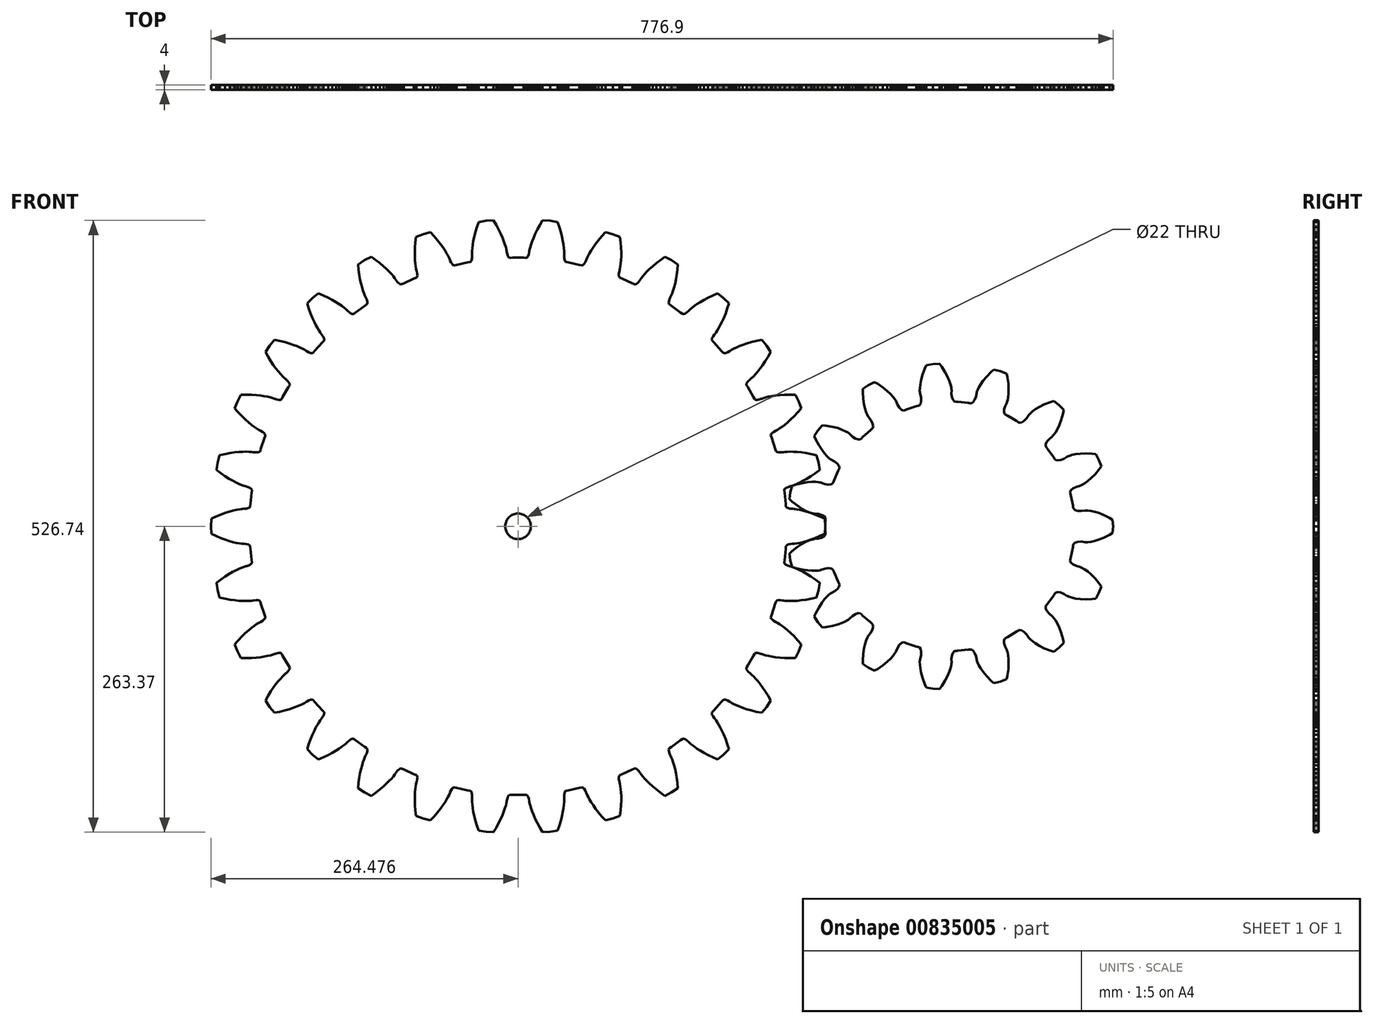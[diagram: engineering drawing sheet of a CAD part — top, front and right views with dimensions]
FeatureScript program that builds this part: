
annotation { "Feature Type Name" : "Feature", "Feature Type Description" : "" }
export const myFeature = defineFeature(function(context is Context, id is Id, definition is map)
    precondition{}
    {
        {
            var Q0;
            Q0=qCreatedBy(makeId("Front.planeOp"),FACE);
            var sketch = newSketch(context, id + "F0", { "sketchPlane" : qUnion([Q0])});
            skLineSegment(sketch, "E0", {"start": v(133.04, -61.26) * mm, "end": v(134.72, -54.99) * mm});
            skLineSegment(sketch, "E1", {"start": v(134.72, -54.99) * mm, "end": v(135.74, -48.57) * mm});
            skLineSegment(sketch, "E2", {"start": v(135.74, -48.57) * mm, "end": v(132, -45.77) * mm});
            skLineSegment(sketch, "E3", {"start": v(132, -45.77) * mm, "end": v(128.3, -43.23) * mm});
            skLineSegment(sketch, "E4", {"start": v(128.3, -43.23) * mm, "end": v(124.85, -41.06) * mm});
            skLineSegment(sketch, "E5", {"start": v(124.85, -41.06) * mm, "end": v(121.66, -39.25) * mm});
            skLineSegment(sketch, "E6", {"start": v(121.66, -39.25) * mm, "end": v(118.77, -37.75) * mm});
            skLineSegment(sketch, "E7", {"start": v(118.77, -37.75) * mm, "end": v(116.19, -36.56) * mm});
            skLineSegment(sketch, "E8", {"start": v(116.19, -36.56) * mm, "end": v(113.94, -35.63) * mm});
            skLineSegment(sketch, "E9", {"start": v(113.94, -35.63) * mm, "end": v(112.04, -34.93) * mm});
            skLineSegment(sketch, "E10", {"start": v(112.04, -34.93) * mm, "end": v(110.51, -34.45) * mm});
            skLineSegment(sketch, "E11", {"start": v(110.51, -34.45) * mm, "end": v(109.91, -34.28) * mm});
            skLineSegment(sketch, "E12", {"start": v(109.91, -34.28) * mm, "end": v(108.06, -33.66) * mm});
            skLineSegment(sketch, "E13", {"start": v(108.06, -33.66) * mm, "end": v(106.66, -32.97) * mm});
            skLineSegment(sketch, "E14", {"start": v(106.66, -32.97) * mm, "end": v(105.73, -32.23) * mm});
            skLineSegment(sketch, "E15", {"start": v(105.73, -32.23) * mm, "end": v(105.26, -31.5) * mm});
            skLineSegment(sketch, "E16", {"start": v(105.26, -31.5) * mm, "end": v(105.26, -30.79) * mm});
            skLineSegment(sketch, "E17", {"start": v(105.26, -30.79) * mm, "end": v(105.53, -29) * mm});
            skLineSegment(sketch, "E18", {"start": v(105.53, -29) * mm, "end": v(106.54, -19.36) * mm});
            skLineSegment(sketch, "E19", {"start": v(106.54, -19.36) * mm, "end": v(106.65, -17.55) * mm});
            skLineSegment(sketch, "E20", {"start": v(106.65, -17.55) * mm, "end": v(106.8, -16.86) * mm});
            skLineSegment(sketch, "E21", {"start": v(106.8, -16.86) * mm, "end": v(107.41, -16.23) * mm});
            skLineSegment(sketch, "E22", {"start": v(107.41, -16.23) * mm, "end": v(108.47, -15.7) * mm});
            skLineSegment(sketch, "E23", {"start": v(108.47, -15.7) * mm, "end": v(109.98, -15.31) * mm});
            skLineSegment(sketch, "E24", {"start": v(109.98, -15.31) * mm, "end": v(111.93, -15.1) * mm});
            skLineSegment(sketch, "E25", {"start": v(111.93, -15.1) * mm, "end": v(112.55, -15.06) * mm});
            skLineSegment(sketch, "E26", {"start": v(112.55, -15.06) * mm, "end": v(114.15, -14.9) * mm});
            skLineSegment(sketch, "E27", {"start": v(114.15, -14.9) * mm, "end": v(116.15, -14.62) * mm});
            skLineSegment(sketch, "E28", {"start": v(116.15, -14.62) * mm, "end": v(118.54, -14.17) * mm});
            skLineSegment(sketch, "E29", {"start": v(118.54, -14.17) * mm, "end": v(121.31, -13.54) * mm});
            skLineSegment(sketch, "E30", {"start": v(121.31, -13.54) * mm, "end": v(124.45, -12.68) * mm});
            skLineSegment(sketch, "E31", {"start": v(124.45, -12.68) * mm, "end": v(127.95, -11.57) * mm});
            skLineSegment(sketch, "E32", {"start": v(127.95, -11.57) * mm, "end": v(131.78, -10.17) * mm});
            skLineSegment(sketch, "E33", {"start": v(131.78, -10.17) * mm, "end": v(135.93, -8.45) * mm});
            skLineSegment(sketch, "E34", {"start": v(135.93, -8.45) * mm, "end": v(140.16, -6.49) * mm});
            skLineSegment(sketch, "E35", {"start": v(140.16, -6.49) * mm, "end": v(140.5, 0) * mm});
            skLineSegment(sketch, "E36", {"start": v(140.5, 0) * mm, "end": v(140.16, 6.49) * mm});
            skLineSegment(sketch, "E37", {"start": v(140.16, 6.49) * mm, "end": v(135.93, 8.45) * mm});
            skLineSegment(sketch, "E38", {"start": v(135.93, 8.45) * mm, "end": v(131.78, 10.17) * mm});
            skLineSegment(sketch, "E39", {"start": v(131.78, 10.17) * mm, "end": v(127.95, 11.57) * mm});
            skLineSegment(sketch, "E40", {"start": v(127.95, 11.57) * mm, "end": v(124.45, 12.68) * mm});
            skLineSegment(sketch, "E41", {"start": v(124.45, 12.68) * mm, "end": v(121.31, 13.54) * mm});
            skLineSegment(sketch, "E42", {"start": v(121.31, 13.54) * mm, "end": v(118.54, 14.17) * mm});
            skLineSegment(sketch, "E43", {"start": v(118.54, 14.17) * mm, "end": v(116.15, 14.62) * mm});
            skLineSegment(sketch, "E44", {"start": v(116.15, 14.62) * mm, "end": v(114.15, 14.9) * mm});
            skLineSegment(sketch, "E45", {"start": v(114.15, 14.9) * mm, "end": v(112.55, 15.06) * mm});
            skLineSegment(sketch, "E46", {"start": v(112.55, 15.06) * mm, "end": v(111.93, 15.1) * mm});
            skLineSegment(sketch, "E47", {"start": v(111.93, 15.1) * mm, "end": v(109.98, 15.31) * mm});
            skLineSegment(sketch, "E48", {"start": v(109.98, 15.31) * mm, "end": v(108.47, 15.7) * mm});
            skLineSegment(sketch, "E49", {"start": v(108.47, 15.7) * mm, "end": v(107.41, 16.23) * mm});
            skLineSegment(sketch, "E50", {"start": v(107.41, 16.23) * mm, "end": v(106.8, 16.86) * mm});
            skLineSegment(sketch, "E51", {"start": v(106.8, 16.86) * mm, "end": v(106.65, 17.55) * mm});
            skLineSegment(sketch, "E52", {"start": v(106.65, 17.55) * mm, "end": v(106.54, 19.36) * mm});
            skLineSegment(sketch, "E53", {"start": v(106.54, 19.36) * mm, "end": v(105.53, 29) * mm});
            skLineSegment(sketch, "E54", {"start": v(105.53, 29) * mm, "end": v(105.26, 30.79) * mm});
            skLineSegment(sketch, "E55", {"start": v(105.26, 30.79) * mm, "end": v(105.26, 31.5) * mm});
            skLineSegment(sketch, "E56", {"start": v(105.26, 31.5) * mm, "end": v(105.73, 32.23) * mm});
            skLineSegment(sketch, "E57", {"start": v(105.73, 32.23) * mm, "end": v(106.66, 32.97) * mm});
            skLineSegment(sketch, "E58", {"start": v(106.66, 32.97) * mm, "end": v(108.06, 33.66) * mm});
            skLineSegment(sketch, "E59", {"start": v(108.06, 33.66) * mm, "end": v(109.91, 34.28) * mm});
            skLineSegment(sketch, "E60", {"start": v(109.91, 34.28) * mm, "end": v(110.51, 34.45) * mm});
            skLineSegment(sketch, "E61", {"start": v(110.51, 34.45) * mm, "end": v(112.04, 34.93) * mm});
            skLineSegment(sketch, "E62", {"start": v(112.04, 34.93) * mm, "end": v(113.94, 35.63) * mm});
            skLineSegment(sketch, "E63", {"start": v(113.94, 35.63) * mm, "end": v(116.19, 36.56) * mm});
            skLineSegment(sketch, "E64", {"start": v(116.19, 36.56) * mm, "end": v(118.77, 37.75) * mm});
            skLineSegment(sketch, "E65", {"start": v(118.77, 37.75) * mm, "end": v(121.66, 39.25) * mm});
            skLineSegment(sketch, "E66", {"start": v(121.66, 39.25) * mm, "end": v(124.85, 41.06) * mm});
            skLineSegment(sketch, "E67", {"start": v(124.85, 41.06) * mm, "end": v(128.3, 43.23) * mm});
            skLineSegment(sketch, "E68", {"start": v(128.3, 43.23) * mm, "end": v(132, 45.77) * mm});
            skLineSegment(sketch, "E69", {"start": v(132, 45.77) * mm, "end": v(135.74, 48.57) * mm});
            skLineSegment(sketch, "E70", {"start": v(135.74, 48.57) * mm, "end": v(134.72, 54.99) * mm});
            skLineSegment(sketch, "E71", {"start": v(134.72, 54.99) * mm, "end": v(133.04, 61.26) * mm});
            skLineSegment(sketch, "E72", {"start": v(133.04, 61.26) * mm, "end": v(128.5, 62.3) * mm});
            skLineSegment(sketch, "E73", {"start": v(128.5, 62.3) * mm, "end": v(124.08, 63.12) * mm});
            skLineSegment(sketch, "E74", {"start": v(124.08, 63.12) * mm, "end": v(120.04, 63.7) * mm});
            skLineSegment(sketch, "E75", {"start": v(120.04, 63.7) * mm, "end": v(116.39, 64.06) * mm});
            skLineSegment(sketch, "E76", {"start": v(116.39, 64.06) * mm, "end": v(113.14, 64.24) * mm});
            skLineSegment(sketch, "E77", {"start": v(113.14, 64.24) * mm, "end": v(110.3, 64.29) * mm});
            skLineSegment(sketch, "E78", {"start": v(110.3, 64.29) * mm, "end": v(107.86, 64.22) * mm});
            skLineSegment(sketch, "E79", {"start": v(107.86, 64.22) * mm, "end": v(105.85, 64.08) * mm});
            skLineSegment(sketch, "E80", {"start": v(105.85, 64.08) * mm, "end": v(104.25, 63.9) * mm});
            skLineSegment(sketch, "E81", {"start": v(104.25, 63.9) * mm, "end": v(103.64, 63.81) * mm});
            skLineSegment(sketch, "E82", {"start": v(103.64, 63.81) * mm, "end": v(101.69, 63.62) * mm});
            skLineSegment(sketch, "E83", {"start": v(101.69, 63.62) * mm, "end": v(100.13, 63.7) * mm});
            skLineSegment(sketch, "E84", {"start": v(100.13, 63.7) * mm, "end": v(98.98, 63.99) * mm});
            skLineSegment(sketch, "E85", {"start": v(98.98, 63.99) * mm, "end": v(98.25, 64.47) * mm});
            skLineSegment(sketch, "E86", {"start": v(98.25, 64.47) * mm, "end": v(97.97, 65.11) * mm});
            skLineSegment(sketch, "E87", {"start": v(97.97, 65.11) * mm, "end": v(97.48, 66.86) * mm});
            skLineSegment(sketch, "E88", {"start": v(97.48, 66.86) * mm, "end": v(94.48, 76.07) * mm});
            skLineSegment(sketch, "E89", {"start": v(94.48, 76.07) * mm, "end": v(93.85, 77.78) * mm});
            skLineSegment(sketch, "E90", {"start": v(93.85, 77.78) * mm, "end": v(93.7, 78.46) * mm});
            skLineSegment(sketch, "E91", {"start": v(93.7, 78.46) * mm, "end": v(94, 79.28) * mm});
            skLineSegment(sketch, "E92", {"start": v(94, 79.28) * mm, "end": v(94.77, 80.2) * mm});
            skLineSegment(sketch, "E93", {"start": v(94.77, 80.2) * mm, "end": v(95.99, 81.17) * mm});
            skLineSegment(sketch, "E94", {"start": v(95.99, 81.17) * mm, "end": v(97.68, 82.16) * mm});
            skLineSegment(sketch, "E95", {"start": v(97.68, 82.16) * mm, "end": v(98.23, 82.44) * mm});
            skLineSegment(sketch, "E96", {"start": v(98.23, 82.44) * mm, "end": v(99.62, 83.24) * mm});
            skLineSegment(sketch, "E97", {"start": v(99.62, 83.24) * mm, "end": v(101.34, 84.31) * mm});
            skLineSegment(sketch, "E98", {"start": v(101.34, 84.31) * mm, "end": v(103.34, 85.7) * mm});
            skLineSegment(sketch, "E99", {"start": v(103.34, 85.7) * mm, "end": v(105.61, 87.4) * mm});
            skLineSegment(sketch, "E100", {"start": v(105.61, 87.4) * mm, "end": v(108.13, 89.46) * mm});
            skLineSegment(sketch, "E101", {"start": v(108.13, 89.46) * mm, "end": v(110.87, 91.9) * mm});
            skLineSegment(sketch, "E102", {"start": v(110.87, 91.9) * mm, "end": v(113.8, 94.74) * mm});
            skLineSegment(sketch, "E103", {"start": v(113.8, 94.74) * mm, "end": v(116.9, 98) * mm});
            skLineSegment(sketch, "E104", {"start": v(116.9, 98) * mm, "end": v(119.97, 101.5) * mm});
            skLineSegment(sketch, "E105", {"start": v(119.97, 101.5) * mm, "end": v(117.64, 107.57) * mm});
            skLineSegment(sketch, "E106", {"start": v(117.64, 107.57) * mm, "end": v(114.69, 113.36) * mm});
            skLineSegment(sketch, "E107", {"start": v(114.69, 113.36) * mm, "end": v(110.02, 113.43) * mm});
            skLineSegment(sketch, "E108", {"start": v(110.02, 113.43) * mm, "end": v(105.53, 113.31) * mm});
            skLineSegment(sketch, "E109", {"start": v(105.53, 113.31) * mm, "end": v(101.46, 113.03) * mm});
            skLineSegment(sketch, "E110", {"start": v(101.46, 113.03) * mm, "end": v(97.82, 112.63) * mm});
            skLineSegment(sketch, "E111", {"start": v(97.82, 112.63) * mm, "end": v(94.6, 112.14) * mm});
            skLineSegment(sketch, "E112", {"start": v(94.6, 112.14) * mm, "end": v(91.81, 111.59) * mm});
            skLineSegment(sketch, "E113", {"start": v(91.81, 111.59) * mm, "end": v(89.45, 111.02) * mm});
            skLineSegment(sketch, "E114", {"start": v(89.45, 111.02) * mm, "end": v(87.5, 110.47) * mm});
            skLineSegment(sketch, "E115", {"start": v(87.5, 110.47) * mm, "end": v(85.97, 109.96) * mm});
            skLineSegment(sketch, "E116", {"start": v(85.97, 109.96) * mm, "end": v(85.4, 109.74) * mm});
            skLineSegment(sketch, "E117", {"start": v(85.4, 109.74) * mm, "end": v(83.53, 109.15) * mm});
            skLineSegment(sketch, "E118", {"start": v(83.53, 109.15) * mm, "end": v(81.99, 108.9) * mm});
            skLineSegment(sketch, "E119", {"start": v(81.99, 108.9) * mm, "end": v(80.8, 108.94) * mm});
            skLineSegment(sketch, "E120", {"start": v(80.8, 108.94) * mm, "end": v(80, 109.27) * mm});
            skLineSegment(sketch, "E121", {"start": v(80, 109.27) * mm, "end": v(79.58, 109.83) * mm});
            skLineSegment(sketch, "E122", {"start": v(79.58, 109.83) * mm, "end": v(78.74, 111.44) * mm});
            skLineSegment(sketch, "E123", {"start": v(78.74, 111.44) * mm, "end": v(73.9, 119.83) * mm});
            skLineSegment(sketch, "E124", {"start": v(73.9, 119.83) * mm, "end": v(72.92, 121.36) * mm});
            skLineSegment(sketch, "E125", {"start": v(72.92, 121.36) * mm, "end": v(72.64, 122) * mm});
            skLineSegment(sketch, "E126", {"start": v(72.64, 122) * mm, "end": v(72.76, 122.87) * mm});
            skLineSegment(sketch, "E127", {"start": v(72.76, 122.87) * mm, "end": v(73.31, 123.92) * mm});
            skLineSegment(sketch, "E128", {"start": v(73.31, 123.92) * mm, "end": v(74.3, 125.13) * mm});
            skLineSegment(sketch, "E129", {"start": v(74.3, 125.13) * mm, "end": v(75.75, 126.45) * mm});
            skLineSegment(sketch, "E130", {"start": v(75.75, 126.45) * mm, "end": v(76.23, 126.84) * mm});
            skLineSegment(sketch, "E131", {"start": v(76.23, 126.84) * mm, "end": v(77.43, 127.91) * mm});
            skLineSegment(sketch, "E132", {"start": v(77.43, 127.91) * mm, "end": v(78.88, 129.32) * mm});
            skLineSegment(sketch, "E133", {"start": v(78.88, 129.32) * mm, "end": v(80.56, 131.08) * mm});
            skLineSegment(sketch, "E134", {"start": v(80.56, 131.08) * mm, "end": v(82.43, 133.22) * mm});
            skLineSegment(sketch, "E135", {"start": v(82.43, 133.22) * mm, "end": v(84.46, 135.76) * mm});
            skLineSegment(sketch, "E136", {"start": v(84.46, 135.76) * mm, "end": v(86.64, 138.72) * mm});
            skLineSegment(sketch, "E137", {"start": v(86.64, 138.72) * mm, "end": v(88.91, 142.1) * mm});
            skLineSegment(sketch, "E138", {"start": v(88.91, 142.1) * mm, "end": v(91.26, 145.93) * mm});
            skLineSegment(sketch, "E139", {"start": v(91.26, 145.93) * mm, "end": v(93.53, 150) * mm});
            skLineSegment(sketch, "E140", {"start": v(93.53, 150) * mm, "end": v(90, 155.46) * mm});
            skLineSegment(sketch, "E141", {"start": v(90, 155.46) * mm, "end": v(85.9, 160.5) * mm});
            skLineSegment(sketch, "E142", {"start": v(85.9, 160.5) * mm, "end": v(81.33, 159.6) * mm});
            skLineSegment(sketch, "E143", {"start": v(81.33, 159.6) * mm, "end": v(76.96, 158.55) * mm});
            skLineSegment(sketch, "E144", {"start": v(76.96, 158.55) * mm, "end": v(73.04, 157.43) * mm});
            skLineSegment(sketch, "E145", {"start": v(73.04, 157.43) * mm, "end": v(69.55, 156.28) * mm});
            skLineSegment(sketch, "E146", {"start": v(69.55, 156.28) * mm, "end": v(66.5, 155.13) * mm});
            skLineSegment(sketch, "E147", {"start": v(66.5, 155.13) * mm, "end": v(63.9, 154.01) * mm});
            skLineSegment(sketch, "E148", {"start": v(63.9, 154.01) * mm, "end": v(61.7, 152.97) * mm});
            skLineSegment(sketch, "E149", {"start": v(61.7, 152.97) * mm, "end": v(59.91, 152.02) * mm});
            skLineSegment(sketch, "E150", {"start": v(59.91, 152.02) * mm, "end": v(58.53, 151.2) * mm});
            skLineSegment(sketch, "E151", {"start": v(58.53, 151.2) * mm, "end": v(58, 150.87) * mm});
            skLineSegment(sketch, "E152", {"start": v(58, 150.87) * mm, "end": v(56.3, 149.9) * mm});
            skLineSegment(sketch, "E153", {"start": v(56.3, 149.9) * mm, "end": v(54.85, 149.34) * mm});
            skLineSegment(sketch, "E154", {"start": v(54.85, 149.34) * mm, "end": v(53.68, 149.14) * mm});
            skLineSegment(sketch, "E155", {"start": v(53.68, 149.14) * mm, "end": v(52.82, 149.29) * mm});
            skLineSegment(sketch, "E156", {"start": v(52.82, 149.29) * mm, "end": v(52.3, 149.75) * mm});
            skLineSegment(sketch, "E157", {"start": v(52.3, 149.75) * mm, "end": v(51.14, 151.15) * mm});
            skLineSegment(sketch, "E158", {"start": v(51.14, 151.15) * mm, "end": v(44.65, 158.35) * mm});
            skLineSegment(sketch, "E159", {"start": v(44.65, 158.35) * mm, "end": v(43.38, 159.65) * mm});
            skLineSegment(sketch, "E160", {"start": v(43.38, 159.65) * mm, "end": v(42.97, 160.22) * mm});
            skLineSegment(sketch, "E161", {"start": v(42.97, 160.22) * mm, "end": v(42.92, 161.1) * mm});
            skLineSegment(sketch, "E162", {"start": v(42.92, 161.1) * mm, "end": v(43.24, 162.23) * mm});
            skLineSegment(sketch, "E163", {"start": v(43.24, 162.23) * mm, "end": v(43.96, 163.62) * mm});
            skLineSegment(sketch, "E164", {"start": v(43.96, 163.62) * mm, "end": v(45.1, 165.21) * mm});
            skLineSegment(sketch, "E165", {"start": v(45.1, 165.21) * mm, "end": v(45.48, 165.7) * mm});
            skLineSegment(sketch, "E166", {"start": v(45.48, 165.7) * mm, "end": v(46.43, 167) * mm});
            skLineSegment(sketch, "E167", {"start": v(46.43, 167) * mm, "end": v(47.56, 168.67) * mm});
            skLineSegment(sketch, "E168", {"start": v(47.56, 168.67) * mm, "end": v(48.83, 170.74) * mm});
            skLineSegment(sketch, "E169", {"start": v(48.83, 170.74) * mm, "end": v(50.22, 173.22) * mm});
            skLineSegment(sketch, "E170", {"start": v(50.22, 173.22) * mm, "end": v(51.68, 176.13) * mm});
            skLineSegment(sketch, "E171", {"start": v(51.68, 176.13) * mm, "end": v(53.2, 179.47) * mm});
            skLineSegment(sketch, "E172", {"start": v(53.2, 179.47) * mm, "end": v(54.71, 183.26) * mm});
            skLineSegment(sketch, "E173", {"start": v(54.71, 183.26) * mm, "end": v(56.21, 187.5) * mm});
            skLineSegment(sketch, "E174", {"start": v(56.21, 187.5) * mm, "end": v(57.59, 191.95) * mm});
            skLineSegment(sketch, "E175", {"start": v(57.59, 191.95) * mm, "end": v(53, 196.55) * mm});
            skLineSegment(sketch, "E176", {"start": v(53, 196.55) * mm, "end": v(47.95, 200.63) * mm});
            skLineSegment(sketch, "E177", {"start": v(47.95, 200.63) * mm, "end": v(43.66, 198.8) * mm});
            skLineSegment(sketch, "E178", {"start": v(43.66, 198.8) * mm, "end": v(39.6, 196.87) * mm});
            skLineSegment(sketch, "E179", {"start": v(39.6, 196.87) * mm, "end": v(36, 194.96) * mm});
            skLineSegment(sketch, "E180", {"start": v(36, 194.96) * mm, "end": v(32.83, 193.1) * mm});
            skLineSegment(sketch, "E181", {"start": v(32.83, 193.1) * mm, "end": v(30.1, 191.34) * mm});
            skLineSegment(sketch, "E182", {"start": v(30.1, 191.34) * mm, "end": v(27.77, 189.7) * mm});
            skLineSegment(sketch, "E183", {"start": v(27.77, 189.7) * mm, "end": v(25.84, 188.23) * mm});
            skLineSegment(sketch, "E184", {"start": v(25.84, 188.23) * mm, "end": v(24.29, 186.93) * mm});
            skLineSegment(sketch, "E185", {"start": v(24.29, 186.93) * mm, "end": v(23.1, 185.85) * mm});
            skLineSegment(sketch, "E186", {"start": v(23.1, 185.85) * mm, "end": v(22.66, 185.41) * mm});
            skLineSegment(sketch, "E187", {"start": v(22.66, 185.41) * mm, "end": v(21.2, 184.11) * mm});
            skLineSegment(sketch, "E188", {"start": v(21.2, 184.11) * mm, "end": v(19.9, 183.25) * mm});
            skLineSegment(sketch, "E189", {"start": v(19.9, 183.25) * mm, "end": v(18.79, 182.81) * mm});
            skLineSegment(sketch, "E190", {"start": v(18.79, 182.81) * mm, "end": v(17.92, 182.78) * mm});
            skLineSegment(sketch, "E191", {"start": v(17.92, 182.78) * mm, "end": v(17.3, 183.13) * mm});
            skLineSegment(sketch, "E192", {"start": v(17.3, 183.13) * mm, "end": v(15.88, 184.26) * mm});
            skLineSegment(sketch, "E193", {"start": v(15.88, 184.26) * mm, "end": v(8.05, 189.95) * mm});
            skLineSegment(sketch, "E194", {"start": v(8.05, 189.95) * mm, "end": v(6.53, 190.96) * mm});
            skLineSegment(sketch, "E195", {"start": v(6.53, 190.96) * mm, "end": v(6.01, 191.43) * mm});
            skLineSegment(sketch, "E196", {"start": v(6.01, 191.43) * mm, "end": v(5.78, 192.27) * mm});
            skLineSegment(sketch, "E197", {"start": v(5.78, 192.27) * mm, "end": v(5.85, 193.45) * mm});
            skLineSegment(sketch, "E198", {"start": v(5.85, 193.45) * mm, "end": v(6.27, 194.96) * mm});
            skLineSegment(sketch, "E199", {"start": v(6.27, 194.96) * mm, "end": v(7.05, 196.75) * mm});
            skLineSegment(sketch, "E200", {"start": v(7.05, 196.75) * mm, "end": v(7.33, 197.3) * mm});
            skLineSegment(sketch, "E201", {"start": v(7.33, 197.3) * mm, "end": v(8, 198.77) * mm});
            skLineSegment(sketch, "E202", {"start": v(8, 198.77) * mm, "end": v(8.75, 200.65) * mm});
            skLineSegment(sketch, "E203", {"start": v(8.75, 200.65) * mm, "end": v(9.56, 202.94) * mm});
            skLineSegment(sketch, "E204", {"start": v(9.56, 202.94) * mm, "end": v(10.4, 205.66) * mm});
            skLineSegment(sketch, "E205", {"start": v(10.4, 205.66) * mm, "end": v(11.22, 208.8) * mm});
            skLineSegment(sketch, "E206", {"start": v(11.22, 208.8) * mm, "end": v(12, 212.39) * mm});
            skLineSegment(sketch, "E207", {"start": v(12, 212.39) * mm, "end": v(12.7, 216.4) * mm});
            skLineSegment(sketch, "E208", {"start": v(12.7, 216.4) * mm, "end": v(13.3, 220.86) * mm});
            skLineSegment(sketch, "E209", {"start": v(13.3, 220.86) * mm, "end": v(13.71, 225.5) * mm});
            skLineSegment(sketch, "E210", {"start": v(13.71, 225.5) * mm, "end": v(8.26, 229.04) * mm});
            skLineSegment(sketch, "E211", {"start": v(8.26, 229.04) * mm, "end": v(2.48, 232) * mm});
            skLineSegment(sketch, "E212", {"start": v(2.48, 232) * mm, "end": v(-1.34, 229.3) * mm});
            skLineSegment(sketch, "E213", {"start": v(-1.34, 229.3) * mm, "end": v(-4.9, 226.57) * mm});
            skLineSegment(sketch, "E214", {"start": v(-4.9, 226.57) * mm, "end": v(-8.03, 223.96) * mm});
            skLineSegment(sketch, "E215", {"start": v(-8.03, 223.96) * mm, "end": v(-10.74, 221.49) * mm});
            skLineSegment(sketch, "E216", {"start": v(-10.74, 221.49) * mm, "end": v(-13.06, 219.2) * mm});
            skLineSegment(sketch, "E217", {"start": v(-13.06, 219.2) * mm, "end": v(-15, 217.11) * mm});
            skLineSegment(sketch, "E218", {"start": v(-15, 217.11) * mm, "end": v(-16.57, 215.26) * mm});
            skLineSegment(sketch, "E219", {"start": v(-16.57, 215.26) * mm, "end": v(-17.82, 213.67) * mm});
            skLineSegment(sketch, "E220", {"start": v(-17.82, 213.67) * mm, "end": v(-18.75, 212.36) * mm});
            skLineSegment(sketch, "E221", {"start": v(-18.75, 212.36) * mm, "end": v(-19.1, 211.85) * mm});
            skLineSegment(sketch, "E222", {"start": v(-19.1, 211.85) * mm, "end": v(-20.26, 210.27) * mm});
            skLineSegment(sketch, "E223", {"start": v(-20.26, 210.27) * mm, "end": v(-21.35, 209.16) * mm});
            skLineSegment(sketch, "E224", {"start": v(-21.35, 209.16) * mm, "end": v(-22.34, 208.5) * mm});
            skLineSegment(sketch, "E225", {"start": v(-22.34, 208.5) * mm, "end": v(-23.19, 208.29) * mm});
            skLineSegment(sketch, "E226", {"start": v(-23.19, 208.29) * mm, "end": v(-23.86, 208.5) * mm});
            skLineSegment(sketch, "E227", {"start": v(-23.86, 208.5) * mm, "end": v(-25.48, 209.3) * mm});
            skLineSegment(sketch, "E228", {"start": v(-25.48, 209.3) * mm, "end": v(-34.33, 213.25) * mm});
            skLineSegment(sketch, "E229", {"start": v(-34.33, 213.25) * mm, "end": v(-36.02, 213.92) * mm});
            skLineSegment(sketch, "E230", {"start": v(-36.02, 213.92) * mm, "end": v(-36.63, 214.27) * mm});
            skLineSegment(sketch, "E231", {"start": v(-36.63, 214.27) * mm, "end": v(-37.03, 215.04) * mm});
            skLineSegment(sketch, "E232", {"start": v(-37.03, 215.04) * mm, "end": v(-37.2, 216.22) * mm});
            skLineSegment(sketch, "E233", {"start": v(-37.2, 216.22) * mm, "end": v(-37.11, 217.77) * mm});
            skLineSegment(sketch, "E234", {"start": v(-37.11, 217.77) * mm, "end": v(-36.72, 219.7) * mm});
            skLineSegment(sketch, "E235", {"start": v(-36.72, 219.7) * mm, "end": v(-36.56, 220.3) * mm});
            skLineSegment(sketch, "E236", {"start": v(-36.56, 220.3) * mm, "end": v(-36.22, 221.86) * mm});
            skLineSegment(sketch, "E237", {"start": v(-36.22, 221.86) * mm, "end": v(-35.87, 223.85) * mm});
            skLineSegment(sketch, "E238", {"start": v(-35.87, 223.85) * mm, "end": v(-35.55, 226.27) * mm});
            skLineSegment(sketch, "E239", {"start": v(-35.55, 226.27) * mm, "end": v(-35.3, 229.1) * mm});
            skLineSegment(sketch, "E240", {"start": v(-35.3, 229.1) * mm, "end": v(-35.14, 232.35) * mm});
            skLineSegment(sketch, "E241", {"start": v(-35.14, 232.35) * mm, "end": v(-35.12, 236.02) * mm});
            skLineSegment(sketch, "E242", {"start": v(-35.12, 236.02) * mm, "end": v(-35.27, 240.1) * mm});
            skLineSegment(sketch, "E243", {"start": v(-35.27, 240.1) * mm, "end": v(-35.62, 244.57) * mm});
            skLineSegment(sketch, "E244", {"start": v(-35.62, 244.57) * mm, "end": v(-36.18, 249.2) * mm});
            skLineSegment(sketch, "E245", {"start": v(-36.18, 249.2) * mm, "end": v(-42.25, 251.53) * mm});
            skLineSegment(sketch, "E246", {"start": v(-42.25, 251.53) * mm, "end": v(-48.52, 253.21) * mm});
            skLineSegment(sketch, "E247", {"start": v(-48.52, 253.21) * mm, "end": v(-51.7, 249.8) * mm});
            skLineSegment(sketch, "E248", {"start": v(-51.7, 249.8) * mm, "end": v(-54.61, 246.38) * mm});
            skLineSegment(sketch, "E249", {"start": v(-54.61, 246.38) * mm, "end": v(-57.13, 243.17) * mm});
            skLineSegment(sketch, "E250", {"start": v(-57.13, 243.17) * mm, "end": v(-59.27, 240.19) * mm});
            skLineSegment(sketch, "E251", {"start": v(-59.27, 240.19) * mm, "end": v(-61.05, 237.47) * mm});
            skLineSegment(sketch, "E252", {"start": v(-61.05, 237.47) * mm, "end": v(-62.51, 235.03) * mm});
            skLineSegment(sketch, "E253", {"start": v(-62.51, 235.03) * mm, "end": v(-63.67, 232.89) * mm});
            skLineSegment(sketch, "E254", {"start": v(-63.67, 232.89) * mm, "end": v(-64.56, 231.07) * mm});
            skLineSegment(sketch, "E255", {"start": v(-64.56, 231.07) * mm, "end": v(-65.2, 229.6) * mm});
            skLineSegment(sketch, "E256", {"start": v(-65.2, 229.6) * mm, "end": v(-65.43, 229.02) * mm});
            skLineSegment(sketch, "E257", {"start": v(-65.43, 229.02) * mm, "end": v(-66.24, 227.24) * mm});
            skLineSegment(sketch, "E258", {"start": v(-66.24, 227.24) * mm, "end": v(-67.08, 225.92) * mm});
            skLineSegment(sketch, "E259", {"start": v(-67.08, 225.92) * mm, "end": v(-67.91, 225.08) * mm});
            skLineSegment(sketch, "E260", {"start": v(-67.91, 225.08) * mm, "end": v(-68.7, 224.7) * mm});
            skLineSegment(sketch, "E261", {"start": v(-68.7, 224.7) * mm, "end": v(-69.4, 224.76) * mm});
            skLineSegment(sketch, "E262", {"start": v(-69.4, 224.76) * mm, "end": v(-71.15, 225.21) * mm});
            skLineSegment(sketch, "E263", {"start": v(-71.15, 225.21) * mm, "end": v(-80.63, 227.23) * mm});
            skLineSegment(sketch, "E264", {"start": v(-80.63, 227.23) * mm, "end": v(-82.42, 227.53) * mm});
            skLineSegment(sketch, "E265", {"start": v(-82.42, 227.53) * mm, "end": v(-83.09, 227.75) * mm});
            skLineSegment(sketch, "E266", {"start": v(-83.09, 227.75) * mm, "end": v(-83.64, 228.42) * mm});
            skLineSegment(sketch, "E267", {"start": v(-83.64, 228.42) * mm, "end": v(-84.06, 229.53) * mm});
            skLineSegment(sketch, "E268", {"start": v(-84.06, 229.53) * mm, "end": v(-84.29, 231.08) * mm});
            skLineSegment(sketch, "E269", {"start": v(-84.29, 231.08) * mm, "end": v(-84.3, 233.03) * mm});
            skLineSegment(sketch, "E270", {"start": v(-84.3, 233.03) * mm, "end": v(-84.27, 233.65) * mm});
            skLineSegment(sketch, "E271", {"start": v(-84.27, 233.65) * mm, "end": v(-84.26, 235.26) * mm});
            skLineSegment(sketch, "E272", {"start": v(-84.26, 235.26) * mm, "end": v(-84.34, 237.28) * mm});
            skLineSegment(sketch, "E273", {"start": v(-84.34, 237.28) * mm, "end": v(-84.53, 239.7) * mm});
            skLineSegment(sketch, "E274", {"start": v(-84.53, 239.7) * mm, "end": v(-84.87, 242.53) * mm});
            skLineSegment(sketch, "E275", {"start": v(-84.87, 242.53) * mm, "end": v(-85.4, 245.74) * mm});
            skLineSegment(sketch, "E276", {"start": v(-85.4, 245.74) * mm, "end": v(-86.14, 249.33) * mm});
            skLineSegment(sketch, "E277", {"start": v(-86.14, 249.33) * mm, "end": v(-87.13, 253.29) * mm});
            skLineSegment(sketch, "E278", {"start": v(-87.13, 253.29) * mm, "end": v(-88.4, 257.6) * mm});
            skLineSegment(sketch, "E279", {"start": v(-88.4, 257.6) * mm, "end": v(-89.91, 262.01) * mm});
            skLineSegment(sketch, "E280", {"start": v(-89.91, 262.01) * mm, "end": v(-96.33, 263.03) * mm});
            skLineSegment(sketch, "E281", {"start": v(-96.33, 263.03) * mm, "end": v(-102.81, 263.37) * mm});
            skLineSegment(sketch, "E282", {"start": v(-102.81, 263.37) * mm, "end": v(-105.21, 259.36) * mm});
            skLineSegment(sketch, "E283", {"start": v(-105.21, 259.36) * mm, "end": v(-107.35, 255.42) * mm});
            skLineSegment(sketch, "E284", {"start": v(-107.35, 255.42) * mm, "end": v(-109.15, 251.75) * mm});
            skLineSegment(sketch, "E285", {"start": v(-109.15, 251.75) * mm, "end": v(-110.62, 248.4) * mm});
            skLineSegment(sketch, "E286", {"start": v(-110.62, 248.4) * mm, "end": v(-111.8, 245.36) * mm});
            skLineSegment(sketch, "E287", {"start": v(-111.8, 245.36) * mm, "end": v(-112.72, 242.67) * mm});
            skLineSegment(sketch, "E288", {"start": v(-112.72, 242.67) * mm, "end": v(-113.41, 240.34) * mm});
            skLineSegment(sketch, "E289", {"start": v(-113.41, 240.34) * mm, "end": v(-113.9, 238.38) * mm});
            skLineSegment(sketch, "E290", {"start": v(-113.9, 238.38) * mm, "end": v(-114.23, 236.8) * mm});
            skLineSegment(sketch, "E291", {"start": v(-114.23, 236.8) * mm, "end": v(-114.33, 236.2) * mm});
            skLineSegment(sketch, "E292", {"start": v(-114.33, 236.2) * mm, "end": v(-114.75, 234.28) * mm});
            skLineSegment(sketch, "E293", {"start": v(-114.75, 234.28) * mm, "end": v(-115.3, 232.82) * mm});
            skLineSegment(sketch, "E294", {"start": v(-115.3, 232.82) * mm, "end": v(-115.93, 231.81) * mm});
            skLineSegment(sketch, "E295", {"start": v(-115.93, 231.81) * mm, "end": v(-116.62, 231.27) * mm});
            skLineSegment(sketch, "E296", {"start": v(-116.62, 231.27) * mm, "end": v(-117.32, 231.2) * mm});
            skLineSegment(sketch, "E297", {"start": v(-117.32, 231.2) * mm, "end": v(-119.13, 231.27) * mm});
            skLineSegment(sketch, "E298", {"start": v(-119.13, 231.27) * mm, "end": v(-128.82, 231.27) * mm});
            skLineSegment(sketch, "E299", {"start": v(-128.82, 231.27) * mm, "end": v(-130.63, 231.2) * mm});
            skLineSegment(sketch, "E300", {"start": v(-130.63, 231.2) * mm, "end": v(-131.33, 231.27) * mm});
            skLineSegment(sketch, "E301", {"start": v(-131.33, 231.27) * mm, "end": v(-132.02, 231.81) * mm});
            skLineSegment(sketch, "E302", {"start": v(-132.02, 231.81) * mm, "end": v(-132.65, 232.82) * mm});
            skLineSegment(sketch, "E303", {"start": v(-132.65, 232.82) * mm, "end": v(-133.2, 234.28) * mm});
            skLineSegment(sketch, "E304", {"start": v(-133.2, 234.28) * mm, "end": v(-133.62, 236.2) * mm});
            skLineSegment(sketch, "E305", {"start": v(-133.62, 236.2) * mm, "end": v(-133.72, 236.8) * mm});
            skLineSegment(sketch, "E306", {"start": v(-133.72, 236.8) * mm, "end": v(-134.05, 238.38) * mm});
            skLineSegment(sketch, "E307", {"start": v(-134.05, 238.38) * mm, "end": v(-134.54, 240.34) * mm});
            skLineSegment(sketch, "E308", {"start": v(-134.54, 240.34) * mm, "end": v(-135.23, 242.67) * mm});
            skLineSegment(sketch, "E309", {"start": v(-135.23, 242.67) * mm, "end": v(-136.15, 245.36) * mm});
            skLineSegment(sketch, "E310", {"start": v(-136.15, 245.36) * mm, "end": v(-137.33, 248.4) * mm});
            skLineSegment(sketch, "E311", {"start": v(-137.33, 248.4) * mm, "end": v(-138.8, 251.75) * mm});
            skLineSegment(sketch, "E312", {"start": v(-138.8, 251.75) * mm, "end": v(-140.6, 255.42) * mm});
            skLineSegment(sketch, "E313", {"start": v(-140.6, 255.42) * mm, "end": v(-142.74, 259.36) * mm});
            skLineSegment(sketch, "E314", {"start": v(-142.74, 259.36) * mm, "end": v(-145.13, 263.37) * mm});
            skLineSegment(sketch, "E315", {"start": v(-145.13, 263.37) * mm, "end": v(-151.62, 263.03) * mm});
            skLineSegment(sketch, "E316", {"start": v(-151.62, 263.03) * mm, "end": v(-158.03, 262.01) * mm});
            skLineSegment(sketch, "E317", {"start": v(-158.03, 262.01) * mm, "end": v(-159.55, 257.6) * mm});
            skLineSegment(sketch, "E318", {"start": v(-159.55, 257.6) * mm, "end": v(-160.82, 253.29) * mm});
            skLineSegment(sketch, "E319", {"start": v(-160.82, 253.29) * mm, "end": v(-161.81, 249.33) * mm});
            skLineSegment(sketch, "E320", {"start": v(-161.81, 249.33) * mm, "end": v(-162.55, 245.74) * mm});
            skLineSegment(sketch, "E321", {"start": v(-162.55, 245.74) * mm, "end": v(-163.08, 242.53) * mm});
            skLineSegment(sketch, "E322", {"start": v(-163.08, 242.53) * mm, "end": v(-163.42, 239.7) * mm});
            skLineSegment(sketch, "E323", {"start": v(-163.42, 239.7) * mm, "end": v(-163.6, 237.28) * mm});
            skLineSegment(sketch, "E324", {"start": v(-163.6, 237.28) * mm, "end": v(-163.68, 235.26) * mm});
            skLineSegment(sketch, "E325", {"start": v(-163.68, 235.26) * mm, "end": v(-163.67, 233.65) * mm});
            skLineSegment(sketch, "E326", {"start": v(-163.67, 233.65) * mm, "end": v(-163.65, 233.03) * mm});
            skLineSegment(sketch, "E327", {"start": v(-163.65, 233.03) * mm, "end": v(-163.66, 231.08) * mm});
            skLineSegment(sketch, "E328", {"start": v(-163.66, 231.08) * mm, "end": v(-163.9, 229.53) * mm});
            skLineSegment(sketch, "E329", {"start": v(-163.9, 229.53) * mm, "end": v(-164.3, 228.42) * mm});
            skLineSegment(sketch, "E330", {"start": v(-164.3, 228.42) * mm, "end": v(-164.86, 227.75) * mm});
            skLineSegment(sketch, "E331", {"start": v(-164.86, 227.75) * mm, "end": v(-165.53, 227.53) * mm});
            skLineSegment(sketch, "E332", {"start": v(-165.53, 227.53) * mm, "end": v(-167.32, 227.23) * mm});
            skLineSegment(sketch, "E333", {"start": v(-167.32, 227.23) * mm, "end": v(-176.8, 225.21) * mm});
            skLineSegment(sketch, "E334", {"start": v(-176.8, 225.21) * mm, "end": v(-178.56, 224.76) * mm});
            skLineSegment(sketch, "E335", {"start": v(-178.56, 224.76) * mm, "end": v(-179.25, 224.7) * mm});
            skLineSegment(sketch, "E336", {"start": v(-179.25, 224.7) * mm, "end": v(-180.04, 225.08) * mm});
            skLineSegment(sketch, "E337", {"start": v(-180.04, 225.08) * mm, "end": v(-180.87, 225.92) * mm});
            skLineSegment(sketch, "E338", {"start": v(-180.87, 225.92) * mm, "end": v(-181.7, 227.24) * mm});
            skLineSegment(sketch, "E339", {"start": v(-181.7, 227.24) * mm, "end": v(-182.52, 229.02) * mm});
            skLineSegment(sketch, "E340", {"start": v(-182.52, 229.02) * mm, "end": v(-182.74, 229.6) * mm});
            skLineSegment(sketch, "E341", {"start": v(-182.74, 229.6) * mm, "end": v(-183.39, 231.07) * mm});
            skLineSegment(sketch, "E342", {"start": v(-183.39, 231.07) * mm, "end": v(-184.28, 232.89) * mm});
            skLineSegment(sketch, "E343", {"start": v(-184.28, 232.89) * mm, "end": v(-185.44, 235.03) * mm});
            skLineSegment(sketch, "E344", {"start": v(-185.44, 235.03) * mm, "end": v(-186.9, 237.47) * mm});
            skLineSegment(sketch, "E345", {"start": v(-186.9, 237.47) * mm, "end": v(-188.68, 240.19) * mm});
            skLineSegment(sketch, "E346", {"start": v(-188.68, 240.19) * mm, "end": v(-190.82, 243.17) * mm});
            skLineSegment(sketch, "E347", {"start": v(-190.82, 243.17) * mm, "end": v(-193.34, 246.38) * mm});
            skLineSegment(sketch, "E348", {"start": v(-193.34, 246.38) * mm, "end": v(-196.25, 249.8) * mm});
            skLineSegment(sketch, "E349", {"start": v(-196.25, 249.8) * mm, "end": v(-199.43, 253.21) * mm});
            skLineSegment(sketch, "E350", {"start": v(-199.43, 253.21) * mm, "end": v(-205.7, 251.53) * mm});
            skLineSegment(sketch, "E351", {"start": v(-205.7, 251.53) * mm, "end": v(-211.77, 249.2) * mm});
            skLineSegment(sketch, "E352", {"start": v(-211.77, 249.2) * mm, "end": v(-212.32, 244.57) * mm});
            skLineSegment(sketch, "E353", {"start": v(-212.32, 244.57) * mm, "end": v(-212.68, 240.1) * mm});
            skLineSegment(sketch, "E354", {"start": v(-212.68, 240.1) * mm, "end": v(-212.82, 236.02) * mm});
            skLineSegment(sketch, "E355", {"start": v(-212.82, 236.02) * mm, "end": v(-212.8, 232.35) * mm});
            skLineSegment(sketch, "E356", {"start": v(-212.8, 232.35) * mm, "end": v(-212.65, 229.1) * mm});
            skLineSegment(sketch, "E357", {"start": v(-212.65, 229.1) * mm, "end": v(-212.4, 226.27) * mm});
            skLineSegment(sketch, "E358", {"start": v(-212.4, 226.27) * mm, "end": v(-212.08, 223.85) * mm});
            skLineSegment(sketch, "E359", {"start": v(-212.08, 223.85) * mm, "end": v(-211.73, 221.86) * mm});
            skLineSegment(sketch, "E360", {"start": v(-211.73, 221.86) * mm, "end": v(-211.39, 220.3) * mm});
            skLineSegment(sketch, "E361", {"start": v(-211.39, 220.3) * mm, "end": v(-211.23, 219.7) * mm});
            skLineSegment(sketch, "E362", {"start": v(-211.23, 219.7) * mm, "end": v(-210.84, 217.77) * mm});
            skLineSegment(sketch, "E363", {"start": v(-210.84, 217.77) * mm, "end": v(-210.74, 216.22) * mm});
            skLineSegment(sketch, "E364", {"start": v(-210.74, 216.22) * mm, "end": v(-210.91, 215.04) * mm});
            skLineSegment(sketch, "E365", {"start": v(-210.91, 215.04) * mm, "end": v(-211.32, 214.27) * mm});
            skLineSegment(sketch, "E366", {"start": v(-211.32, 214.27) * mm, "end": v(-211.93, 213.92) * mm});
            skLineSegment(sketch, "E367", {"start": v(-211.93, 213.92) * mm, "end": v(-213.62, 213.25) * mm});
            skLineSegment(sketch, "E368", {"start": v(-213.62, 213.25) * mm, "end": v(-222.47, 209.3) * mm});
            skLineSegment(sketch, "E369", {"start": v(-222.47, 209.3) * mm, "end": v(-224.1, 208.5) * mm});
            skLineSegment(sketch, "E370", {"start": v(-224.1, 208.5) * mm, "end": v(-224.76, 208.29) * mm});
            skLineSegment(sketch, "E371", {"start": v(-224.76, 208.29) * mm, "end": v(-225.6, 208.5) * mm});
            skLineSegment(sketch, "E372", {"start": v(-225.6, 208.5) * mm, "end": v(-226.6, 209.16) * mm});
            skLineSegment(sketch, "E373", {"start": v(-226.6, 209.16) * mm, "end": v(-227.7, 210.27) * mm});
            skLineSegment(sketch, "E374", {"start": v(-227.7, 210.27) * mm, "end": v(-228.85, 211.85) * mm});
            skLineSegment(sketch, "E375", {"start": v(-228.85, 211.85) * mm, "end": v(-229.2, 212.36) * mm});
            skLineSegment(sketch, "E376", {"start": v(-229.2, 212.36) * mm, "end": v(-230.13, 213.67) * mm});
            skLineSegment(sketch, "E377", {"start": v(-230.13, 213.67) * mm, "end": v(-231.38, 215.26) * mm});
            skLineSegment(sketch, "E378", {"start": v(-231.38, 215.26) * mm, "end": v(-232.96, 217.11) * mm});
            skLineSegment(sketch, "E379", {"start": v(-232.96, 217.11) * mm, "end": v(-234.9, 219.2) * mm});
            skLineSegment(sketch, "E380", {"start": v(-234.9, 219.2) * mm, "end": v(-237.2, 221.49) * mm});
            skLineSegment(sketch, "E381", {"start": v(-237.2, 221.49) * mm, "end": v(-239.92, 223.96) * mm});
            skLineSegment(sketch, "E382", {"start": v(-239.92, 223.96) * mm, "end": v(-243.05, 226.57) * mm});
            skLineSegment(sketch, "E383", {"start": v(-243.05, 226.57) * mm, "end": v(-246.6, 229.3) * mm});
            skLineSegment(sketch, "E384", {"start": v(-246.6, 229.3) * mm, "end": v(-250.43, 232) * mm});
            skLineSegment(sketch, "E385", {"start": v(-250.43, 232) * mm, "end": v(-256.21, 229.04) * mm});
            skLineSegment(sketch, "E386", {"start": v(-256.21, 229.04) * mm, "end": v(-261.66, 225.5) * mm});
            skLineSegment(sketch, "E387", {"start": v(-261.66, 225.5) * mm, "end": v(-261.24, 220.86) * mm});
            skLineSegment(sketch, "E388", {"start": v(-261.24, 220.86) * mm, "end": v(-260.66, 216.4) * mm});
            skLineSegment(sketch, "E389", {"start": v(-260.66, 216.4) * mm, "end": v(-259.95, 212.39) * mm});
            skLineSegment(sketch, "E390", {"start": v(-259.95, 212.39) * mm, "end": v(-259.17, 208.8) * mm});
            skLineSegment(sketch, "E391", {"start": v(-259.17, 208.8) * mm, "end": v(-258.34, 205.66) * mm});
            skLineSegment(sketch, "E392", {"start": v(-258.34, 205.66) * mm, "end": v(-257.5, 202.94) * mm});
            skLineSegment(sketch, "E393", {"start": v(-257.5, 202.94) * mm, "end": v(-256.7, 200.65) * mm});
            skLineSegment(sketch, "E394", {"start": v(-256.7, 200.65) * mm, "end": v(-255.94, 198.77) * mm});
            skLineSegment(sketch, "E395", {"start": v(-255.94, 198.77) * mm, "end": v(-255.28, 197.3) * mm});
            skLineSegment(sketch, "E396", {"start": v(-255.28, 197.3) * mm, "end": v(-255, 196.75) * mm});
            skLineSegment(sketch, "E397", {"start": v(-255, 196.75) * mm, "end": v(-254.22, 194.96) * mm});
            skLineSegment(sketch, "E398", {"start": v(-254.22, 194.96) * mm, "end": v(-253.8, 193.45) * mm});
            skLineSegment(sketch, "E399", {"start": v(-253.8, 193.45) * mm, "end": v(-253.72, 192.27) * mm});
            skLineSegment(sketch, "E400", {"start": v(-253.72, 192.27) * mm, "end": v(-253.96, 191.43) * mm});
            skLineSegment(sketch, "E401", {"start": v(-253.96, 191.43) * mm, "end": v(-254.48, 190.96) * mm});
            skLineSegment(sketch, "E402", {"start": v(-254.48, 190.96) * mm, "end": v(-256, 189.95) * mm});
            skLineSegment(sketch, "E403", {"start": v(-256, 189.95) * mm, "end": v(-263.83, 184.26) * mm});
            skLineSegment(sketch, "E404", {"start": v(-263.83, 184.26) * mm, "end": v(-265.25, 183.13) * mm});
            skLineSegment(sketch, "E405", {"start": v(-265.25, 183.13) * mm, "end": v(-265.86, 182.78) * mm});
            skLineSegment(sketch, "E406", {"start": v(-265.86, 182.78) * mm, "end": v(-266.74, 182.81) * mm});
            skLineSegment(sketch, "E407", {"start": v(-266.74, 182.81) * mm, "end": v(-267.84, 183.25) * mm});
            skLineSegment(sketch, "E408", {"start": v(-267.84, 183.25) * mm, "end": v(-269.14, 184.11) * mm});
            skLineSegment(sketch, "E409", {"start": v(-269.14, 184.11) * mm, "end": v(-270.6, 185.41) * mm});
            skLineSegment(sketch, "E410", {"start": v(-270.6, 185.41) * mm, "end": v(-271.05, 185.85) * mm});
            skLineSegment(sketch, "E411", {"start": v(-271.05, 185.85) * mm, "end": v(-272.24, 186.93) * mm});
            skLineSegment(sketch, "E412", {"start": v(-272.24, 186.93) * mm, "end": v(-273.79, 188.23) * mm});
            skLineSegment(sketch, "E413", {"start": v(-273.79, 188.23) * mm, "end": v(-275.72, 189.7) * mm});
            skLineSegment(sketch, "E414", {"start": v(-275.72, 189.7) * mm, "end": v(-278.04, 191.34) * mm});
            skLineSegment(sketch, "E415", {"start": v(-278.04, 191.34) * mm, "end": v(-280.78, 193.1) * mm});
            skLineSegment(sketch, "E416", {"start": v(-280.78, 193.1) * mm, "end": v(-283.95, 194.96) * mm});
            skLineSegment(sketch, "E417", {"start": v(-283.95, 194.96) * mm, "end": v(-287.55, 196.87) * mm});
            skLineSegment(sketch, "E418", {"start": v(-287.55, 196.87) * mm, "end": v(-291.6, 198.8) * mm});
            skLineSegment(sketch, "E419", {"start": v(-291.6, 198.8) * mm, "end": v(-295.9, 200.63) * mm});
            skLineSegment(sketch, "E420", {"start": v(-295.9, 200.63) * mm, "end": v(-300.94, 196.55) * mm});
            skLineSegment(sketch, "E421", {"start": v(-300.94, 196.55) * mm, "end": v(-305.54, 191.95) * mm});
            skLineSegment(sketch, "E422", {"start": v(-305.54, 191.95) * mm, "end": v(-304.16, 187.5) * mm});
            skLineSegment(sketch, "E423", {"start": v(-304.16, 187.5) * mm, "end": v(-302.66, 183.26) * mm});
            skLineSegment(sketch, "E424", {"start": v(-302.66, 183.26) * mm, "end": v(-301.14, 179.47) * mm});
            skLineSegment(sketch, "E425", {"start": v(-301.14, 179.47) * mm, "end": v(-299.63, 176.13) * mm});
            skLineSegment(sketch, "E426", {"start": v(-299.63, 176.13) * mm, "end": v(-298.17, 173.22) * mm});
            skLineSegment(sketch, "E427", {"start": v(-298.17, 173.22) * mm, "end": v(-296.78, 170.74) * mm});
            skLineSegment(sketch, "E428", {"start": v(-296.78, 170.74) * mm, "end": v(-295.51, 168.67) * mm});
            skLineSegment(sketch, "E429", {"start": v(-295.51, 168.67) * mm, "end": v(-294.38, 167) * mm});
            skLineSegment(sketch, "E430", {"start": v(-294.38, 167) * mm, "end": v(-293.43, 165.7) * mm});
            skLineSegment(sketch, "E431", {"start": v(-293.43, 165.7) * mm, "end": v(-293.04, 165.21) * mm});
            skLineSegment(sketch, "E432", {"start": v(-293.04, 165.21) * mm, "end": v(-291.9, 163.62) * mm});
            skLineSegment(sketch, "E433", {"start": v(-291.9, 163.62) * mm, "end": v(-291.18, 162.23) * mm});
            skLineSegment(sketch, "E434", {"start": v(-291.18, 162.23) * mm, "end": v(-290.86, 161.1) * mm});
            skLineSegment(sketch, "E435", {"start": v(-290.86, 161.1) * mm, "end": v(-290.92, 160.22) * mm});
            skLineSegment(sketch, "E436", {"start": v(-290.92, 160.22) * mm, "end": v(-291.33, 159.65) * mm});
            skLineSegment(sketch, "E437", {"start": v(-291.33, 159.65) * mm, "end": v(-292.6, 158.35) * mm});
            skLineSegment(sketch, "E438", {"start": v(-292.6, 158.35) * mm, "end": v(-299.09, 151.15) * mm});
            skLineSegment(sketch, "E439", {"start": v(-299.09, 151.15) * mm, "end": v(-300.24, 149.75) * mm});
            skLineSegment(sketch, "E440", {"start": v(-300.24, 149.75) * mm, "end": v(-300.77, 149.29) * mm});
            skLineSegment(sketch, "E441", {"start": v(-300.77, 149.29) * mm, "end": v(-301.63, 149.14) * mm});
            skLineSegment(sketch, "E442", {"start": v(-301.63, 149.14) * mm, "end": v(-302.8, 149.34) * mm});
            skLineSegment(sketch, "E443", {"start": v(-302.8, 149.34) * mm, "end": v(-304.25, 149.9) * mm});
            skLineSegment(sketch, "E444", {"start": v(-304.25, 149.9) * mm, "end": v(-305.95, 150.87) * mm});
            skLineSegment(sketch, "E445", {"start": v(-305.95, 150.87) * mm, "end": v(-306.47, 151.2) * mm});
            skLineSegment(sketch, "E446", {"start": v(-306.47, 151.2) * mm, "end": v(-307.86, 152.02) * mm});
            skLineSegment(sketch, "E447", {"start": v(-307.86, 152.02) * mm, "end": v(-309.65, 152.97) * mm});
            skLineSegment(sketch, "E448", {"start": v(-309.65, 152.97) * mm, "end": v(-311.84, 154.01) * mm});
            skLineSegment(sketch, "E449", {"start": v(-311.84, 154.01) * mm, "end": v(-314.46, 155.13) * mm});
            skLineSegment(sketch, "E450", {"start": v(-314.46, 155.13) * mm, "end": v(-317.5, 156.28) * mm});
            skLineSegment(sketch, "E451", {"start": v(-317.5, 156.28) * mm, "end": v(-320.98, 157.43) * mm});
            skLineSegment(sketch, "E452", {"start": v(-320.98, 157.43) * mm, "end": v(-324.9, 158.55) * mm});
            skLineSegment(sketch, "E453", {"start": v(-324.9, 158.55) * mm, "end": v(-329.27, 159.6) * mm});
            skLineSegment(sketch, "E454", {"start": v(-329.27, 159.6) * mm, "end": v(-333.85, 160.5) * mm});
            skLineSegment(sketch, "E455", {"start": v(-333.85, 160.5) * mm, "end": v(-337.94, 155.46) * mm});
            skLineSegment(sketch, "E456", {"start": v(-337.94, 155.46) * mm, "end": v(-341.48, 150) * mm});
            skLineSegment(sketch, "E457", {"start": v(-341.48, 150) * mm, "end": v(-339.2, 145.93) * mm});
            skLineSegment(sketch, "E458", {"start": v(-339.2, 145.93) * mm, "end": v(-336.86, 142.1) * mm});
            skLineSegment(sketch, "E459", {"start": v(-336.86, 142.1) * mm, "end": v(-334.58, 138.72) * mm});
            skLineSegment(sketch, "E460", {"start": v(-334.58, 138.72) * mm, "end": v(-332.41, 135.76) * mm});
            skLineSegment(sketch, "E461", {"start": v(-332.41, 135.76) * mm, "end": v(-330.37, 133.22) * mm});
            skLineSegment(sketch, "E462", {"start": v(-330.37, 133.22) * mm, "end": v(-328.5, 131.08) * mm});
            skLineSegment(sketch, "E463", {"start": v(-328.5, 131.08) * mm, "end": v(-326.83, 129.32) * mm});
            skLineSegment(sketch, "E464", {"start": v(-326.83, 129.32) * mm, "end": v(-325.38, 127.91) * mm});
            skLineSegment(sketch, "E465", {"start": v(-325.38, 127.91) * mm, "end": v(-324.18, 126.84) * mm});
            skLineSegment(sketch, "E466", {"start": v(-324.18, 126.84) * mm, "end": v(-323.7, 126.45) * mm});
            skLineSegment(sketch, "E467", {"start": v(-323.7, 126.45) * mm, "end": v(-322.25, 125.13) * mm});
            skLineSegment(sketch, "E468", {"start": v(-322.25, 125.13) * mm, "end": v(-321.26, 123.92) * mm});
            skLineSegment(sketch, "E469", {"start": v(-321.26, 123.92) * mm, "end": v(-320.7, 122.87) * mm});
            skLineSegment(sketch, "E470", {"start": v(-320.7, 122.87) * mm, "end": v(-320.58, 122) * mm});
            skLineSegment(sketch, "E471", {"start": v(-320.58, 122) * mm, "end": v(-320.87, 121.36) * mm});
            skLineSegment(sketch, "E472", {"start": v(-320.87, 121.36) * mm, "end": v(-321.84, 119.83) * mm});
            skLineSegment(sketch, "E473", {"start": v(-321.84, 119.83) * mm, "end": v(-326.69, 111.44) * mm});
            skLineSegment(sketch, "E474", {"start": v(-326.69, 111.44) * mm, "end": v(-327.53, 109.83) * mm});
            skLineSegment(sketch, "E475", {"start": v(-327.53, 109.83) * mm, "end": v(-327.94, 109.27) * mm});
            skLineSegment(sketch, "E476", {"start": v(-327.94, 109.27) * mm, "end": v(-328.75, 108.94) * mm});
            skLineSegment(sketch, "E477", {"start": v(-328.75, 108.94) * mm, "end": v(-329.94, 108.9) * mm});
            skLineSegment(sketch, "E478", {"start": v(-329.94, 108.9) * mm, "end": v(-331.48, 109.15) * mm});
            skLineSegment(sketch, "E479", {"start": v(-331.48, 109.15) * mm, "end": v(-333.34, 109.74) * mm});
            skLineSegment(sketch, "E480", {"start": v(-333.34, 109.74) * mm, "end": v(-333.92, 109.96) * mm});
            skLineSegment(sketch, "E481", {"start": v(-333.92, 109.96) * mm, "end": v(-335.45, 110.47) * mm});
            skLineSegment(sketch, "E482", {"start": v(-335.45, 110.47) * mm, "end": v(-337.4, 111.02) * mm});
            skLineSegment(sketch, "E483", {"start": v(-337.4, 111.02) * mm, "end": v(-339.76, 111.59) * mm});
            skLineSegment(sketch, "E484", {"start": v(-339.76, 111.59) * mm, "end": v(-342.55, 112.14) * mm});
            skLineSegment(sketch, "E485", {"start": v(-342.55, 112.14) * mm, "end": v(-345.77, 112.63) * mm});
            skLineSegment(sketch, "E486", {"start": v(-345.77, 112.63) * mm, "end": v(-349.41, 113.03) * mm});
            skLineSegment(sketch, "E487", {"start": v(-349.41, 113.03) * mm, "end": v(-353.48, 113.31) * mm});
            skLineSegment(sketch, "E488", {"start": v(-353.48, 113.31) * mm, "end": v(-357.97, 113.43) * mm});
            skLineSegment(sketch, "E489", {"start": v(-357.97, 113.43) * mm, "end": v(-362.64, 113.36) * mm});
            skLineSegment(sketch, "E490", {"start": v(-362.64, 113.36) * mm, "end": v(-365.59, 107.57) * mm});
            skLineSegment(sketch, "E491", {"start": v(-365.59, 107.57) * mm, "end": v(-367.91, 101.5) * mm});
            skLineSegment(sketch, "E492", {"start": v(-367.91, 101.5) * mm, "end": v(-364.84, 98) * mm});
            skLineSegment(sketch, "E493", {"start": v(-364.84, 98) * mm, "end": v(-361.75, 94.74) * mm});
            skLineSegment(sketch, "E494", {"start": v(-361.75, 94.74) * mm, "end": v(-358.82, 91.9) * mm});
            skLineSegment(sketch, "E495", {"start": v(-358.82, 91.9) * mm, "end": v(-356.08, 89.46) * mm});
            skLineSegment(sketch, "E496", {"start": v(-356.08, 89.46) * mm, "end": v(-353.56, 87.4) * mm});
            skLineSegment(sketch, "E497", {"start": v(-353.56, 87.4) * mm, "end": v(-351.29, 85.7) * mm});
            skLineSegment(sketch, "E498", {"start": v(-351.29, 85.7) * mm, "end": v(-349.28, 84.31) * mm});
            skLineSegment(sketch, "E499", {"start": v(-349.28, 84.31) * mm, "end": v(-347.57, 83.24) * mm});
            skLineSegment(sketch, "E500", {"start": v(-347.57, 83.24) * mm, "end": v(-346.17, 82.44) * mm});
            skLineSegment(sketch, "E501", {"start": v(-346.17, 82.44) * mm, "end": v(-345.62, 82.16) * mm});
            skLineSegment(sketch, "E502", {"start": v(-345.62, 82.16) * mm, "end": v(-343.93, 81.17) * mm});
            skLineSegment(sketch, "E503", {"start": v(-343.93, 81.17) * mm, "end": v(-342.71, 80.2) * mm});
            skLineSegment(sketch, "E504", {"start": v(-342.71, 80.2) * mm, "end": v(-341.96, 79.28) * mm});
            skLineSegment(sketch, "E505", {"start": v(-341.96, 79.28) * mm, "end": v(-341.66, 78.46) * mm});
            skLineSegment(sketch, "E506", {"start": v(-341.66, 78.46) * mm, "end": v(-341.8, 77.78) * mm});
            skLineSegment(sketch, "E507", {"start": v(-341.8, 77.78) * mm, "end": v(-342.43, 76.07) * mm});
            skLineSegment(sketch, "E508", {"start": v(-342.43, 76.07) * mm, "end": v(-345.43, 66.86) * mm});
            skLineSegment(sketch, "E509", {"start": v(-345.43, 66.86) * mm, "end": v(-345.91, 65.11) * mm});
            skLineSegment(sketch, "E510", {"start": v(-345.91, 65.11) * mm, "end": v(-346.2, 64.47) * mm});
            skLineSegment(sketch, "E511", {"start": v(-346.2, 64.47) * mm, "end": v(-346.93, 63.99) * mm});
            skLineSegment(sketch, "E512", {"start": v(-346.93, 63.99) * mm, "end": v(-348.08, 63.7) * mm});
            skLineSegment(sketch, "E513", {"start": v(-348.08, 63.7) * mm, "end": v(-349.64, 63.62) * mm});
            skLineSegment(sketch, "E514", {"start": v(-349.64, 63.62) * mm, "end": v(-351.59, 63.81) * mm});
            skLineSegment(sketch, "E515", {"start": v(-351.59, 63.81) * mm, "end": v(-352.2, 63.9) * mm});
            skLineSegment(sketch, "E516", {"start": v(-352.2, 63.9) * mm, "end": v(-353.8, 64.08) * mm});
            skLineSegment(sketch, "E517", {"start": v(-353.8, 64.08) * mm, "end": v(-355.81, 64.22) * mm});
            skLineSegment(sketch, "E518", {"start": v(-355.81, 64.22) * mm, "end": v(-358.24, 64.29) * mm});
            skLineSegment(sketch, "E519", {"start": v(-358.24, 64.29) * mm, "end": v(-361.09, 64.24) * mm});
            skLineSegment(sketch, "E520", {"start": v(-361.09, 64.24) * mm, "end": v(-364.34, 64.06) * mm});
            skLineSegment(sketch, "E521", {"start": v(-364.34, 64.06) * mm, "end": v(-367.99, 63.7) * mm});
            skLineSegment(sketch, "E522", {"start": v(-367.99, 63.7) * mm, "end": v(-372.02, 63.12) * mm});
            skLineSegment(sketch, "E523", {"start": v(-372.02, 63.12) * mm, "end": v(-376.44, 62.3) * mm});
            skLineSegment(sketch, "E524", {"start": v(-376.44, 62.3) * mm, "end": v(-381, 61.26) * mm});
            skLineSegment(sketch, "E525", {"start": v(-381, 61.26) * mm, "end": v(-382.67, 54.99) * mm});
            skLineSegment(sketch, "E526", {"start": v(-382.67, 54.99) * mm, "end": v(-383.69, 48.57) * mm});
            skLineSegment(sketch, "E527", {"start": v(-383.69, 48.57) * mm, "end": v(-379.95, 45.77) * mm});
            skLineSegment(sketch, "E528", {"start": v(-379.95, 45.77) * mm, "end": v(-376.25, 43.23) * mm});
            skLineSegment(sketch, "E529", {"start": v(-376.25, 43.23) * mm, "end": v(-372.8, 41.06) * mm});
            skLineSegment(sketch, "E530", {"start": v(-372.8, 41.06) * mm, "end": v(-369.61, 39.25) * mm});
            skLineSegment(sketch, "E531", {"start": v(-369.61, 39.25) * mm, "end": v(-366.72, 37.75) * mm});
            skLineSegment(sketch, "E532", {"start": v(-366.72, 37.75) * mm, "end": v(-364.14, 36.56) * mm});
            skLineSegment(sketch, "E533", {"start": v(-364.14, 36.56) * mm, "end": v(-361.89, 35.63) * mm});
            skLineSegment(sketch, "E534", {"start": v(-361.89, 35.63) * mm, "end": v(-360, 34.93) * mm});
            skLineSegment(sketch, "E535", {"start": v(-360, 34.93) * mm, "end": v(-358.46, 34.45) * mm});
            skLineSegment(sketch, "E536", {"start": v(-358.46, 34.45) * mm, "end": v(-357.86, 34.28) * mm});
            skLineSegment(sketch, "E537", {"start": v(-357.86, 34.28) * mm, "end": v(-356, 33.66) * mm});
            skLineSegment(sketch, "E538", {"start": v(-356, 33.66) * mm, "end": v(-354.6, 32.97) * mm});
            skLineSegment(sketch, "E539", {"start": v(-354.6, 32.97) * mm, "end": v(-353.68, 32.23) * mm});
            skLineSegment(sketch, "E540", {"start": v(-353.68, 32.23) * mm, "end": v(-353.21, 31.5) * mm});
            skLineSegment(sketch, "E541", {"start": v(-353.21, 31.5) * mm, "end": v(-353.2, 30.79) * mm});
            skLineSegment(sketch, "E542", {"start": v(-353.2, 30.79) * mm, "end": v(-353.47, 29) * mm});
            skLineSegment(sketch, "E543", {"start": v(-353.47, 29) * mm, "end": v(-354.49, 19.36) * mm});
            skLineSegment(sketch, "E544", {"start": v(-354.49, 19.36) * mm, "end": v(-354.6, 17.55) * mm});
            skLineSegment(sketch, "E545", {"start": v(-354.6, 17.55) * mm, "end": v(-354.75, 16.86) * mm});
            skLineSegment(sketch, "E546", {"start": v(-354.75, 16.86) * mm, "end": v(-355.36, 16.23) * mm});
            skLineSegment(sketch, "E547", {"start": v(-355.36, 16.23) * mm, "end": v(-356.42, 15.7) * mm});
            skLineSegment(sketch, "E548", {"start": v(-356.42, 15.7) * mm, "end": v(-357.93, 15.31) * mm});
            skLineSegment(sketch, "E549", {"start": v(-357.93, 15.31) * mm, "end": v(-359.88, 15.1) * mm});
            skLineSegment(sketch, "E550", {"start": v(-359.88, 15.1) * mm, "end": v(-360.5, 15.06) * mm});
            skLineSegment(sketch, "E551", {"start": v(-360.5, 15.06) * mm, "end": v(-362.1, 14.9) * mm});
            skLineSegment(sketch, "E552", {"start": v(-362.1, 14.9) * mm, "end": v(-364.1, 14.62) * mm});
            skLineSegment(sketch, "E553", {"start": v(-364.1, 14.62) * mm, "end": v(-366.49, 14.17) * mm});
            skLineSegment(sketch, "E554", {"start": v(-366.49, 14.17) * mm, "end": v(-369.26, 13.54) * mm});
            skLineSegment(sketch, "E555", {"start": v(-369.26, 13.54) * mm, "end": v(-372.4, 12.68) * mm});
            skLineSegment(sketch, "E556", {"start": v(-372.4, 12.68) * mm, "end": v(-375.9, 11.57) * mm});
            skLineSegment(sketch, "E557", {"start": v(-375.9, 11.57) * mm, "end": v(-379.73, 10.17) * mm});
            skLineSegment(sketch, "E558", {"start": v(-379.73, 10.17) * mm, "end": v(-383.88, 8.45) * mm});
            skLineSegment(sketch, "E559", {"start": v(-383.88, 8.45) * mm, "end": v(-388.11, 6.49) * mm});
            skLineSegment(sketch, "E560", {"start": v(-388.11, 6.49) * mm, "end": v(-388.45, 0) * mm});
            skLineSegment(sketch, "E561", {"start": v(-388.45, 0) * mm, "end": v(-388.11, -6.49) * mm});
            skLineSegment(sketch, "E562", {"start": v(-388.11, -6.49) * mm, "end": v(-383.88, -8.45) * mm});
            skLineSegment(sketch, "E563", {"start": v(-383.88, -8.45) * mm, "end": v(-379.73, -10.17) * mm});
            skLineSegment(sketch, "E564", {"start": v(-379.73, -10.17) * mm, "end": v(-375.9, -11.57) * mm});
            skLineSegment(sketch, "E565", {"start": v(-375.9, -11.57) * mm, "end": v(-372.4, -12.68) * mm});
            skLineSegment(sketch, "E566", {"start": v(-372.4, -12.68) * mm, "end": v(-369.26, -13.54) * mm});
            skLineSegment(sketch, "E567", {"start": v(-369.26, -13.54) * mm, "end": v(-366.49, -14.17) * mm});
            skLineSegment(sketch, "E568", {"start": v(-366.49, -14.17) * mm, "end": v(-364.1, -14.62) * mm});
            skLineSegment(sketch, "E569", {"start": v(-364.1, -14.62) * mm, "end": v(-362.1, -14.9) * mm});
            skLineSegment(sketch, "E570", {"start": v(-362.1, -14.9) * mm, "end": v(-360.5, -15.06) * mm});
            skLineSegment(sketch, "E571", {"start": v(-360.5, -15.06) * mm, "end": v(-359.88, -15.1) * mm});
            skLineSegment(sketch, "E572", {"start": v(-359.88, -15.1) * mm, "end": v(-357.93, -15.31) * mm});
            skLineSegment(sketch, "E573", {"start": v(-357.93, -15.31) * mm, "end": v(-356.42, -15.7) * mm});
            skLineSegment(sketch, "E574", {"start": v(-356.42, -15.7) * mm, "end": v(-355.36, -16.23) * mm});
            skLineSegment(sketch, "E575", {"start": v(-355.36, -16.23) * mm, "end": v(-354.75, -16.86) * mm});
            skLineSegment(sketch, "E576", {"start": v(-354.75, -16.86) * mm, "end": v(-354.6, -17.55) * mm});
            skLineSegment(sketch, "E577", {"start": v(-354.6, -17.55) * mm, "end": v(-354.49, -19.36) * mm});
            skLineSegment(sketch, "E578", {"start": v(-354.49, -19.36) * mm, "end": v(-353.47, -29) * mm});
            skLineSegment(sketch, "E579", {"start": v(-353.47, -29) * mm, "end": v(-353.2, -30.79) * mm});
            skLineSegment(sketch, "E580", {"start": v(-353.2, -30.79) * mm, "end": v(-353.21, -31.5) * mm});
            skLineSegment(sketch, "E581", {"start": v(-353.21, -31.5) * mm, "end": v(-353.68, -32.23) * mm});
            skLineSegment(sketch, "E582", {"start": v(-353.68, -32.23) * mm, "end": v(-354.6, -32.97) * mm});
            skLineSegment(sketch, "E583", {"start": v(-354.6, -32.97) * mm, "end": v(-356, -33.66) * mm});
            skLineSegment(sketch, "E584", {"start": v(-356, -33.66) * mm, "end": v(-357.86, -34.28) * mm});
            skLineSegment(sketch, "E585", {"start": v(-357.86, -34.28) * mm, "end": v(-358.46, -34.45) * mm});
            skLineSegment(sketch, "E586", {"start": v(-358.46, -34.45) * mm, "end": v(-360, -34.93) * mm});
            skLineSegment(sketch, "E587", {"start": v(-360, -34.93) * mm, "end": v(-361.89, -35.63) * mm});
            skLineSegment(sketch, "E588", {"start": v(-361.89, -35.63) * mm, "end": v(-364.14, -36.56) * mm});
            skLineSegment(sketch, "E589", {"start": v(-364.14, -36.56) * mm, "end": v(-366.72, -37.75) * mm});
            skLineSegment(sketch, "E590", {"start": v(-366.72, -37.75) * mm, "end": v(-369.61, -39.25) * mm});
            skLineSegment(sketch, "E591", {"start": v(-369.61, -39.25) * mm, "end": v(-372.8, -41.06) * mm});
            skLineSegment(sketch, "E592", {"start": v(-372.8, -41.06) * mm, "end": v(-376.25, -43.23) * mm});
            skLineSegment(sketch, "E593", {"start": v(-376.25, -43.23) * mm, "end": v(-379.95, -45.77) * mm});
            skLineSegment(sketch, "E594", {"start": v(-379.95, -45.77) * mm, "end": v(-383.69, -48.57) * mm});
            skLineSegment(sketch, "E595", {"start": v(-383.69, -48.57) * mm, "end": v(-382.67, -54.99) * mm});
            skLineSegment(sketch, "E596", {"start": v(-382.67, -54.99) * mm, "end": v(-381, -61.26) * mm});
            skLineSegment(sketch, "E597", {"start": v(-381, -61.26) * mm, "end": v(-376.44, -62.3) * mm});
            skLineSegment(sketch, "E598", {"start": v(-376.44, -62.3) * mm, "end": v(-372.02, -63.12) * mm});
            skLineSegment(sketch, "E599", {"start": v(-372.02, -63.12) * mm, "end": v(-367.99, -63.7) * mm});
            skLineSegment(sketch, "E600", {"start": v(-367.99, -63.7) * mm, "end": v(-364.34, -64.06) * mm});
            skLineSegment(sketch, "E601", {"start": v(-364.34, -64.06) * mm, "end": v(-361.09, -64.24) * mm});
            skLineSegment(sketch, "E602", {"start": v(-361.09, -64.24) * mm, "end": v(-358.24, -64.29) * mm});
            skLineSegment(sketch, "E603", {"start": v(-358.24, -64.29) * mm, "end": v(-355.81, -64.22) * mm});
            skLineSegment(sketch, "E604", {"start": v(-355.81, -64.22) * mm, "end": v(-353.8, -64.08) * mm});
            skLineSegment(sketch, "E605", {"start": v(-353.8, -64.08) * mm, "end": v(-352.2, -63.9) * mm});
            skLineSegment(sketch, "E606", {"start": v(-352.2, -63.9) * mm, "end": v(-351.59, -63.81) * mm});
            skLineSegment(sketch, "E607", {"start": v(-351.59, -63.81) * mm, "end": v(-349.64, -63.62) * mm});
            skLineSegment(sketch, "E608", {"start": v(-349.64, -63.62) * mm, "end": v(-348.08, -63.7) * mm});
            skLineSegment(sketch, "E609", {"start": v(-348.08, -63.7) * mm, "end": v(-346.93, -63.99) * mm});
            skLineSegment(sketch, "E610", {"start": v(-346.93, -63.99) * mm, "end": v(-346.2, -64.47) * mm});
            skLineSegment(sketch, "E611", {"start": v(-346.2, -64.47) * mm, "end": v(-345.91, -65.11) * mm});
            skLineSegment(sketch, "E612", {"start": v(-345.91, -65.11) * mm, "end": v(-345.43, -66.86) * mm});
            skLineSegment(sketch, "E613", {"start": v(-345.43, -66.86) * mm, "end": v(-342.43, -76.07) * mm});
            skLineSegment(sketch, "E614", {"start": v(-342.43, -76.07) * mm, "end": v(-341.8, -77.78) * mm});
            skLineSegment(sketch, "E615", {"start": v(-341.8, -77.78) * mm, "end": v(-341.66, -78.46) * mm});
            skLineSegment(sketch, "E616", {"start": v(-341.66, -78.46) * mm, "end": v(-341.96, -79.28) * mm});
            skLineSegment(sketch, "E617", {"start": v(-341.96, -79.28) * mm, "end": v(-342.71, -80.2) * mm});
            skLineSegment(sketch, "E618", {"start": v(-342.71, -80.2) * mm, "end": v(-343.93, -81.17) * mm});
            skLineSegment(sketch, "E619", {"start": v(-343.93, -81.17) * mm, "end": v(-345.62, -82.16) * mm});
            skLineSegment(sketch, "E620", {"start": v(-345.62, -82.16) * mm, "end": v(-346.17, -82.44) * mm});
            skLineSegment(sketch, "E621", {"start": v(-346.17, -82.44) * mm, "end": v(-347.57, -83.24) * mm});
            skLineSegment(sketch, "E622", {"start": v(-347.57, -83.24) * mm, "end": v(-349.28, -84.31) * mm});
            skLineSegment(sketch, "E623", {"start": v(-349.28, -84.31) * mm, "end": v(-351.29, -85.7) * mm});
            skLineSegment(sketch, "E624", {"start": v(-351.29, -85.7) * mm, "end": v(-353.56, -87.4) * mm});
            skLineSegment(sketch, "E625", {"start": v(-353.56, -87.4) * mm, "end": v(-356.08, -89.46) * mm});
            skLineSegment(sketch, "E626", {"start": v(-356.08, -89.46) * mm, "end": v(-358.82, -91.9) * mm});
            skLineSegment(sketch, "E627", {"start": v(-358.82, -91.9) * mm, "end": v(-361.75, -94.74) * mm});
            skLineSegment(sketch, "E628", {"start": v(-361.75, -94.74) * mm, "end": v(-364.84, -98) * mm});
            skLineSegment(sketch, "E629", {"start": v(-364.84, -98) * mm, "end": v(-367.91, -101.5) * mm});
            skLineSegment(sketch, "E630", {"start": v(-367.91, -101.5) * mm, "end": v(-365.59, -107.57) * mm});
            skLineSegment(sketch, "E631", {"start": v(-365.59, -107.57) * mm, "end": v(-362.64, -113.36) * mm});
            skLineSegment(sketch, "E632", {"start": v(-362.64, -113.36) * mm, "end": v(-357.97, -113.43) * mm});
            skLineSegment(sketch, "E633", {"start": v(-357.97, -113.43) * mm, "end": v(-353.48, -113.31) * mm});
            skLineSegment(sketch, "E634", {"start": v(-353.48, -113.31) * mm, "end": v(-349.41, -113.03) * mm});
            skLineSegment(sketch, "E635", {"start": v(-349.41, -113.03) * mm, "end": v(-345.77, -112.63) * mm});
            skLineSegment(sketch, "E636", {"start": v(-345.77, -112.63) * mm, "end": v(-342.55, -112.14) * mm});
            skLineSegment(sketch, "E637", {"start": v(-342.55, -112.14) * mm, "end": v(-339.76, -111.59) * mm});
            skLineSegment(sketch, "E638", {"start": v(-339.76, -111.59) * mm, "end": v(-337.4, -111.02) * mm});
            skLineSegment(sketch, "E639", {"start": v(-337.4, -111.02) * mm, "end": v(-335.45, -110.47) * mm});
            skLineSegment(sketch, "E640", {"start": v(-335.45, -110.47) * mm, "end": v(-333.92, -109.96) * mm});
            skLineSegment(sketch, "E641", {"start": v(-333.92, -109.96) * mm, "end": v(-333.34, -109.74) * mm});
            skLineSegment(sketch, "E642", {"start": v(-333.34, -109.74) * mm, "end": v(-331.48, -109.15) * mm});
            skLineSegment(sketch, "E643", {"start": v(-331.48, -109.15) * mm, "end": v(-329.94, -108.9) * mm});
            skLineSegment(sketch, "E644", {"start": v(-329.94, -108.9) * mm, "end": v(-328.75, -108.94) * mm});
            skLineSegment(sketch, "E645", {"start": v(-328.75, -108.94) * mm, "end": v(-327.94, -109.27) * mm});
            skLineSegment(sketch, "E646", {"start": v(-327.94, -109.27) * mm, "end": v(-327.53, -109.83) * mm});
            skLineSegment(sketch, "E647", {"start": v(-327.53, -109.83) * mm, "end": v(-326.69, -111.44) * mm});
            skLineSegment(sketch, "E648", {"start": v(-326.69, -111.44) * mm, "end": v(-321.84, -119.83) * mm});
            skLineSegment(sketch, "E649", {"start": v(-321.84, -119.83) * mm, "end": v(-320.87, -121.36) * mm});
            skLineSegment(sketch, "E650", {"start": v(-320.87, -121.36) * mm, "end": v(-320.58, -122) * mm});
            skLineSegment(sketch, "E651", {"start": v(-320.58, -122) * mm, "end": v(-320.7, -122.87) * mm});
            skLineSegment(sketch, "E652", {"start": v(-320.7, -122.87) * mm, "end": v(-321.26, -123.92) * mm});
            skLineSegment(sketch, "E653", {"start": v(-321.26, -123.92) * mm, "end": v(-322.25, -125.13) * mm});
            skLineSegment(sketch, "E654", {"start": v(-322.25, -125.13) * mm, "end": v(-323.7, -126.45) * mm});
            skLineSegment(sketch, "E655", {"start": v(-323.7, -126.45) * mm, "end": v(-324.18, -126.84) * mm});
            skLineSegment(sketch, "E656", {"start": v(-324.18, -126.84) * mm, "end": v(-325.38, -127.91) * mm});
            skLineSegment(sketch, "E657", {"start": v(-325.38, -127.91) * mm, "end": v(-326.83, -129.32) * mm});
            skLineSegment(sketch, "E658", {"start": v(-326.83, -129.32) * mm, "end": v(-328.5, -131.08) * mm});
            skLineSegment(sketch, "E659", {"start": v(-328.5, -131.08) * mm, "end": v(-330.37, -133.22) * mm});
            skLineSegment(sketch, "E660", {"start": v(-330.37, -133.22) * mm, "end": v(-332.41, -135.76) * mm});
            skLineSegment(sketch, "E661", {"start": v(-332.41, -135.76) * mm, "end": v(-334.58, -138.72) * mm});
            skLineSegment(sketch, "E662", {"start": v(-334.58, -138.72) * mm, "end": v(-336.86, -142.1) * mm});
            skLineSegment(sketch, "E663", {"start": v(-336.86, -142.1) * mm, "end": v(-339.2, -145.93) * mm});
            skLineSegment(sketch, "E664", {"start": v(-339.2, -145.93) * mm, "end": v(-341.48, -150) * mm});
            skLineSegment(sketch, "E665", {"start": v(-341.48, -150) * mm, "end": v(-337.94, -155.46) * mm});
            skLineSegment(sketch, "E666", {"start": v(-337.94, -155.46) * mm, "end": v(-333.85, -160.5) * mm});
            skLineSegment(sketch, "E667", {"start": v(-333.85, -160.5) * mm, "end": v(-329.27, -159.6) * mm});
            skLineSegment(sketch, "E668", {"start": v(-329.27, -159.6) * mm, "end": v(-324.9, -158.55) * mm});
            skLineSegment(sketch, "E669", {"start": v(-324.9, -158.55) * mm, "end": v(-320.98, -157.43) * mm});
            skLineSegment(sketch, "E670", {"start": v(-320.98, -157.43) * mm, "end": v(-317.5, -156.28) * mm});
            skLineSegment(sketch, "E671", {"start": v(-317.5, -156.28) * mm, "end": v(-314.46, -155.13) * mm});
            skLineSegment(sketch, "E672", {"start": v(-314.46, -155.13) * mm, "end": v(-311.84, -154.01) * mm});
            skLineSegment(sketch, "E673", {"start": v(-311.84, -154.01) * mm, "end": v(-309.65, -152.97) * mm});
            skLineSegment(sketch, "E674", {"start": v(-309.65, -152.97) * mm, "end": v(-307.86, -152.02) * mm});
            skLineSegment(sketch, "E675", {"start": v(-307.86, -152.02) * mm, "end": v(-306.47, -151.2) * mm});
            skLineSegment(sketch, "E676", {"start": v(-306.47, -151.2) * mm, "end": v(-305.95, -150.87) * mm});
            skLineSegment(sketch, "E677", {"start": v(-305.95, -150.87) * mm, "end": v(-304.25, -149.9) * mm});
            skLineSegment(sketch, "E678", {"start": v(-304.25, -149.9) * mm, "end": v(-302.8, -149.34) * mm});
            skLineSegment(sketch, "E679", {"start": v(-302.8, -149.34) * mm, "end": v(-301.63, -149.14) * mm});
            skLineSegment(sketch, "E680", {"start": v(-301.63, -149.14) * mm, "end": v(-300.77, -149.29) * mm});
            skLineSegment(sketch, "E681", {"start": v(-300.77, -149.29) * mm, "end": v(-300.24, -149.75) * mm});
            skLineSegment(sketch, "E682", {"start": v(-300.24, -149.75) * mm, "end": v(-299.09, -151.15) * mm});
            skLineSegment(sketch, "E683", {"start": v(-299.09, -151.15) * mm, "end": v(-292.6, -158.35) * mm});
            skLineSegment(sketch, "E684", {"start": v(-292.6, -158.35) * mm, "end": v(-291.33, -159.65) * mm});
            skLineSegment(sketch, "E685", {"start": v(-291.33, -159.65) * mm, "end": v(-290.92, -160.22) * mm});
            skLineSegment(sketch, "E686", {"start": v(-290.92, -160.22) * mm, "end": v(-290.86, -161.1) * mm});
            skLineSegment(sketch, "E687", {"start": v(-290.86, -161.1) * mm, "end": v(-291.18, -162.23) * mm});
            skLineSegment(sketch, "E688", {"start": v(-291.18, -162.23) * mm, "end": v(-291.9, -163.62) * mm});
            skLineSegment(sketch, "E689", {"start": v(-291.9, -163.62) * mm, "end": v(-293.04, -165.21) * mm});
            skLineSegment(sketch, "E690", {"start": v(-293.04, -165.21) * mm, "end": v(-293.43, -165.7) * mm});
            skLineSegment(sketch, "E691", {"start": v(-293.43, -165.7) * mm, "end": v(-294.38, -167) * mm});
            skLineSegment(sketch, "E692", {"start": v(-294.38, -167) * mm, "end": v(-295.51, -168.67) * mm});
            skLineSegment(sketch, "E693", {"start": v(-295.51, -168.67) * mm, "end": v(-296.78, -170.74) * mm});
            skLineSegment(sketch, "E694", {"start": v(-296.78, -170.74) * mm, "end": v(-298.17, -173.22) * mm});
            skLineSegment(sketch, "E695", {"start": v(-298.17, -173.22) * mm, "end": v(-299.63, -176.13) * mm});
            skLineSegment(sketch, "E696", {"start": v(-299.63, -176.13) * mm, "end": v(-301.14, -179.47) * mm});
            skLineSegment(sketch, "E697", {"start": v(-301.14, -179.47) * mm, "end": v(-302.66, -183.26) * mm});
            skLineSegment(sketch, "E698", {"start": v(-302.66, -183.26) * mm, "end": v(-304.16, -187.5) * mm});
            skLineSegment(sketch, "E699", {"start": v(-304.16, -187.5) * mm, "end": v(-305.54, -191.95) * mm});
            skLineSegment(sketch, "E700", {"start": v(-305.54, -191.95) * mm, "end": v(-300.94, -196.55) * mm});
            skLineSegment(sketch, "E701", {"start": v(-300.94, -196.55) * mm, "end": v(-295.9, -200.63) * mm});
            skLineSegment(sketch, "E702", {"start": v(-295.9, -200.63) * mm, "end": v(-291.6, -198.8) * mm});
            skLineSegment(sketch, "E703", {"start": v(-291.6, -198.8) * mm, "end": v(-287.55, -196.87) * mm});
            skLineSegment(sketch, "E704", {"start": v(-287.55, -196.87) * mm, "end": v(-283.95, -194.96) * mm});
            skLineSegment(sketch, "E705", {"start": v(-283.95, -194.96) * mm, "end": v(-280.78, -193.1) * mm});
            skLineSegment(sketch, "E706", {"start": v(-280.78, -193.1) * mm, "end": v(-278.04, -191.34) * mm});
            skLineSegment(sketch, "E707", {"start": v(-278.04, -191.34) * mm, "end": v(-275.72, -189.7) * mm});
            skLineSegment(sketch, "E708", {"start": v(-275.72, -189.7) * mm, "end": v(-273.79, -188.23) * mm});
            skLineSegment(sketch, "E709", {"start": v(-273.79, -188.23) * mm, "end": v(-272.24, -186.93) * mm});
            skLineSegment(sketch, "E710", {"start": v(-272.24, -186.93) * mm, "end": v(-271.05, -185.85) * mm});
            skLineSegment(sketch, "E711", {"start": v(-271.05, -185.85) * mm, "end": v(-270.6, -185.41) * mm});
            skLineSegment(sketch, "E712", {"start": v(-270.6, -185.41) * mm, "end": v(-269.14, -184.11) * mm});
            skLineSegment(sketch, "E713", {"start": v(-269.14, -184.11) * mm, "end": v(-267.84, -183.25) * mm});
            skLineSegment(sketch, "E714", {"start": v(-267.84, -183.25) * mm, "end": v(-266.74, -182.81) * mm});
            skLineSegment(sketch, "E715", {"start": v(-266.74, -182.81) * mm, "end": v(-265.86, -182.78) * mm});
            skLineSegment(sketch, "E716", {"start": v(-265.86, -182.78) * mm, "end": v(-265.25, -183.13) * mm});
            skLineSegment(sketch, "E717", {"start": v(-265.25, -183.13) * mm, "end": v(-263.83, -184.26) * mm});
            skLineSegment(sketch, "E718", {"start": v(-263.83, -184.26) * mm, "end": v(-256, -189.95) * mm});
            skLineSegment(sketch, "E719", {"start": v(-256, -189.95) * mm, "end": v(-254.48, -190.96) * mm});
            skLineSegment(sketch, "E720", {"start": v(-254.48, -190.96) * mm, "end": v(-253.96, -191.43) * mm});
            skLineSegment(sketch, "E721", {"start": v(-253.96, -191.43) * mm, "end": v(-253.72, -192.27) * mm});
            skLineSegment(sketch, "E722", {"start": v(-253.72, -192.27) * mm, "end": v(-253.8, -193.45) * mm});
            skLineSegment(sketch, "E723", {"start": v(-253.8, -193.45) * mm, "end": v(-254.22, -194.96) * mm});
            skLineSegment(sketch, "E724", {"start": v(-254.22, -194.96) * mm, "end": v(-255, -196.75) * mm});
            skLineSegment(sketch, "E725", {"start": v(-255, -196.75) * mm, "end": v(-255.28, -197.3) * mm});
            skLineSegment(sketch, "E726", {"start": v(-255.28, -197.3) * mm, "end": v(-255.94, -198.77) * mm});
            skLineSegment(sketch, "E727", {"start": v(-255.94, -198.77) * mm, "end": v(-256.7, -200.65) * mm});
            skLineSegment(sketch, "E728", {"start": v(-256.7, -200.65) * mm, "end": v(-257.5, -202.94) * mm});
            skLineSegment(sketch, "E729", {"start": v(-257.5, -202.94) * mm, "end": v(-258.34, -205.66) * mm});
            skLineSegment(sketch, "E730", {"start": v(-258.34, -205.66) * mm, "end": v(-259.17, -208.8) * mm});
            skLineSegment(sketch, "E731", {"start": v(-259.17, -208.8) * mm, "end": v(-259.95, -212.39) * mm});
            skLineSegment(sketch, "E732", {"start": v(-259.95, -212.39) * mm, "end": v(-260.66, -216.4) * mm});
            skLineSegment(sketch, "E733", {"start": v(-260.66, -216.4) * mm, "end": v(-261.24, -220.86) * mm});
            skLineSegment(sketch, "E734", {"start": v(-261.24, -220.86) * mm, "end": v(-261.66, -225.5) * mm});
            skLineSegment(sketch, "E735", {"start": v(-261.66, -225.5) * mm, "end": v(-256.21, -229.04) * mm});
            skLineSegment(sketch, "E736", {"start": v(-256.21, -229.04) * mm, "end": v(-250.43, -232) * mm});
            skLineSegment(sketch, "E737", {"start": v(-250.43, -232) * mm, "end": v(-246.6, -229.3) * mm});
            skLineSegment(sketch, "E738", {"start": v(-246.6, -229.3) * mm, "end": v(-243.05, -226.57) * mm});
            skLineSegment(sketch, "E739", {"start": v(-243.05, -226.57) * mm, "end": v(-239.92, -223.96) * mm});
            skLineSegment(sketch, "E740", {"start": v(-239.92, -223.96) * mm, "end": v(-237.2, -221.49) * mm});
            skLineSegment(sketch, "E741", {"start": v(-237.2, -221.49) * mm, "end": v(-234.9, -219.2) * mm});
            skLineSegment(sketch, "E742", {"start": v(-234.9, -219.2) * mm, "end": v(-232.96, -217.11) * mm});
            skLineSegment(sketch, "E743", {"start": v(-232.96, -217.11) * mm, "end": v(-231.38, -215.26) * mm});
            skLineSegment(sketch, "E744", {"start": v(-231.38, -215.26) * mm, "end": v(-230.13, -213.67) * mm});
            skLineSegment(sketch, "E745", {"start": v(-230.13, -213.67) * mm, "end": v(-229.2, -212.36) * mm});
            skLineSegment(sketch, "E746", {"start": v(-229.2, -212.36) * mm, "end": v(-228.85, -211.85) * mm});
            skLineSegment(sketch, "E747", {"start": v(-228.85, -211.85) * mm, "end": v(-227.7, -210.27) * mm});
            skLineSegment(sketch, "E748", {"start": v(-227.7, -210.27) * mm, "end": v(-226.6, -209.16) * mm});
            skLineSegment(sketch, "E749", {"start": v(-226.6, -209.16) * mm, "end": v(-225.6, -208.5) * mm});
            skLineSegment(sketch, "E750", {"start": v(-225.6, -208.5) * mm, "end": v(-224.76, -208.29) * mm});
            skLineSegment(sketch, "E751", {"start": v(-224.76, -208.29) * mm, "end": v(-224.1, -208.5) * mm});
            skLineSegment(sketch, "E752", {"start": v(-224.1, -208.5) * mm, "end": v(-222.47, -209.3) * mm});
            skLineSegment(sketch, "E753", {"start": v(-222.47, -209.3) * mm, "end": v(-213.62, -213.25) * mm});
            skLineSegment(sketch, "E754", {"start": v(-213.62, -213.25) * mm, "end": v(-211.93, -213.92) * mm});
            skLineSegment(sketch, "E755", {"start": v(-211.93, -213.92) * mm, "end": v(-211.32, -214.27) * mm});
            skLineSegment(sketch, "E756", {"start": v(-211.32, -214.27) * mm, "end": v(-210.91, -215.04) * mm});
            skLineSegment(sketch, "E757", {"start": v(-210.91, -215.04) * mm, "end": v(-210.74, -216.22) * mm});
            skLineSegment(sketch, "E758", {"start": v(-210.74, -216.22) * mm, "end": v(-210.84, -217.77) * mm});
            skLineSegment(sketch, "E759", {"start": v(-210.84, -217.77) * mm, "end": v(-211.23, -219.7) * mm});
            skLineSegment(sketch, "E760", {"start": v(-211.23, -219.7) * mm, "end": v(-211.39, -220.3) * mm});
            skLineSegment(sketch, "E761", {"start": v(-211.39, -220.3) * mm, "end": v(-211.73, -221.86) * mm});
            skLineSegment(sketch, "E762", {"start": v(-211.73, -221.86) * mm, "end": v(-212.08, -223.85) * mm});
            skLineSegment(sketch, "E763", {"start": v(-212.08, -223.85) * mm, "end": v(-212.4, -226.27) * mm});
            skLineSegment(sketch, "E764", {"start": v(-212.4, -226.27) * mm, "end": v(-212.65, -229.1) * mm});
            skLineSegment(sketch, "E765", {"start": v(-212.65, -229.1) * mm, "end": v(-212.8, -232.35) * mm});
            skLineSegment(sketch, "E766", {"start": v(-212.8, -232.35) * mm, "end": v(-212.82, -236.02) * mm});
            skLineSegment(sketch, "E767", {"start": v(-212.82, -236.02) * mm, "end": v(-212.68, -240.1) * mm});
            skLineSegment(sketch, "E768", {"start": v(-212.68, -240.1) * mm, "end": v(-212.32, -244.57) * mm});
            skLineSegment(sketch, "E769", {"start": v(-212.32, -244.57) * mm, "end": v(-211.77, -249.2) * mm});
            skLineSegment(sketch, "E770", {"start": v(-211.77, -249.2) * mm, "end": v(-205.7, -251.53) * mm});
            skLineSegment(sketch, "E771", {"start": v(-205.7, -251.53) * mm, "end": v(-199.43, -253.21) * mm});
            skLineSegment(sketch, "E772", {"start": v(-199.43, -253.21) * mm, "end": v(-196.25, -249.8) * mm});
            skLineSegment(sketch, "E773", {"start": v(-196.25, -249.8) * mm, "end": v(-193.34, -246.38) * mm});
            skLineSegment(sketch, "E774", {"start": v(-193.34, -246.38) * mm, "end": v(-190.82, -243.17) * mm});
            skLineSegment(sketch, "E775", {"start": v(-190.82, -243.17) * mm, "end": v(-188.68, -240.19) * mm});
            skLineSegment(sketch, "E776", {"start": v(-188.68, -240.19) * mm, "end": v(-186.9, -237.47) * mm});
            skLineSegment(sketch, "E777", {"start": v(-186.9, -237.47) * mm, "end": v(-185.44, -235.03) * mm});
            skLineSegment(sketch, "E778", {"start": v(-185.44, -235.03) * mm, "end": v(-184.28, -232.89) * mm});
            skLineSegment(sketch, "E779", {"start": v(-184.28, -232.89) * mm, "end": v(-183.39, -231.07) * mm});
            skLineSegment(sketch, "E780", {"start": v(-183.39, -231.07) * mm, "end": v(-182.74, -229.6) * mm});
            skLineSegment(sketch, "E781", {"start": v(-182.74, -229.6) * mm, "end": v(-182.52, -229.02) * mm});
            skLineSegment(sketch, "E782", {"start": v(-182.52, -229.02) * mm, "end": v(-181.7, -227.24) * mm});
            skLineSegment(sketch, "E783", {"start": v(-181.7, -227.24) * mm, "end": v(-180.87, -225.92) * mm});
            skLineSegment(sketch, "E784", {"start": v(-180.87, -225.92) * mm, "end": v(-180.04, -225.08) * mm});
            skLineSegment(sketch, "E785", {"start": v(-180.04, -225.08) * mm, "end": v(-179.25, -224.7) * mm});
            skLineSegment(sketch, "E786", {"start": v(-179.25, -224.7) * mm, "end": v(-178.56, -224.76) * mm});
            skLineSegment(sketch, "E787", {"start": v(-178.56, -224.76) * mm, "end": v(-176.8, -225.21) * mm});
            skLineSegment(sketch, "E788", {"start": v(-176.8, -225.21) * mm, "end": v(-167.32, -227.23) * mm});
            skLineSegment(sketch, "E789", {"start": v(-167.32, -227.23) * mm, "end": v(-165.53, -227.53) * mm});
            skLineSegment(sketch, "E790", {"start": v(-165.53, -227.53) * mm, "end": v(-164.86, -227.75) * mm});
            skLineSegment(sketch, "E791", {"start": v(-164.86, -227.75) * mm, "end": v(-164.3, -228.42) * mm});
            skLineSegment(sketch, "E792", {"start": v(-164.3, -228.42) * mm, "end": v(-163.9, -229.53) * mm});
            skLineSegment(sketch, "E793", {"start": v(-163.9, -229.53) * mm, "end": v(-163.66, -231.08) * mm});
            skLineSegment(sketch, "E794", {"start": v(-163.66, -231.08) * mm, "end": v(-163.65, -233.03) * mm});
            skLineSegment(sketch, "E795", {"start": v(-163.65, -233.03) * mm, "end": v(-163.67, -233.65) * mm});
            skLineSegment(sketch, "E796", {"start": v(-163.67, -233.65) * mm, "end": v(-163.68, -235.26) * mm});
            skLineSegment(sketch, "E797", {"start": v(-163.68, -235.26) * mm, "end": v(-163.6, -237.28) * mm});
            skLineSegment(sketch, "E798", {"start": v(-163.6, -237.28) * mm, "end": v(-163.42, -239.7) * mm});
            skLineSegment(sketch, "E799", {"start": v(-163.42, -239.7) * mm, "end": v(-163.08, -242.53) * mm});
            skLineSegment(sketch, "E800", {"start": v(-163.08, -242.53) * mm, "end": v(-162.55, -245.74) * mm});
            skLineSegment(sketch, "E801", {"start": v(-162.55, -245.74) * mm, "end": v(-161.81, -249.33) * mm});
            skLineSegment(sketch, "E802", {"start": v(-161.81, -249.33) * mm, "end": v(-160.82, -253.29) * mm});
            skLineSegment(sketch, "E803", {"start": v(-160.82, -253.29) * mm, "end": v(-159.55, -257.6) * mm});
            skLineSegment(sketch, "E804", {"start": v(-159.55, -257.6) * mm, "end": v(-158.03, -262.01) * mm});
            skLineSegment(sketch, "E805", {"start": v(-158.03, -262.01) * mm, "end": v(-151.62, -263.03) * mm});
            skLineSegment(sketch, "E806", {"start": v(-151.62, -263.03) * mm, "end": v(-145.13, -263.37) * mm});
            skLineSegment(sketch, "E807", {"start": v(-145.13, -263.37) * mm, "end": v(-142.74, -259.36) * mm});
            skLineSegment(sketch, "E808", {"start": v(-142.74, -259.36) * mm, "end": v(-140.6, -255.42) * mm});
            skLineSegment(sketch, "E809", {"start": v(-140.6, -255.42) * mm, "end": v(-138.8, -251.75) * mm});
            skLineSegment(sketch, "E810", {"start": v(-138.8, -251.75) * mm, "end": v(-137.33, -248.4) * mm});
            skLineSegment(sketch, "E811", {"start": v(-137.33, -248.4) * mm, "end": v(-136.15, -245.36) * mm});
            skLineSegment(sketch, "E812", {"start": v(-136.15, -245.36) * mm, "end": v(-135.23, -242.67) * mm});
            skLineSegment(sketch, "E813", {"start": v(-135.23, -242.67) * mm, "end": v(-134.54, -240.34) * mm});
            skLineSegment(sketch, "E814", {"start": v(-134.54, -240.34) * mm, "end": v(-134.05, -238.38) * mm});
            skLineSegment(sketch, "E815", {"start": v(-134.05, -238.38) * mm, "end": v(-133.72, -236.8) * mm});
            skLineSegment(sketch, "E816", {"start": v(-133.72, -236.8) * mm, "end": v(-133.62, -236.2) * mm});
            skLineSegment(sketch, "E817", {"start": v(-133.62, -236.2) * mm, "end": v(-133.2, -234.28) * mm});
            skLineSegment(sketch, "E818", {"start": v(-133.2, -234.28) * mm, "end": v(-132.65, -232.82) * mm});
            skLineSegment(sketch, "E819", {"start": v(-132.65, -232.82) * mm, "end": v(-132.02, -231.81) * mm});
            skLineSegment(sketch, "E820", {"start": v(-132.02, -231.81) * mm, "end": v(-131.33, -231.27) * mm});
            skLineSegment(sketch, "E821", {"start": v(-131.33, -231.27) * mm, "end": v(-130.63, -231.2) * mm});
            skLineSegment(sketch, "E822", {"start": v(-130.63, -231.2) * mm, "end": v(-128.82, -231.27) * mm});
            skLineSegment(sketch, "E823", {"start": v(-128.82, -231.27) * mm, "end": v(-119.13, -231.27) * mm});
            skLineSegment(sketch, "E824", {"start": v(-119.13, -231.27) * mm, "end": v(-117.32, -231.2) * mm});
            skLineSegment(sketch, "E825", {"start": v(-117.32, -231.2) * mm, "end": v(-116.62, -231.27) * mm});
            skLineSegment(sketch, "E826", {"start": v(-116.62, -231.27) * mm, "end": v(-115.93, -231.81) * mm});
            skLineSegment(sketch, "E827", {"start": v(-115.93, -231.81) * mm, "end": v(-115.3, -232.82) * mm});
            skLineSegment(sketch, "E828", {"start": v(-115.3, -232.82) * mm, "end": v(-114.75, -234.28) * mm});
            skLineSegment(sketch, "E829", {"start": v(-114.75, -234.28) * mm, "end": v(-114.33, -236.2) * mm});
            skLineSegment(sketch, "E830", {"start": v(-114.33, -236.2) * mm, "end": v(-114.23, -236.8) * mm});
            skLineSegment(sketch, "E831", {"start": v(-114.23, -236.8) * mm, "end": v(-113.9, -238.38) * mm});
            skLineSegment(sketch, "E832", {"start": v(-113.9, -238.38) * mm, "end": v(-113.41, -240.34) * mm});
            skLineSegment(sketch, "E833", {"start": v(-113.41, -240.34) * mm, "end": v(-112.72, -242.67) * mm});
            skLineSegment(sketch, "E834", {"start": v(-112.72, -242.67) * mm, "end": v(-111.8, -245.36) * mm});
            skLineSegment(sketch, "E835", {"start": v(-111.8, -245.36) * mm, "end": v(-110.62, -248.4) * mm});
            skLineSegment(sketch, "E836", {"start": v(-110.62, -248.4) * mm, "end": v(-109.15, -251.75) * mm});
            skLineSegment(sketch, "E837", {"start": v(-109.15, -251.75) * mm, "end": v(-107.35, -255.42) * mm});
            skLineSegment(sketch, "E838", {"start": v(-107.35, -255.42) * mm, "end": v(-105.21, -259.36) * mm});
            skLineSegment(sketch, "E839", {"start": v(-105.21, -259.36) * mm, "end": v(-102.81, -263.37) * mm});
            skLineSegment(sketch, "E840", {"start": v(-102.81, -263.37) * mm, "end": v(-96.33, -263.03) * mm});
            skLineSegment(sketch, "E841", {"start": v(-96.33, -263.03) * mm, "end": v(-89.91, -262.01) * mm});
            skLineSegment(sketch, "E842", {"start": v(-89.91, -262.01) * mm, "end": v(-88.4, -257.6) * mm});
            skLineSegment(sketch, "E843", {"start": v(-88.4, -257.6) * mm, "end": v(-87.13, -253.29) * mm});
            skLineSegment(sketch, "E844", {"start": v(-87.13, -253.29) * mm, "end": v(-86.14, -249.33) * mm});
            skLineSegment(sketch, "E845", {"start": v(-86.14, -249.33) * mm, "end": v(-85.4, -245.74) * mm});
            skLineSegment(sketch, "E846", {"start": v(-85.4, -245.74) * mm, "end": v(-84.87, -242.53) * mm});
            skLineSegment(sketch, "E847", {"start": v(-84.87, -242.53) * mm, "end": v(-84.53, -239.7) * mm});
            skLineSegment(sketch, "E848", {"start": v(-84.53, -239.7) * mm, "end": v(-84.34, -237.28) * mm});
            skLineSegment(sketch, "E849", {"start": v(-84.34, -237.28) * mm, "end": v(-84.26, -235.26) * mm});
            skLineSegment(sketch, "E850", {"start": v(-84.26, -235.26) * mm, "end": v(-84.27, -233.65) * mm});
            skLineSegment(sketch, "E851", {"start": v(-84.27, -233.65) * mm, "end": v(-84.3, -233.03) * mm});
            skLineSegment(sketch, "E852", {"start": v(-84.3, -233.03) * mm, "end": v(-84.29, -231.08) * mm});
            skLineSegment(sketch, "E853", {"start": v(-84.29, -231.08) * mm, "end": v(-84.06, -229.53) * mm});
            skLineSegment(sketch, "E854", {"start": v(-84.06, -229.53) * mm, "end": v(-83.64, -228.42) * mm});
            skLineSegment(sketch, "E855", {"start": v(-83.64, -228.42) * mm, "end": v(-83.09, -227.75) * mm});
            skLineSegment(sketch, "E856", {"start": v(-83.09, -227.75) * mm, "end": v(-82.42, -227.53) * mm});
            skLineSegment(sketch, "E857", {"start": v(-82.42, -227.53) * mm, "end": v(-80.63, -227.23) * mm});
            skLineSegment(sketch, "E858", {"start": v(-80.63, -227.23) * mm, "end": v(-71.15, -225.21) * mm});
            skLineSegment(sketch, "E859", {"start": v(-71.15, -225.21) * mm, "end": v(-69.4, -224.76) * mm});
            skLineSegment(sketch, "E860", {"start": v(-69.4, -224.76) * mm, "end": v(-68.7, -224.7) * mm});
            skLineSegment(sketch, "E861", {"start": v(-68.7, -224.7) * mm, "end": v(-67.91, -225.08) * mm});
            skLineSegment(sketch, "E862", {"start": v(-67.91, -225.08) * mm, "end": v(-67.08, -225.92) * mm});
            skLineSegment(sketch, "E863", {"start": v(-67.08, -225.92) * mm, "end": v(-66.24, -227.24) * mm});
            skLineSegment(sketch, "E864", {"start": v(-66.24, -227.24) * mm, "end": v(-65.43, -229.02) * mm});
            skLineSegment(sketch, "E865", {"start": v(-65.43, -229.02) * mm, "end": v(-65.2, -229.6) * mm});
            skLineSegment(sketch, "E866", {"start": v(-65.2, -229.6) * mm, "end": v(-64.56, -231.07) * mm});
            skLineSegment(sketch, "E867", {"start": v(-64.56, -231.07) * mm, "end": v(-63.67, -232.89) * mm});
            skLineSegment(sketch, "E868", {"start": v(-63.67, -232.89) * mm, "end": v(-62.51, -235.03) * mm});
            skLineSegment(sketch, "E869", {"start": v(-62.51, -235.03) * mm, "end": v(-61.05, -237.47) * mm});
            skLineSegment(sketch, "E870", {"start": v(-61.05, -237.47) * mm, "end": v(-59.27, -240.19) * mm});
            skLineSegment(sketch, "E871", {"start": v(-59.27, -240.19) * mm, "end": v(-57.13, -243.17) * mm});
            skLineSegment(sketch, "E872", {"start": v(-57.13, -243.17) * mm, "end": v(-54.61, -246.38) * mm});
            skLineSegment(sketch, "E873", {"start": v(-54.61, -246.38) * mm, "end": v(-51.7, -249.8) * mm});
            skLineSegment(sketch, "E874", {"start": v(-51.7, -249.8) * mm, "end": v(-48.52, -253.21) * mm});
            skLineSegment(sketch, "E875", {"start": v(-48.52, -253.21) * mm, "end": v(-42.25, -251.53) * mm});
            skLineSegment(sketch, "E876", {"start": v(-42.25, -251.53) * mm, "end": v(-36.18, -249.2) * mm});
            skLineSegment(sketch, "E877", {"start": v(-36.18, -249.2) * mm, "end": v(-35.62, -244.57) * mm});
            skLineSegment(sketch, "E878", {"start": v(-35.62, -244.57) * mm, "end": v(-35.27, -240.1) * mm});
            skLineSegment(sketch, "E879", {"start": v(-35.27, -240.1) * mm, "end": v(-35.12, -236.02) * mm});
            skLineSegment(sketch, "E880", {"start": v(-35.12, -236.02) * mm, "end": v(-35.14, -232.35) * mm});
            skLineSegment(sketch, "E881", {"start": v(-35.14, -232.35) * mm, "end": v(-35.3, -229.1) * mm});
            skLineSegment(sketch, "E882", {"start": v(-35.3, -229.1) * mm, "end": v(-35.55, -226.27) * mm});
            skLineSegment(sketch, "E883", {"start": v(-35.55, -226.27) * mm, "end": v(-35.87, -223.85) * mm});
            skLineSegment(sketch, "E884", {"start": v(-35.87, -223.85) * mm, "end": v(-36.22, -221.86) * mm});
            skLineSegment(sketch, "E885", {"start": v(-36.22, -221.86) * mm, "end": v(-36.56, -220.3) * mm});
            skLineSegment(sketch, "E886", {"start": v(-36.56, -220.3) * mm, "end": v(-36.72, -219.7) * mm});
            skLineSegment(sketch, "E887", {"start": v(-36.72, -219.7) * mm, "end": v(-37.11, -217.77) * mm});
            skLineSegment(sketch, "E888", {"start": v(-37.11, -217.77) * mm, "end": v(-37.2, -216.22) * mm});
            skLineSegment(sketch, "E889", {"start": v(-37.2, -216.22) * mm, "end": v(-37.03, -215.04) * mm});
            skLineSegment(sketch, "E890", {"start": v(-37.03, -215.04) * mm, "end": v(-36.63, -214.27) * mm});
            skLineSegment(sketch, "E891", {"start": v(-36.63, -214.27) * mm, "end": v(-36.02, -213.92) * mm});
            skLineSegment(sketch, "E892", {"start": v(-36.02, -213.92) * mm, "end": v(-34.33, -213.25) * mm});
            skLineSegment(sketch, "E893", {"start": v(-34.33, -213.25) * mm, "end": v(-25.48, -209.3) * mm});
            skLineSegment(sketch, "E894", {"start": v(-25.48, -209.3) * mm, "end": v(-23.86, -208.5) * mm});
            skLineSegment(sketch, "E895", {"start": v(-23.86, -208.5) * mm, "end": v(-23.19, -208.29) * mm});
            skLineSegment(sketch, "E896", {"start": v(-23.19, -208.29) * mm, "end": v(-22.34, -208.5) * mm});
            skLineSegment(sketch, "E897", {"start": v(-22.34, -208.5) * mm, "end": v(-21.35, -209.16) * mm});
            skLineSegment(sketch, "E898", {"start": v(-21.35, -209.16) * mm, "end": v(-20.26, -210.27) * mm});
            skLineSegment(sketch, "E899", {"start": v(-20.26, -210.27) * mm, "end": v(-19.1, -211.85) * mm});
            skLineSegment(sketch, "E900", {"start": v(-19.1, -211.85) * mm, "end": v(-18.75, -212.36) * mm});
            skLineSegment(sketch, "E901", {"start": v(-18.75, -212.36) * mm, "end": v(-17.82, -213.67) * mm});
            skLineSegment(sketch, "E902", {"start": v(-17.82, -213.67) * mm, "end": v(-16.57, -215.26) * mm});
            skLineSegment(sketch, "E903", {"start": v(-16.57, -215.26) * mm, "end": v(-15, -217.11) * mm});
            skLineSegment(sketch, "E904", {"start": v(-15, -217.11) * mm, "end": v(-13.06, -219.2) * mm});
            skLineSegment(sketch, "E905", {"start": v(-13.06, -219.2) * mm, "end": v(-10.74, -221.49) * mm});
            skLineSegment(sketch, "E906", {"start": v(-10.74, -221.49) * mm, "end": v(-8.03, -223.96) * mm});
            skLineSegment(sketch, "E907", {"start": v(-8.03, -223.96) * mm, "end": v(-4.9, -226.57) * mm});
            skLineSegment(sketch, "E908", {"start": v(-4.9, -226.57) * mm, "end": v(-1.34, -229.3) * mm});
            skLineSegment(sketch, "E909", {"start": v(-1.34, -229.3) * mm, "end": v(2.48, -232) * mm});
            skLineSegment(sketch, "E910", {"start": v(2.48, -232) * mm, "end": v(8.26, -229.04) * mm});
            skLineSegment(sketch, "E911", {"start": v(8.26, -229.04) * mm, "end": v(13.71, -225.5) * mm});
            skLineSegment(sketch, "E912", {"start": v(13.71, -225.5) * mm, "end": v(13.3, -220.86) * mm});
            skLineSegment(sketch, "E913", {"start": v(13.3, -220.86) * mm, "end": v(12.7, -216.4) * mm});
            skLineSegment(sketch, "E914", {"start": v(12.7, -216.4) * mm, "end": v(12, -212.39) * mm});
            skLineSegment(sketch, "E915", {"start": v(12, -212.39) * mm, "end": v(11.22, -208.8) * mm});
            skLineSegment(sketch, "E916", {"start": v(11.22, -208.8) * mm, "end": v(10.4, -205.66) * mm});
            skLineSegment(sketch, "E917", {"start": v(10.4, -205.66) * mm, "end": v(9.56, -202.94) * mm});
            skLineSegment(sketch, "E918", {"start": v(9.56, -202.94) * mm, "end": v(8.75, -200.65) * mm});
            skLineSegment(sketch, "E919", {"start": v(8.75, -200.65) * mm, "end": v(8, -198.77) * mm});
            skLineSegment(sketch, "E920", {"start": v(8, -198.77) * mm, "end": v(7.33, -197.3) * mm});
            skLineSegment(sketch, "E921", {"start": v(7.33, -197.3) * mm, "end": v(7.05, -196.75) * mm});
            skLineSegment(sketch, "E922", {"start": v(7.05, -196.75) * mm, "end": v(6.27, -194.96) * mm});
            skLineSegment(sketch, "E923", {"start": v(6.27, -194.96) * mm, "end": v(5.85, -193.45) * mm});
            skLineSegment(sketch, "E924", {"start": v(5.85, -193.45) * mm, "end": v(5.78, -192.27) * mm});
            skLineSegment(sketch, "E925", {"start": v(5.78, -192.27) * mm, "end": v(6.01, -191.43) * mm});
            skLineSegment(sketch, "E926", {"start": v(6.01, -191.43) * mm, "end": v(6.53, -190.96) * mm});
            skLineSegment(sketch, "E927", {"start": v(6.53, -190.96) * mm, "end": v(8.05, -189.95) * mm});
            skLineSegment(sketch, "E928", {"start": v(8.05, -189.95) * mm, "end": v(15.88, -184.26) * mm});
            skLineSegment(sketch, "E929", {"start": v(15.88, -184.26) * mm, "end": v(17.3, -183.13) * mm});
            skLineSegment(sketch, "E930", {"start": v(17.3, -183.13) * mm, "end": v(17.92, -182.78) * mm});
            skLineSegment(sketch, "E931", {"start": v(17.92, -182.78) * mm, "end": v(18.79, -182.81) * mm});
            skLineSegment(sketch, "E932", {"start": v(18.79, -182.81) * mm, "end": v(19.9, -183.25) * mm});
            skLineSegment(sketch, "E933", {"start": v(19.9, -183.25) * mm, "end": v(21.2, -184.11) * mm});
            skLineSegment(sketch, "E934", {"start": v(21.2, -184.11) * mm, "end": v(22.66, -185.41) * mm});
            skLineSegment(sketch, "E935", {"start": v(22.66, -185.41) * mm, "end": v(23.1, -185.85) * mm});
            skLineSegment(sketch, "E936", {"start": v(23.1, -185.85) * mm, "end": v(24.29, -186.93) * mm});
            skLineSegment(sketch, "E937", {"start": v(24.29, -186.93) * mm, "end": v(25.84, -188.23) * mm});
            skLineSegment(sketch, "E938", {"start": v(25.84, -188.23) * mm, "end": v(27.77, -189.7) * mm});
            skLineSegment(sketch, "E939", {"start": v(27.77, -189.7) * mm, "end": v(30.1, -191.34) * mm});
            skLineSegment(sketch, "E940", {"start": v(30.1, -191.34) * mm, "end": v(32.83, -193.1) * mm});
            skLineSegment(sketch, "E941", {"start": v(32.83, -193.1) * mm, "end": v(36, -194.96) * mm});
            skLineSegment(sketch, "E942", {"start": v(36, -194.96) * mm, "end": v(39.6, -196.87) * mm});
            skLineSegment(sketch, "E943", {"start": v(39.6, -196.87) * mm, "end": v(43.66, -198.8) * mm});
            skLineSegment(sketch, "E944", {"start": v(43.66, -198.8) * mm, "end": v(47.95, -200.63) * mm});
            skLineSegment(sketch, "E945", {"start": v(47.95, -200.63) * mm, "end": v(53, -196.55) * mm});
            skLineSegment(sketch, "E946", {"start": v(53, -196.55) * mm, "end": v(57.59, -191.95) * mm});
            skLineSegment(sketch, "E947", {"start": v(57.59, -191.95) * mm, "end": v(56.21, -187.5) * mm});
            skLineSegment(sketch, "E948", {"start": v(56.21, -187.5) * mm, "end": v(54.71, -183.26) * mm});
            skLineSegment(sketch, "E949", {"start": v(54.71, -183.26) * mm, "end": v(53.2, -179.47) * mm});
            skLineSegment(sketch, "E950", {"start": v(53.2, -179.47) * mm, "end": v(51.68, -176.13) * mm});
            skLineSegment(sketch, "E951", {"start": v(51.68, -176.13) * mm, "end": v(50.22, -173.22) * mm});
            skLineSegment(sketch, "E952", {"start": v(50.22, -173.22) * mm, "end": v(48.83, -170.74) * mm});
            skLineSegment(sketch, "E953", {"start": v(48.83, -170.74) * mm, "end": v(47.56, -168.67) * mm});
            skLineSegment(sketch, "E954", {"start": v(47.56, -168.67) * mm, "end": v(46.43, -167) * mm});
            skLineSegment(sketch, "E955", {"start": v(46.43, -167) * mm, "end": v(45.48, -165.7) * mm});
            skLineSegment(sketch, "E956", {"start": v(45.48, -165.7) * mm, "end": v(45.1, -165.21) * mm});
            skLineSegment(sketch, "E957", {"start": v(45.1, -165.21) * mm, "end": v(43.96, -163.62) * mm});
            skLineSegment(sketch, "E958", {"start": v(43.96, -163.62) * mm, "end": v(43.24, -162.23) * mm});
            skLineSegment(sketch, "E959", {"start": v(43.24, -162.23) * mm, "end": v(42.92, -161.1) * mm});
            skLineSegment(sketch, "E960", {"start": v(42.92, -161.1) * mm, "end": v(42.97, -160.22) * mm});
            skLineSegment(sketch, "E961", {"start": v(42.97, -160.22) * mm, "end": v(43.38, -159.65) * mm});
            skLineSegment(sketch, "E962", {"start": v(43.38, -159.65) * mm, "end": v(44.65, -158.35) * mm});
            skLineSegment(sketch, "E963", {"start": v(44.65, -158.35) * mm, "end": v(51.14, -151.15) * mm});
            skLineSegment(sketch, "E964", {"start": v(51.14, -151.15) * mm, "end": v(52.3, -149.75) * mm});
            skLineSegment(sketch, "E965", {"start": v(52.3, -149.75) * mm, "end": v(52.82, -149.29) * mm});
            skLineSegment(sketch, "E966", {"start": v(52.82, -149.29) * mm, "end": v(53.68, -149.14) * mm});
            skLineSegment(sketch, "E967", {"start": v(53.68, -149.14) * mm, "end": v(54.85, -149.34) * mm});
            skLineSegment(sketch, "E968", {"start": v(54.85, -149.34) * mm, "end": v(56.3, -149.9) * mm});
            skLineSegment(sketch, "E969", {"start": v(56.3, -149.9) * mm, "end": v(58, -150.87) * mm});
            skLineSegment(sketch, "E970", {"start": v(58, -150.87) * mm, "end": v(58.53, -151.2) * mm});
            skLineSegment(sketch, "E971", {"start": v(58.53, -151.2) * mm, "end": v(59.91, -152.02) * mm});
            skLineSegment(sketch, "E972", {"start": v(59.91, -152.02) * mm, "end": v(61.7, -152.97) * mm});
            skLineSegment(sketch, "E973", {"start": v(61.7, -152.97) * mm, "end": v(63.9, -154.01) * mm});
            skLineSegment(sketch, "E974", {"start": v(63.9, -154.01) * mm, "end": v(66.5, -155.13) * mm});
            skLineSegment(sketch, "E975", {"start": v(66.5, -155.13) * mm, "end": v(69.55, -156.28) * mm});
            skLineSegment(sketch, "E976", {"start": v(69.55, -156.28) * mm, "end": v(73.04, -157.43) * mm});
            skLineSegment(sketch, "E977", {"start": v(73.04, -157.43) * mm, "end": v(76.96, -158.55) * mm});
            skLineSegment(sketch, "E978", {"start": v(76.96, -158.55) * mm, "end": v(81.33, -159.6) * mm});
            skLineSegment(sketch, "E979", {"start": v(81.33, -159.6) * mm, "end": v(85.9, -160.5) * mm});
            skLineSegment(sketch, "E980", {"start": v(85.9, -160.5) * mm, "end": v(90, -155.46) * mm});
            skLineSegment(sketch, "E981", {"start": v(90, -155.46) * mm, "end": v(93.53, -150) * mm});
            skLineSegment(sketch, "E982", {"start": v(93.53, -150) * mm, "end": v(91.26, -145.93) * mm});
            skLineSegment(sketch, "E983", {"start": v(91.26, -145.93) * mm, "end": v(88.91, -142.1) * mm});
            skLineSegment(sketch, "E984", {"start": v(88.91, -142.1) * mm, "end": v(86.64, -138.72) * mm});
            skLineSegment(sketch, "E985", {"start": v(86.64, -138.72) * mm, "end": v(84.46, -135.76) * mm});
            skLineSegment(sketch, "E986", {"start": v(84.46, -135.76) * mm, "end": v(82.43, -133.22) * mm});
            skLineSegment(sketch, "E987", {"start": v(82.43, -133.22) * mm, "end": v(80.56, -131.08) * mm});
            skLineSegment(sketch, "E988", {"start": v(80.56, -131.08) * mm, "end": v(78.88, -129.32) * mm});
            skLineSegment(sketch, "E989", {"start": v(78.88, -129.32) * mm, "end": v(77.43, -127.91) * mm});
            skLineSegment(sketch, "E990", {"start": v(77.43, -127.91) * mm, "end": v(76.23, -126.84) * mm});
            skLineSegment(sketch, "E991", {"start": v(76.23, -126.84) * mm, "end": v(75.75, -126.45) * mm});
            skLineSegment(sketch, "E992", {"start": v(75.75, -126.45) * mm, "end": v(74.3, -125.13) * mm});
            skLineSegment(sketch, "E993", {"start": v(74.3, -125.13) * mm, "end": v(73.31, -123.92) * mm});
            skLineSegment(sketch, "E994", {"start": v(73.31, -123.92) * mm, "end": v(72.76, -122.87) * mm});
            skLineSegment(sketch, "E995", {"start": v(72.76, -122.87) * mm, "end": v(72.64, -122) * mm});
            skLineSegment(sketch, "E996", {"start": v(72.64, -122) * mm, "end": v(72.92, -121.36) * mm});
            skLineSegment(sketch, "E997", {"start": v(72.92, -121.36) * mm, "end": v(73.9, -119.83) * mm});
            skLineSegment(sketch, "E998", {"start": v(73.9, -119.83) * mm, "end": v(78.74, -111.44) * mm});
            skLineSegment(sketch, "E999", {"start": v(78.74, -111.44) * mm, "end": v(79.58, -109.83) * mm});
            skLineSegment(sketch, "E1000", {"start": v(79.58, -109.83) * mm, "end": v(80, -109.27) * mm});
            skLineSegment(sketch, "E1001", {"start": v(80, -109.27) * mm, "end": v(80.8, -108.94) * mm});
            skLineSegment(sketch, "E1002", {"start": v(80.8, -108.94) * mm, "end": v(81.99, -108.9) * mm});
            skLineSegment(sketch, "E1003", {"start": v(81.99, -108.9) * mm, "end": v(83.53, -109.15) * mm});
            skLineSegment(sketch, "E1004", {"start": v(83.53, -109.15) * mm, "end": v(85.4, -109.74) * mm});
            skLineSegment(sketch, "E1005", {"start": v(85.4, -109.74) * mm, "end": v(85.97, -109.96) * mm});
            skLineSegment(sketch, "E1006", {"start": v(85.97, -109.96) * mm, "end": v(87.5, -110.47) * mm});
            skLineSegment(sketch, "E1007", {"start": v(87.5, -110.47) * mm, "end": v(89.45, -111.02) * mm});
            skLineSegment(sketch, "E1008", {"start": v(89.45, -111.02) * mm, "end": v(91.81, -111.59) * mm});
            skLineSegment(sketch, "E1009", {"start": v(91.81, -111.59) * mm, "end": v(94.6, -112.14) * mm});
            skLineSegment(sketch, "E1010", {"start": v(94.6, -112.14) * mm, "end": v(97.82, -112.63) * mm});
            skLineSegment(sketch, "E1011", {"start": v(97.82, -112.63) * mm, "end": v(101.46, -113.03) * mm});
            skLineSegment(sketch, "E1012", {"start": v(101.46, -113.03) * mm, "end": v(105.53, -113.31) * mm});
            skLineSegment(sketch, "E1013", {"start": v(105.53, -113.31) * mm, "end": v(110.02, -113.43) * mm});
            skLineSegment(sketch, "E1014", {"start": v(110.02, -113.43) * mm, "end": v(114.69, -113.36) * mm});
            skLineSegment(sketch, "E1015", {"start": v(114.69, -113.36) * mm, "end": v(117.64, -107.57) * mm});
            skLineSegment(sketch, "E1016", {"start": v(117.64, -107.57) * mm, "end": v(119.97, -101.5) * mm});
            skLineSegment(sketch, "E1017", {"start": v(119.97, -101.5) * mm, "end": v(116.9, -98) * mm});
            skLineSegment(sketch, "E1018", {"start": v(116.9, -98) * mm, "end": v(113.8, -94.74) * mm});
            skLineSegment(sketch, "E1019", {"start": v(113.8, -94.74) * mm, "end": v(110.87, -91.9) * mm});
            skLineSegment(sketch, "E1020", {"start": v(110.87, -91.9) * mm, "end": v(108.13, -89.46) * mm});
            skLineSegment(sketch, "E1021", {"start": v(108.13, -89.46) * mm, "end": v(105.61, -87.4) * mm});
            skLineSegment(sketch, "E1022", {"start": v(105.61, -87.4) * mm, "end": v(103.34, -85.7) * mm});
            skLineSegment(sketch, "E1023", {"start": v(103.34, -85.7) * mm, "end": v(101.34, -84.31) * mm});
            skLineSegment(sketch, "E1024", {"start": v(101.34, -84.31) * mm, "end": v(99.62, -83.24) * mm});
            skLineSegment(sketch, "E1025", {"start": v(99.62, -83.24) * mm, "end": v(98.23, -82.44) * mm});
            skLineSegment(sketch, "E1026", {"start": v(98.23, -82.44) * mm, "end": v(97.68, -82.16) * mm});
            skLineSegment(sketch, "E1027", {"start": v(97.68, -82.16) * mm, "end": v(95.99, -81.17) * mm});
            skLineSegment(sketch, "E1028", {"start": v(95.99, -81.17) * mm, "end": v(94.77, -80.2) * mm});
            skLineSegment(sketch, "E1029", {"start": v(94.77, -80.2) * mm, "end": v(94, -79.28) * mm});
            skLineSegment(sketch, "E1030", {"start": v(94, -79.28) * mm, "end": v(93.7, -78.46) * mm});
            skLineSegment(sketch, "E1031", {"start": v(93.7, -78.46) * mm, "end": v(93.85, -77.78) * mm});
            skLineSegment(sketch, "E1032", {"start": v(93.85, -77.78) * mm, "end": v(94.48, -76.07) * mm});
            skLineSegment(sketch, "E1033", {"start": v(94.48, -76.07) * mm, "end": v(97.48, -66.86) * mm});
            skLineSegment(sketch, "E1034", {"start": v(97.48, -66.86) * mm, "end": v(97.97, -65.11) * mm});
            skLineSegment(sketch, "E1035", {"start": v(97.97, -65.11) * mm, "end": v(98.25, -64.47) * mm});
            skLineSegment(sketch, "E1036", {"start": v(98.25, -64.47) * mm, "end": v(98.98, -63.99) * mm});
            skLineSegment(sketch, "E1037", {"start": v(98.98, -63.99) * mm, "end": v(100.13, -63.7) * mm});
            skLineSegment(sketch, "E1038", {"start": v(100.13, -63.7) * mm, "end": v(101.69, -63.62) * mm});
            skLineSegment(sketch, "E1039", {"start": v(101.69, -63.62) * mm, "end": v(103.64, -63.81) * mm});
            skLineSegment(sketch, "E1040", {"start": v(103.64, -63.81) * mm, "end": v(104.25, -63.9) * mm});
            skLineSegment(sketch, "E1041", {"start": v(104.25, -63.9) * mm, "end": v(105.85, -64.08) * mm});
            skLineSegment(sketch, "E1042", {"start": v(105.85, -64.08) * mm, "end": v(107.86, -64.22) * mm});
            skLineSegment(sketch, "E1043", {"start": v(107.86, -64.22) * mm, "end": v(110.3, -64.29) * mm});
            skLineSegment(sketch, "E1044", {"start": v(110.3, -64.29) * mm, "end": v(113.14, -64.24) * mm});
            skLineSegment(sketch, "E1045", {"start": v(113.14, -64.24) * mm, "end": v(116.39, -64.06) * mm});
            skLineSegment(sketch, "E1046", {"start": v(116.39, -64.06) * mm, "end": v(120.04, -63.7) * mm});
            skLineSegment(sketch, "E1047", {"start": v(120.04, -63.7) * mm, "end": v(124.08, -63.12) * mm});
            skLineSegment(sketch, "E1048", {"start": v(124.08, -63.12) * mm, "end": v(128.5, -62.3) * mm});
            skLineSegment(sketch, "E1049", {"start": v(128.5, -62.3) * mm, "end": v(133.04, -61.26) * mm});
            skLineSegment(sketch, "E1050", {"start": v(112.12, 34.82) * mm, "end": v(110.51, 29.21) * mm});
            skLineSegment(sketch, "E1051", {"start": v(110.51, 29.21) * mm, "end": v(109.7, 23.44) * mm});
            skLineSegment(sketch, "E1052", {"start": v(109.7, 23.44) * mm, "end": v(111.93, 21.37) * mm});
            skLineSegment(sketch, "E1053", {"start": v(111.93, 21.37) * mm, "end": v(116.35, 17.9) * mm});
            skLineSegment(sketch, "E1054", {"start": v(116.35, 17.9) * mm, "end": v(120.36, 15.27) * mm});
            skLineSegment(sketch, "E1055", {"start": v(120.36, 15.27) * mm, "end": v(123.86, 13.38) * mm});
            skLineSegment(sketch, "E1056", {"start": v(123.86, 13.38) * mm, "end": v(126.74, 12.11) * mm});
            skLineSegment(sketch, "E1057", {"start": v(126.74, 12.11) * mm, "end": v(128.94, 11.36) * mm});
            skLineSegment(sketch, "E1058", {"start": v(128.94, 11.36) * mm, "end": v(130.4, 11) * mm});
            skLineSegment(sketch, "E1059", {"start": v(130.4, 11) * mm, "end": v(131.07, 10.88) * mm});
            skLineSegment(sketch, "E1060", {"start": v(131.07, 10.88) * mm, "end": v(134.44, 10.62) * mm});
            skLineSegment(sketch, "E1061", {"start": v(134.44, 10.62) * mm, "end": v(137.46, 9.84) * mm});
            skLineSegment(sketch, "E1062", {"start": v(137.46, 9.84) * mm, "end": v(139.54, 8.7) * mm});
            skLineSegment(sketch, "E1063", {"start": v(139.54, 8.7) * mm, "end": v(140.65, 7.36) * mm});
            skLineSegment(sketch, "E1064", {"start": v(140.65, 7.36) * mm, "end": v(140.77, 5.96) * mm});
            skLineSegment(sketch, "E1065", {"start": v(140.77, 5.96) * mm, "end": v(140.65, 4.5) * mm});
            skLineSegment(sketch, "E1066", {"start": v(140.65, 4.5) * mm, "end": v(140.65, -4.5) * mm});
            skLineSegment(sketch, "E1067", {"start": v(140.65, -4.5) * mm, "end": v(140.77, -5.96) * mm});
            skLineSegment(sketch, "E1068", {"start": v(140.77, -5.96) * mm, "end": v(140.65, -7.36) * mm});
            skLineSegment(sketch, "E1069", {"start": v(140.65, -7.36) * mm, "end": v(139.54, -8.7) * mm});
            skLineSegment(sketch, "E1070", {"start": v(139.54, -8.7) * mm, "end": v(137.46, -9.84) * mm});
            skLineSegment(sketch, "E1071", {"start": v(137.46, -9.84) * mm, "end": v(134.44, -10.62) * mm});
            skLineSegment(sketch, "E1072", {"start": v(134.44, -10.62) * mm, "end": v(131.07, -10.88) * mm});
            skLineSegment(sketch, "E1073", {"start": v(131.07, -10.88) * mm, "end": v(130.4, -11) * mm});
            skLineSegment(sketch, "E1074", {"start": v(130.4, -11) * mm, "end": v(128.94, -11.36) * mm});
            skLineSegment(sketch, "E1075", {"start": v(128.94, -11.36) * mm, "end": v(126.74, -12.11) * mm});
            skLineSegment(sketch, "E1076", {"start": v(126.74, -12.11) * mm, "end": v(123.86, -13.38) * mm});
            skLineSegment(sketch, "E1077", {"start": v(123.86, -13.38) * mm, "end": v(120.36, -15.27) * mm});
            skLineSegment(sketch, "E1078", {"start": v(120.36, -15.27) * mm, "end": v(116.35, -17.9) * mm});
            skLineSegment(sketch, "E1079", {"start": v(116.35, -17.9) * mm, "end": v(111.93, -21.37) * mm});
            skLineSegment(sketch, "E1080", {"start": v(111.93, -21.37) * mm, "end": v(109.7, -23.44) * mm});
            skLineSegment(sketch, "E1081", {"start": v(109.7, -23.44) * mm, "end": v(110.51, -29.21) * mm});
            skLineSegment(sketch, "E1082", {"start": v(110.51, -29.21) * mm, "end": v(112.12, -34.82) * mm});
            skLineSegment(sketch, "E1083", {"start": v(112.12, -34.82) * mm, "end": v(115, -35.8) * mm});
            skLineSegment(sketch, "E1084", {"start": v(115, -35.8) * mm, "end": v(120.44, -37.17) * mm});
            skLineSegment(sketch, "E1085", {"start": v(120.44, -37.17) * mm, "end": v(125.18, -37.94) * mm});
            skLineSegment(sketch, "E1086", {"start": v(125.18, -37.94) * mm, "end": v(129.14, -38.25) * mm});
            skLineSegment(sketch, "E1087", {"start": v(129.14, -38.25) * mm, "end": v(132.3, -38.23) * mm});
            skLineSegment(sketch, "E1088", {"start": v(132.3, -38.23) * mm, "end": v(134.61, -38.03) * mm});
            skLineSegment(sketch, "E1089", {"start": v(134.61, -38.03) * mm, "end": v(136.1, -37.77) * mm});
            skLineSegment(sketch, "E1090", {"start": v(136.1, -37.77) * mm, "end": v(136.75, -37.6) * mm});
            skLineSegment(sketch, "E1091", {"start": v(136.75, -37.6) * mm, "end": v(139.93, -36.47) * mm});
            skLineSegment(sketch, "E1092", {"start": v(139.93, -36.47) * mm, "end": v(143, -35.95) * mm});
            skLineSegment(sketch, "E1093", {"start": v(143, -35.95) * mm, "end": v(145.37, -36.14) * mm});
            skLineSegment(sketch, "E1094", {"start": v(145.37, -36.14) * mm, "end": v(146.93, -36.92) * mm});
            skLineSegment(sketch, "E1095", {"start": v(146.93, -36.92) * mm, "end": v(147.61, -38.15) * mm});
            skLineSegment(sketch, "E1096", {"start": v(147.61, -38.15) * mm, "end": v(148.1, -39.53) * mm});
            skLineSegment(sketch, "E1097", {"start": v(148.1, -39.53) * mm, "end": v(151.75, -47.75) * mm});
            skLineSegment(sketch, "E1098", {"start": v(151.75, -47.75) * mm, "end": v(152.46, -49.04) * mm});
            skLineSegment(sketch, "E1099", {"start": v(152.46, -49.04) * mm, "end": v(152.92, -50.36) * mm});
            skLineSegment(sketch, "E1100", {"start": v(152.92, -50.36) * mm, "end": v(152.45, -52.04) * mm});
            skLineSegment(sketch, "E1101", {"start": v(152.45, -52.04) * mm, "end": v(151.01, -53.93) * mm});
            skLineSegment(sketch, "E1102", {"start": v(151.01, -53.93) * mm, "end": v(148.57, -55.87) * mm});
            skLineSegment(sketch, "E1103", {"start": v(148.57, -55.87) * mm, "end": v(145.6, -57.48) * mm});
            skLineSegment(sketch, "E1104", {"start": v(145.6, -57.48) * mm, "end": v(145.04, -57.85) * mm});
            skLineSegment(sketch, "E1105", {"start": v(145.04, -57.85) * mm, "end": v(143.85, -58.78) * mm});
            skLineSegment(sketch, "E1106", {"start": v(143.85, -58.78) * mm, "end": v(142.15, -60.36) * mm});
            skLineSegment(sketch, "E1107", {"start": v(142.15, -60.36) * mm, "end": v(140.03, -62.7) * mm});
            skLineSegment(sketch, "E1108", {"start": v(140.03, -62.7) * mm, "end": v(137.6, -65.85) * mm});
            skLineSegment(sketch, "E1109", {"start": v(137.6, -65.85) * mm, "end": v(135.01, -69.88) * mm});
            skLineSegment(sketch, "E1110", {"start": v(135.01, -69.88) * mm, "end": v(132.38, -74.85) * mm});
            skLineSegment(sketch, "E1111", {"start": v(132.38, -74.85) * mm, "end": v(131.19, -77.64) * mm});
            skLineSegment(sketch, "E1112", {"start": v(131.19, -77.64) * mm, "end": v(134.28, -82.59) * mm});
            skLineSegment(sketch, "E1113", {"start": v(134.28, -82.59) * mm, "end": v(138.03, -87.05) * mm});
            skLineSegment(sketch, "E1114", {"start": v(138.03, -87.05) * mm, "end": v(141.05, -86.78) * mm});
            skLineSegment(sketch, "E1115", {"start": v(141.05, -86.78) * mm, "end": v(146.58, -85.81) * mm});
            skLineSegment(sketch, "E1116", {"start": v(146.58, -85.81) * mm, "end": v(151.23, -84.6) * mm});
            skLineSegment(sketch, "E1117", {"start": v(151.23, -84.6) * mm, "end": v(154.97, -83.27) * mm});
            skLineSegment(sketch, "E1118", {"start": v(154.97, -83.27) * mm, "end": v(157.84, -81.97) * mm});
            skLineSegment(sketch, "E1119", {"start": v(157.84, -81.97) * mm, "end": v(159.88, -80.84) * mm});
            skLineSegment(sketch, "E1120", {"start": v(159.88, -80.84) * mm, "end": v(161.12, -80) * mm});
            skLineSegment(sketch, "E1121", {"start": v(161.12, -80) * mm, "end": v(161.65, -79.57) * mm});
            skLineSegment(sketch, "E1122", {"start": v(161.65, -79.57) * mm, "end": v(164.1, -77.25) * mm});
            skLineSegment(sketch, "E1123", {"start": v(164.1, -77.25) * mm, "end": v(166.7, -75.52) * mm});
            skLineSegment(sketch, "E1124", {"start": v(166.7, -75.52) * mm, "end": v(168.94, -74.74) * mm});
            skLineSegment(sketch, "E1125", {"start": v(168.94, -74.74) * mm, "end": v(170.68, -74.82) * mm});
            skLineSegment(sketch, "E1126", {"start": v(170.68, -74.82) * mm, "end": v(171.8, -75.66) * mm});
            skLineSegment(sketch, "E1127", {"start": v(171.8, -75.66) * mm, "end": v(172.8, -76.73) * mm});
            skLineSegment(sketch, "E1128", {"start": v(172.8, -76.73) * mm, "end": v(179.5, -82.75) * mm});
            skLineSegment(sketch, "E1129", {"start": v(179.5, -82.75) * mm, "end": v(180.66, -83.64) * mm});
            skLineSegment(sketch, "E1130", {"start": v(180.66, -83.64) * mm, "end": v(181.62, -84.66) * mm});
            skLineSegment(sketch, "E1131", {"start": v(181.62, -84.66) * mm, "end": v(181.88, -86.39) * mm});
            skLineSegment(sketch, "E1132", {"start": v(181.88, -86.39) * mm, "end": v(181.33, -88.7) * mm});
            skLineSegment(sketch, "E1133", {"start": v(181.33, -88.7) * mm, "end": v(179.89, -91.46) * mm});
            skLineSegment(sketch, "E1134", {"start": v(179.89, -91.46) * mm, "end": v(177.83, -94.14) * mm});
            skLineSegment(sketch, "E1135", {"start": v(177.83, -94.14) * mm, "end": v(177.46, -94.7) * mm});
            skLineSegment(sketch, "E1136", {"start": v(177.46, -94.7) * mm, "end": v(176.76, -96.04) * mm});
            skLineSegment(sketch, "E1137", {"start": v(176.76, -96.04) * mm, "end": v(175.85, -98.18) * mm});
            skLineSegment(sketch, "E1138", {"start": v(175.85, -98.18) * mm, "end": v(174.86, -101.17) * mm});
            skLineSegment(sketch, "E1139", {"start": v(174.86, -101.17) * mm, "end": v(173.93, -105.03) * mm});
            skLineSegment(sketch, "E1140", {"start": v(173.93, -105.03) * mm, "end": v(173.2, -109.78) * mm});
            skLineSegment(sketch, "E1141", {"start": v(173.2, -109.78) * mm, "end": v(172.82, -115.39) * mm});
            skLineSegment(sketch, "E1142", {"start": v(172.82, -115.39) * mm, "end": v(172.86, -118.42) * mm});
            skLineSegment(sketch, "E1143", {"start": v(172.86, -118.42) * mm, "end": v(177.7, -121.68) * mm});
            skLineSegment(sketch, "E1144", {"start": v(177.7, -121.68) * mm, "end": v(182.94, -124.24) * mm});
            skLineSegment(sketch, "E1145", {"start": v(182.94, -124.24) * mm, "end": v(185.59, -122.76) * mm});
            skLineSegment(sketch, "E1146", {"start": v(185.59, -122.76) * mm, "end": v(190.25, -119.62) * mm});
            skLineSegment(sketch, "E1147", {"start": v(190.25, -119.62) * mm, "end": v(194, -116.62) * mm});
            skLineSegment(sketch, "E1148", {"start": v(194, -116.62) * mm, "end": v(196.88, -113.88) * mm});
            skLineSegment(sketch, "E1149", {"start": v(196.88, -113.88) * mm, "end": v(198.97, -111.53) * mm});
            skLineSegment(sketch, "E1150", {"start": v(198.97, -111.53) * mm, "end": v(200.37, -109.67) * mm});
            skLineSegment(sketch, "E1151", {"start": v(200.37, -109.67) * mm, "end": v(201.17, -108.4) * mm});
            skLineSegment(sketch, "E1152", {"start": v(201.17, -108.4) * mm, "end": v(201.48, -107.8) * mm});
            skLineSegment(sketch, "E1153", {"start": v(201.48, -107.8) * mm, "end": v(202.77, -104.67) * mm});
            skLineSegment(sketch, "E1154", {"start": v(202.77, -104.67) * mm, "end": v(204.45, -102.04) * mm});
            skLineSegment(sketch, "E1155", {"start": v(204.45, -102.04) * mm, "end": v(206.17, -100.41) * mm});
            skLineSegment(sketch, "E1156", {"start": v(206.17, -100.41) * mm, "end": v(207.8, -99.78) * mm});
            skLineSegment(sketch, "E1157", {"start": v(207.8, -99.78) * mm, "end": v(209.16, -100.09) * mm});
            skLineSegment(sketch, "E1158", {"start": v(209.16, -100.09) * mm, "end": v(210.51, -100.66) * mm});
            skLineSegment(sketch, "E1159", {"start": v(210.51, -100.66) * mm, "end": v(219.07, -103.44) * mm});
            skLineSegment(sketch, "E1160", {"start": v(219.07, -103.44) * mm, "end": v(220.5, -103.77) * mm});
            skLineSegment(sketch, "E1161", {"start": v(220.5, -103.77) * mm, "end": v(221.79, -104.32) * mm});
            skLineSegment(sketch, "E1162", {"start": v(221.79, -104.32) * mm, "end": v(222.72, -105.8) * mm});
            skLineSegment(sketch, "E1163", {"start": v(222.72, -105.8) * mm, "end": v(223.16, -108.12) * mm});
            skLineSegment(sketch, "E1164", {"start": v(223.16, -108.12) * mm, "end": v(222.97, -111.23) * mm});
            skLineSegment(sketch, "E1165", {"start": v(222.97, -111.23) * mm, "end": v(222.18, -114.52) * mm});
            skLineSegment(sketch, "E1166", {"start": v(222.18, -114.52) * mm, "end": v(222.08, -115.19) * mm});
            skLineSegment(sketch, "E1167", {"start": v(222.08, -115.19) * mm, "end": v(221.98, -116.69) * mm});
            skLineSegment(sketch, "E1168", {"start": v(221.98, -116.69) * mm, "end": v(222.01, -119.02) * mm});
            skLineSegment(sketch, "E1169", {"start": v(222.01, -119.02) * mm, "end": v(222.32, -122.15) * mm});
            skLineSegment(sketch, "E1170", {"start": v(222.32, -122.15) * mm, "end": v(223.05, -126.06) * mm});
            skLineSegment(sketch, "E1171", {"start": v(223.05, -126.06) * mm, "end": v(224.31, -130.69) * mm});
            skLineSegment(sketch, "E1172", {"start": v(224.31, -130.69) * mm, "end": v(226.24, -135.97) * mm});
            skLineSegment(sketch, "E1173", {"start": v(226.24, -135.97) * mm, "end": v(227.52, -138.72) * mm});
            skLineSegment(sketch, "E1174", {"start": v(227.52, -138.72) * mm, "end": v(233.26, -139.73) * mm});
            skLineSegment(sketch, "E1175", {"start": v(233.26, -139.73) * mm, "end": v(239.09, -139.94) * mm});
            skLineSegment(sketch, "E1176", {"start": v(239.09, -139.94) * mm, "end": v(240.9, -137.51) * mm});
            skLineSegment(sketch, "E1177", {"start": v(240.9, -137.51) * mm, "end": v(243.9, -132.75) * mm});
            skLineSegment(sketch, "E1178", {"start": v(243.9, -132.75) * mm, "end": v(246.1, -128.48) * mm});
            skLineSegment(sketch, "E1179", {"start": v(246.1, -128.48) * mm, "end": v(247.61, -124.81) * mm});
            skLineSegment(sketch, "E1180", {"start": v(247.61, -124.81) * mm, "end": v(248.57, -121.8) * mm});
            skLineSegment(sketch, "E1181", {"start": v(248.57, -121.8) * mm, "end": v(249.1, -119.54) * mm});
            skLineSegment(sketch, "E1182", {"start": v(249.1, -119.54) * mm, "end": v(249.3, -118.05) * mm});
            skLineSegment(sketch, "E1183", {"start": v(249.3, -118.05) * mm, "end": v(249.34, -117.37) * mm});
            skLineSegment(sketch, "E1184", {"start": v(249.34, -117.37) * mm, "end": v(249.25, -114) * mm});
            skLineSegment(sketch, "E1185", {"start": v(249.25, -114) * mm, "end": v(249.71, -110.91) * mm});
            skLineSegment(sketch, "E1186", {"start": v(249.71, -110.91) * mm, "end": v(250.63, -108.72) * mm});
            skLineSegment(sketch, "E1187", {"start": v(250.63, -108.72) * mm, "end": v(251.85, -107.48) * mm});
            skLineSegment(sketch, "E1188", {"start": v(251.85, -107.48) * mm, "end": v(253.22, -107.21) * mm});
            skLineSegment(sketch, "E1189", {"start": v(253.22, -107.21) * mm, "end": v(254.7, -107.18) * mm});
            skLineSegment(sketch, "E1190", {"start": v(254.7, -107.18) * mm, "end": v(263.64, -106.24) * mm});
            skLineSegment(sketch, "E1191", {"start": v(263.64, -106.24) * mm, "end": v(265.08, -105.97) * mm});
            skLineSegment(sketch, "E1192", {"start": v(265.08, -105.97) * mm, "end": v(266.48, -105.94) * mm});
            skLineSegment(sketch, "E1193", {"start": v(266.48, -105.94) * mm, "end": v(267.93, -106.9) * mm});
            skLineSegment(sketch, "E1194", {"start": v(267.93, -106.9) * mm, "end": v(269.28, -108.85) * mm});
            skLineSegment(sketch, "E1195", {"start": v(269.28, -108.85) * mm, "end": v(270.37, -111.78) * mm});
            skLineSegment(sketch, "E1196", {"start": v(270.37, -111.78) * mm, "end": v(270.99, -115.1) * mm});
            skLineSegment(sketch, "E1197", {"start": v(270.99, -115.1) * mm, "end": v(271.17, -115.75) * mm});
            skLineSegment(sketch, "E1198", {"start": v(271.17, -115.75) * mm, "end": v(271.68, -117.16) * mm});
            skLineSegment(sketch, "E1199", {"start": v(271.68, -117.16) * mm, "end": v(272.66, -119.28) * mm});
            skLineSegment(sketch, "E1200", {"start": v(272.66, -119.28) * mm, "end": v(274.22, -122.01) * mm});
            skLineSegment(sketch, "E1201", {"start": v(274.22, -122.01) * mm, "end": v(276.47, -125.3) * mm});
            skLineSegment(sketch, "E1202", {"start": v(276.47, -125.3) * mm, "end": v(279.51, -129) * mm});
            skLineSegment(sketch, "E1203", {"start": v(279.51, -129) * mm, "end": v(283.42, -133.04) * mm});
            skLineSegment(sketch, "E1204", {"start": v(283.42, -133.04) * mm, "end": v(285.7, -135.04) * mm});
            skLineSegment(sketch, "E1205", {"start": v(285.7, -135.04) * mm, "end": v(291.37, -133.63) * mm});
            skLineSegment(sketch, "E1206", {"start": v(291.37, -133.63) * mm, "end": v(296.77, -131.44) * mm});
            skLineSegment(sketch, "E1207", {"start": v(296.77, -131.44) * mm, "end": v(297.45, -128.49) * mm});
            skLineSegment(sketch, "E1208", {"start": v(297.45, -128.49) * mm, "end": v(298.24, -122.92) * mm});
            skLineSegment(sketch, "E1209", {"start": v(298.24, -122.92) * mm, "end": v(298.51, -118.13) * mm});
            skLineSegment(sketch, "E1210", {"start": v(298.51, -118.13) * mm, "end": v(298.4, -114.16) * mm});
            skLineSegment(sketch, "E1211", {"start": v(298.4, -114.16) * mm, "end": v(298.06, -111.02) * mm});
            skLineSegment(sketch, "E1212", {"start": v(298.06, -111.02) * mm, "end": v(297.61, -108.74) * mm});
            skLineSegment(sketch, "E1213", {"start": v(297.61, -108.74) * mm, "end": v(297.2, -107.3) * mm});
            skLineSegment(sketch, "E1214", {"start": v(297.2, -107.3) * mm, "end": v(296.96, -106.66) * mm});
            skLineSegment(sketch, "E1215", {"start": v(296.96, -106.66) * mm, "end": v(295.5, -103.6) * mm});
            skLineSegment(sketch, "E1216", {"start": v(295.5, -103.6) * mm, "end": v(294.67, -100.6) * mm});
            skLineSegment(sketch, "E1217", {"start": v(294.67, -100.6) * mm, "end": v(294.62, -98.24) * mm});
            skLineSegment(sketch, "E1218", {"start": v(294.62, -98.24) * mm, "end": v(295.23, -96.6) * mm});
            skLineSegment(sketch, "E1219", {"start": v(295.23, -96.6) * mm, "end": v(296.38, -95.8) * mm});
            skLineSegment(sketch, "E1220", {"start": v(296.38, -95.8) * mm, "end": v(297.7, -95.17) * mm});
            skLineSegment(sketch, "E1221", {"start": v(297.7, -95.17) * mm, "end": v(305.5, -90.68) * mm});
            skLineSegment(sketch, "E1222", {"start": v(305.5, -90.68) * mm, "end": v(306.7, -89.84) * mm});
            skLineSegment(sketch, "E1223", {"start": v(306.7, -89.84) * mm, "end": v(307.97, -89.25) * mm});
            skLineSegment(sketch, "E1224", {"start": v(307.97, -89.25) * mm, "end": v(309.69, -89.53) * mm});
            skLineSegment(sketch, "E1225", {"start": v(309.69, -89.53) * mm, "end": v(311.71, -90.77) * mm});
            skLineSegment(sketch, "E1226", {"start": v(311.71, -90.77) * mm, "end": v(313.9, -92.99) * mm});
            skLineSegment(sketch, "E1227", {"start": v(313.9, -92.99) * mm, "end": v(315.81, -95.77) * mm});
            skLineSegment(sketch, "E1228", {"start": v(315.81, -95.77) * mm, "end": v(316.24, -96.3) * mm});
            skLineSegment(sketch, "E1229", {"start": v(316.24, -96.3) * mm, "end": v(317.29, -97.38) * mm});
            skLineSegment(sketch, "E1230", {"start": v(317.29, -97.38) * mm, "end": v(319.04, -98.91) * mm});
            skLineSegment(sketch, "E1231", {"start": v(319.04, -98.91) * mm, "end": v(321.58, -100.78) * mm});
            skLineSegment(sketch, "E1232", {"start": v(321.58, -100.78) * mm, "end": v(324.97, -102.86) * mm});
            skLineSegment(sketch, "E1233", {"start": v(324.97, -102.86) * mm, "end": v(329.25, -105.01) * mm});
            skLineSegment(sketch, "E1234", {"start": v(329.25, -105.01) * mm, "end": v(334.47, -107.11) * mm});
            skLineSegment(sketch, "E1235", {"start": v(334.47, -107.11) * mm, "end": v(337.37, -108) * mm});
            skLineSegment(sketch, "E1236", {"start": v(337.37, -108) * mm, "end": v(341.96, -104.41) * mm});
            skLineSegment(sketch, "E1237", {"start": v(341.96, -104.41) * mm, "end": v(346.01, -100.22) * mm});
            skLineSegment(sketch, "E1238", {"start": v(346.01, -100.22) * mm, "end": v(345.43, -97.24) * mm});
            skLineSegment(sketch, "E1239", {"start": v(345.43, -97.24) * mm, "end": v(343.89, -91.84) * mm});
            skLineSegment(sketch, "E1240", {"start": v(343.89, -91.84) * mm, "end": v(342.19, -87.35) * mm});
            skLineSegment(sketch, "E1241", {"start": v(342.19, -87.35) * mm, "end": v(340.48, -83.76) * mm});
            skLineSegment(sketch, "E1242", {"start": v(340.48, -83.76) * mm, "end": v(338.89, -81.04) * mm});
            skLineSegment(sketch, "E1243", {"start": v(338.89, -81.04) * mm, "end": v(337.55, -79.14) * mm});
            skLineSegment(sketch, "E1244", {"start": v(337.55, -79.14) * mm, "end": v(336.58, -77.99) * mm});
            skLineSegment(sketch, "E1245", {"start": v(336.58, -77.99) * mm, "end": v(336.1, -77.5) * mm});
            skLineSegment(sketch, "E1246", {"start": v(336.1, -77.5) * mm, "end": v(333.53, -75.3) * mm});
            skLineSegment(sketch, "E1247", {"start": v(333.53, -75.3) * mm, "end": v(331.55, -72.9) * mm});
            skLineSegment(sketch, "E1248", {"start": v(331.55, -72.9) * mm, "end": v(330.54, -70.76) * mm});
            skLineSegment(sketch, "E1249", {"start": v(330.54, -70.76) * mm, "end": v(330.43, -69.02) * mm});
            skLineSegment(sketch, "E1250", {"start": v(330.43, -69.02) * mm, "end": v(331.15, -67.82) * mm});
            skLineSegment(sketch, "E1251", {"start": v(331.15, -67.82) * mm, "end": v(332.11, -66.7) * mm});
            skLineSegment(sketch, "E1252", {"start": v(332.11, -66.7) * mm, "end": v(337.4, -59.43) * mm});
            skLineSegment(sketch, "E1253", {"start": v(337.4, -59.43) * mm, "end": v(338.16, -58.18) * mm});
            skLineSegment(sketch, "E1254", {"start": v(338.16, -58.18) * mm, "end": v(339.08, -57.12) * mm});
            skLineSegment(sketch, "E1255", {"start": v(339.08, -57.12) * mm, "end": v(340.77, -56.68) * mm});
            skLineSegment(sketch, "E1256", {"start": v(340.77, -56.68) * mm, "end": v(343.12, -56.98) * mm});
            skLineSegment(sketch, "E1257", {"start": v(343.12, -56.98) * mm, "end": v(346.02, -58.13) * mm});
            skLineSegment(sketch, "E1258", {"start": v(346.02, -58.13) * mm, "end": v(348.9, -59.9) * mm});
            skLineSegment(sketch, "E1259", {"start": v(348.9, -59.9) * mm, "end": v(349.5, -60.2) * mm});
            skLineSegment(sketch, "E1260", {"start": v(349.5, -60.2) * mm, "end": v(350.9, -60.76) * mm});
            skLineSegment(sketch, "E1261", {"start": v(350.9, -60.76) * mm, "end": v(353.13, -61.44) * mm});
            skLineSegment(sketch, "E1262", {"start": v(353.13, -61.44) * mm, "end": v(356.2, -62.12) * mm});
            skLineSegment(sketch, "E1263", {"start": v(356.2, -62.12) * mm, "end": v(360.14, -62.64) * mm});
            skLineSegment(sketch, "E1264", {"start": v(360.14, -62.64) * mm, "end": v(364.94, -62.86) * mm});
            skLineSegment(sketch, "E1265", {"start": v(364.94, -62.86) * mm, "end": v(370.56, -62.66) * mm});
            skLineSegment(sketch, "E1266", {"start": v(370.56, -62.66) * mm, "end": v(373.57, -62.3) * mm});
            skLineSegment(sketch, "E1267", {"start": v(373.57, -62.3) * mm, "end": v(376.3, -57.15) * mm});
            skLineSegment(sketch, "E1268", {"start": v(376.3, -57.15) * mm, "end": v(378.3, -51.67) * mm});
            skLineSegment(sketch, "E1269", {"start": v(378.3, -51.67) * mm, "end": v(376.55, -49.19) * mm});
            skLineSegment(sketch, "E1270", {"start": v(376.55, -49.19) * mm, "end": v(372.95, -44.88) * mm});
            skLineSegment(sketch, "E1271", {"start": v(372.95, -44.88) * mm, "end": v(369.57, -41.47) * mm});
            skLineSegment(sketch, "E1272", {"start": v(369.57, -41.47) * mm, "end": v(366.55, -38.89) * mm});
            skLineSegment(sketch, "E1273", {"start": v(366.55, -38.89) * mm, "end": v(363.99, -37.05) * mm});
            skLineSegment(sketch, "E1274", {"start": v(363.99, -37.05) * mm, "end": v(361.99, -35.85) * mm});
            skLineSegment(sketch, "E1275", {"start": v(361.99, -35.85) * mm, "end": v(360.64, -35.2) * mm});
            skLineSegment(sketch, "E1276", {"start": v(360.64, -35.2) * mm, "end": v(360, -34.95) * mm});
            skLineSegment(sketch, "E1277", {"start": v(360, -34.95) * mm, "end": v(356.77, -33.99) * mm});
            skLineSegment(sketch, "E1278", {"start": v(356.77, -33.99) * mm, "end": v(353.98, -32.6) * mm});
            skLineSegment(sketch, "E1279", {"start": v(353.98, -32.6) * mm, "end": v(352.18, -31.05) * mm});
            skLineSegment(sketch, "E1280", {"start": v(352.18, -31.05) * mm, "end": v(351.37, -29.5) * mm});
            skLineSegment(sketch, "E1281", {"start": v(351.37, -29.5) * mm, "end": v(351.54, -28.11) * mm});
            skLineSegment(sketch, "E1282", {"start": v(351.54, -28.11) * mm, "end": v(351.97, -26.7) * mm});
            skLineSegment(sketch, "E1283", {"start": v(351.97, -26.7) * mm, "end": v(353.84, -17.9) * mm});
            skLineSegment(sketch, "E1284", {"start": v(353.84, -17.9) * mm, "end": v(354.02, -16.45) * mm});
            skLineSegment(sketch, "E1285", {"start": v(354.02, -16.45) * mm, "end": v(354.43, -15.11) * mm});
            skLineSegment(sketch, "E1286", {"start": v(354.43, -15.11) * mm, "end": v(355.8, -14.03) * mm});
            skLineSegment(sketch, "E1287", {"start": v(355.8, -14.03) * mm, "end": v(358.07, -13.35) * mm});
            skLineSegment(sketch, "E1288", {"start": v(358.07, -13.35) * mm, "end": v(361.18, -13.21) * mm});
            skLineSegment(sketch, "E1289", {"start": v(361.18, -13.21) * mm, "end": v(364.53, -13.65) * mm});
            skLineSegment(sketch, "E1290", {"start": v(364.53, -13.65) * mm, "end": v(365.21, -13.69) * mm});
            skLineSegment(sketch, "E1291", {"start": v(365.21, -13.69) * mm, "end": v(366.71, -13.63) * mm});
            skLineSegment(sketch, "E1292", {"start": v(366.71, -13.63) * mm, "end": v(369.02, -13.35) * mm});
            skLineSegment(sketch, "E1293", {"start": v(369.02, -13.35) * mm, "end": v(372.1, -12.71) * mm});
            skLineSegment(sketch, "E1294", {"start": v(372.1, -12.71) * mm, "end": v(375.92, -11.59) * mm});
            skLineSegment(sketch, "E1295", {"start": v(375.92, -11.59) * mm, "end": v(380.4, -9.84) * mm});
            skLineSegment(sketch, "E1296", {"start": v(380.4, -9.84) * mm, "end": v(385.44, -7.37) * mm});
            skLineSegment(sketch, "E1297", {"start": v(385.44, -7.37) * mm, "end": v(388.05, -5.82) * mm});
            skLineSegment(sketch, "E1298", {"start": v(388.05, -5.82) * mm, "end": v(388.45, 0) * mm});
            skLineSegment(sketch, "E1299", {"start": v(388.45, 0) * mm, "end": v(388.05, 5.82) * mm});
            skLineSegment(sketch, "E1300", {"start": v(388.05, 5.82) * mm, "end": v(385.44, 7.37) * mm});
            skLineSegment(sketch, "E1301", {"start": v(385.44, 7.37) * mm, "end": v(380.4, 9.84) * mm});
            skLineSegment(sketch, "E1302", {"start": v(380.4, 9.84) * mm, "end": v(375.92, 11.59) * mm});
            skLineSegment(sketch, "E1303", {"start": v(375.92, 11.59) * mm, "end": v(372.1, 12.71) * mm});
            skLineSegment(sketch, "E1304", {"start": v(372.1, 12.71) * mm, "end": v(369.02, 13.35) * mm});
            skLineSegment(sketch, "E1305", {"start": v(369.02, 13.35) * mm, "end": v(366.71, 13.63) * mm});
            skLineSegment(sketch, "E1306", {"start": v(366.71, 13.63) * mm, "end": v(365.21, 13.69) * mm});
            skLineSegment(sketch, "E1307", {"start": v(365.21, 13.69) * mm, "end": v(364.53, 13.65) * mm});
            skLineSegment(sketch, "E1308", {"start": v(364.53, 13.65) * mm, "end": v(361.18, 13.21) * mm});
            skLineSegment(sketch, "E1309", {"start": v(361.18, 13.21) * mm, "end": v(358.07, 13.35) * mm});
            skLineSegment(sketch, "E1310", {"start": v(358.07, 13.35) * mm, "end": v(355.8, 14.03) * mm});
            skLineSegment(sketch, "E1311", {"start": v(355.8, 14.03) * mm, "end": v(354.43, 15.11) * mm});
            skLineSegment(sketch, "E1312", {"start": v(354.43, 15.11) * mm, "end": v(354.02, 16.45) * mm});
            skLineSegment(sketch, "E1313", {"start": v(354.02, 16.45) * mm, "end": v(353.84, 17.9) * mm});
            skLineSegment(sketch, "E1314", {"start": v(353.84, 17.9) * mm, "end": v(351.97, 26.7) * mm});
            skLineSegment(sketch, "E1315", {"start": v(351.97, 26.7) * mm, "end": v(351.54, 28.11) * mm});
            skLineSegment(sketch, "E1316", {"start": v(351.54, 28.11) * mm, "end": v(351.37, 29.5) * mm});
            skLineSegment(sketch, "E1317", {"start": v(351.37, 29.5) * mm, "end": v(352.18, 31.05) * mm});
            skLineSegment(sketch, "E1318", {"start": v(352.18, 31.05) * mm, "end": v(353.98, 32.6) * mm});
            skLineSegment(sketch, "E1319", {"start": v(353.98, 32.6) * mm, "end": v(356.77, 33.99) * mm});
            skLineSegment(sketch, "E1320", {"start": v(356.77, 33.99) * mm, "end": v(360, 34.95) * mm});
            skLineSegment(sketch, "E1321", {"start": v(360, 34.95) * mm, "end": v(360.64, 35.2) * mm});
            skLineSegment(sketch, "E1322", {"start": v(360.64, 35.2) * mm, "end": v(361.99, 35.85) * mm});
            skLineSegment(sketch, "E1323", {"start": v(361.99, 35.85) * mm, "end": v(363.99, 37.05) * mm});
            skLineSegment(sketch, "E1324", {"start": v(363.99, 37.05) * mm, "end": v(366.55, 38.89) * mm});
            skLineSegment(sketch, "E1325", {"start": v(366.55, 38.89) * mm, "end": v(369.57, 41.47) * mm});
            skLineSegment(sketch, "E1326", {"start": v(369.57, 41.47) * mm, "end": v(372.95, 44.88) * mm});
            skLineSegment(sketch, "E1327", {"start": v(372.95, 44.88) * mm, "end": v(376.55, 49.19) * mm});
            skLineSegment(sketch, "E1328", {"start": v(376.55, 49.19) * mm, "end": v(378.3, 51.67) * mm});
            skLineSegment(sketch, "E1329", {"start": v(378.3, 51.67) * mm, "end": v(376.3, 57.15) * mm});
            skLineSegment(sketch, "E1330", {"start": v(376.3, 57.15) * mm, "end": v(373.57, 62.3) * mm});
            skLineSegment(sketch, "E1331", {"start": v(373.57, 62.3) * mm, "end": v(370.56, 62.66) * mm});
            skLineSegment(sketch, "E1332", {"start": v(370.56, 62.66) * mm, "end": v(364.94, 62.86) * mm});
            skLineSegment(sketch, "E1333", {"start": v(364.94, 62.86) * mm, "end": v(360.14, 62.64) * mm});
            skLineSegment(sketch, "E1334", {"start": v(360.14, 62.64) * mm, "end": v(356.2, 62.12) * mm});
            skLineSegment(sketch, "E1335", {"start": v(356.2, 62.12) * mm, "end": v(353.13, 61.44) * mm});
            skLineSegment(sketch, "E1336", {"start": v(353.13, 61.44) * mm, "end": v(350.9, 60.76) * mm});
            skLineSegment(sketch, "E1337", {"start": v(350.9, 60.76) * mm, "end": v(349.5, 60.2) * mm});
            skLineSegment(sketch, "E1338", {"start": v(349.5, 60.2) * mm, "end": v(348.9, 59.9) * mm});
            skLineSegment(sketch, "E1339", {"start": v(348.9, 59.9) * mm, "end": v(346.02, 58.13) * mm});
            skLineSegment(sketch, "E1340", {"start": v(346.02, 58.13) * mm, "end": v(343.12, 56.98) * mm});
            skLineSegment(sketch, "E1341", {"start": v(343.12, 56.98) * mm, "end": v(340.77, 56.68) * mm});
            skLineSegment(sketch, "E1342", {"start": v(340.77, 56.68) * mm, "end": v(339.08, 57.12) * mm});
            skLineSegment(sketch, "E1343", {"start": v(339.08, 57.12) * mm, "end": v(338.16, 58.18) * mm});
            skLineSegment(sketch, "E1344", {"start": v(338.16, 58.18) * mm, "end": v(337.4, 59.43) * mm});
            skLineSegment(sketch, "E1345", {"start": v(337.4, 59.43) * mm, "end": v(332.11, 66.7) * mm});
            skLineSegment(sketch, "E1346", {"start": v(332.11, 66.7) * mm, "end": v(331.15, 67.82) * mm});
            skLineSegment(sketch, "E1347", {"start": v(331.15, 67.82) * mm, "end": v(330.43, 69.02) * mm});
            skLineSegment(sketch, "E1348", {"start": v(330.43, 69.02) * mm, "end": v(330.54, 70.76) * mm});
            skLineSegment(sketch, "E1349", {"start": v(330.54, 70.76) * mm, "end": v(331.55, 72.9) * mm});
            skLineSegment(sketch, "E1350", {"start": v(331.55, 72.9) * mm, "end": v(333.53, 75.3) * mm});
            skLineSegment(sketch, "E1351", {"start": v(333.53, 75.3) * mm, "end": v(336.1, 77.5) * mm});
            skLineSegment(sketch, "E1352", {"start": v(336.1, 77.5) * mm, "end": v(336.58, 77.99) * mm});
            skLineSegment(sketch, "E1353", {"start": v(336.58, 77.99) * mm, "end": v(337.55, 79.14) * mm});
            skLineSegment(sketch, "E1354", {"start": v(337.55, 79.14) * mm, "end": v(338.89, 81.04) * mm});
            skLineSegment(sketch, "E1355", {"start": v(338.89, 81.04) * mm, "end": v(340.48, 83.76) * mm});
            skLineSegment(sketch, "E1356", {"start": v(340.48, 83.76) * mm, "end": v(342.19, 87.35) * mm});
            skLineSegment(sketch, "E1357", {"start": v(342.19, 87.35) * mm, "end": v(343.89, 91.84) * mm});
            skLineSegment(sketch, "E1358", {"start": v(343.89, 91.84) * mm, "end": v(345.43, 97.24) * mm});
            skLineSegment(sketch, "E1359", {"start": v(345.43, 97.24) * mm, "end": v(346.01, 100.22) * mm});
            skLineSegment(sketch, "E1360", {"start": v(346.01, 100.22) * mm, "end": v(341.96, 104.41) * mm});
            skLineSegment(sketch, "E1361", {"start": v(341.96, 104.41) * mm, "end": v(337.37, 108) * mm});
            skLineSegment(sketch, "E1362", {"start": v(337.37, 108) * mm, "end": v(334.47, 107.11) * mm});
            skLineSegment(sketch, "E1363", {"start": v(334.47, 107.11) * mm, "end": v(329.25, 105.01) * mm});
            skLineSegment(sketch, "E1364", {"start": v(329.25, 105.01) * mm, "end": v(324.97, 102.86) * mm});
            skLineSegment(sketch, "E1365", {"start": v(324.97, 102.86) * mm, "end": v(321.58, 100.78) * mm});
            skLineSegment(sketch, "E1366", {"start": v(321.58, 100.78) * mm, "end": v(319.04, 98.91) * mm});
            skLineSegment(sketch, "E1367", {"start": v(319.04, 98.91) * mm, "end": v(317.29, 97.38) * mm});
            skLineSegment(sketch, "E1368", {"start": v(317.29, 97.38) * mm, "end": v(316.24, 96.3) * mm});
            skLineSegment(sketch, "E1369", {"start": v(316.24, 96.3) * mm, "end": v(315.81, 95.77) * mm});
            skLineSegment(sketch, "E1370", {"start": v(315.81, 95.77) * mm, "end": v(313.9, 92.99) * mm});
            skLineSegment(sketch, "E1371", {"start": v(313.9, 92.99) * mm, "end": v(311.71, 90.77) * mm});
            skLineSegment(sketch, "E1372", {"start": v(311.71, 90.77) * mm, "end": v(309.69, 89.53) * mm});
            skLineSegment(sketch, "E1373", {"start": v(309.69, 89.53) * mm, "end": v(307.97, 89.25) * mm});
            skLineSegment(sketch, "E1374", {"start": v(307.97, 89.25) * mm, "end": v(306.7, 89.84) * mm});
            skLineSegment(sketch, "E1375", {"start": v(306.7, 89.84) * mm, "end": v(305.5, 90.68) * mm});
            skLineSegment(sketch, "E1376", {"start": v(305.5, 90.68) * mm, "end": v(297.7, 95.17) * mm});
            skLineSegment(sketch, "E1377", {"start": v(297.7, 95.17) * mm, "end": v(296.38, 95.8) * mm});
            skLineSegment(sketch, "E1378", {"start": v(296.38, 95.8) * mm, "end": v(295.23, 96.6) * mm});
            skLineSegment(sketch, "E1379", {"start": v(295.23, 96.6) * mm, "end": v(294.62, 98.24) * mm});
            skLineSegment(sketch, "E1380", {"start": v(294.62, 98.24) * mm, "end": v(294.67, 100.6) * mm});
            skLineSegment(sketch, "E1381", {"start": v(294.67, 100.6) * mm, "end": v(295.5, 103.6) * mm});
            skLineSegment(sketch, "E1382", {"start": v(295.5, 103.6) * mm, "end": v(296.96, 106.66) * mm});
            skLineSegment(sketch, "E1383", {"start": v(296.96, 106.66) * mm, "end": v(297.2, 107.3) * mm});
            skLineSegment(sketch, "E1384", {"start": v(297.2, 107.3) * mm, "end": v(297.61, 108.74) * mm});
            skLineSegment(sketch, "E1385", {"start": v(297.61, 108.74) * mm, "end": v(298.06, 111.02) * mm});
            skLineSegment(sketch, "E1386", {"start": v(298.06, 111.02) * mm, "end": v(298.4, 114.16) * mm});
            skLineSegment(sketch, "E1387", {"start": v(298.4, 114.16) * mm, "end": v(298.51, 118.13) * mm});
            skLineSegment(sketch, "E1388", {"start": v(298.51, 118.13) * mm, "end": v(298.24, 122.92) * mm});
            skLineSegment(sketch, "E1389", {"start": v(298.24, 122.92) * mm, "end": v(297.45, 128.49) * mm});
            skLineSegment(sketch, "E1390", {"start": v(297.45, 128.49) * mm, "end": v(296.77, 131.44) * mm});
            skLineSegment(sketch, "E1391", {"start": v(296.77, 131.44) * mm, "end": v(291.37, 133.63) * mm});
            skLineSegment(sketch, "E1392", {"start": v(291.37, 133.63) * mm, "end": v(285.7, 135.04) * mm});
            skLineSegment(sketch, "E1393", {"start": v(285.7, 135.04) * mm, "end": v(283.42, 133.04) * mm});
            skLineSegment(sketch, "E1394", {"start": v(283.42, 133.04) * mm, "end": v(279.51, 129) * mm});
            skLineSegment(sketch, "E1395", {"start": v(279.51, 129) * mm, "end": v(276.47, 125.3) * mm});
            skLineSegment(sketch, "E1396", {"start": v(276.47, 125.3) * mm, "end": v(274.22, 122.01) * mm});
            skLineSegment(sketch, "E1397", {"start": v(274.22, 122.01) * mm, "end": v(272.66, 119.28) * mm});
            skLineSegment(sketch, "E1398", {"start": v(272.66, 119.28) * mm, "end": v(271.68, 117.16) * mm});
            skLineSegment(sketch, "E1399", {"start": v(271.68, 117.16) * mm, "end": v(271.17, 115.75) * mm});
            skLineSegment(sketch, "E1400", {"start": v(271.17, 115.75) * mm, "end": v(270.99, 115.1) * mm});
            skLineSegment(sketch, "E1401", {"start": v(270.99, 115.1) * mm, "end": v(270.37, 111.78) * mm});
            skLineSegment(sketch, "E1402", {"start": v(270.37, 111.78) * mm, "end": v(269.28, 108.85) * mm});
            skLineSegment(sketch, "E1403", {"start": v(269.28, 108.85) * mm, "end": v(267.93, 106.9) * mm});
            skLineSegment(sketch, "E1404", {"start": v(267.93, 106.9) * mm, "end": v(266.48, 105.94) * mm});
            skLineSegment(sketch, "E1405", {"start": v(266.48, 105.94) * mm, "end": v(265.08, 105.97) * mm});
            skLineSegment(sketch, "E1406", {"start": v(265.08, 105.97) * mm, "end": v(263.64, 106.24) * mm});
            skLineSegment(sketch, "E1407", {"start": v(263.64, 106.24) * mm, "end": v(254.7, 107.18) * mm});
            skLineSegment(sketch, "E1408", {"start": v(254.7, 107.18) * mm, "end": v(253.22, 107.21) * mm});
            skLineSegment(sketch, "E1409", {"start": v(253.22, 107.21) * mm, "end": v(251.85, 107.48) * mm});
            skLineSegment(sketch, "E1410", {"start": v(251.85, 107.48) * mm, "end": v(250.63, 108.72) * mm});
            skLineSegment(sketch, "E1411", {"start": v(250.63, 108.72) * mm, "end": v(249.71, 110.91) * mm});
            skLineSegment(sketch, "E1412", {"start": v(249.71, 110.91) * mm, "end": v(249.25, 114) * mm});
            skLineSegment(sketch, "E1413", {"start": v(249.25, 114) * mm, "end": v(249.34, 117.37) * mm});
            skLineSegment(sketch, "E1414", {"start": v(249.34, 117.37) * mm, "end": v(249.3, 118.05) * mm});
            skLineSegment(sketch, "E1415", {"start": v(249.3, 118.05) * mm, "end": v(249.1, 119.54) * mm});
            skLineSegment(sketch, "E1416", {"start": v(249.1, 119.54) * mm, "end": v(248.57, 121.8) * mm});
            skLineSegment(sketch, "E1417", {"start": v(248.57, 121.8) * mm, "end": v(247.61, 124.81) * mm});
            skLineSegment(sketch, "E1418", {"start": v(247.61, 124.81) * mm, "end": v(246.1, 128.48) * mm});
            skLineSegment(sketch, "E1419", {"start": v(246.1, 128.48) * mm, "end": v(243.9, 132.75) * mm});
            skLineSegment(sketch, "E1420", {"start": v(243.9, 132.75) * mm, "end": v(240.9, 137.51) * mm});
            skLineSegment(sketch, "E1421", {"start": v(240.9, 137.51) * mm, "end": v(239.09, 139.94) * mm});
            skLineSegment(sketch, "E1422", {"start": v(239.09, 139.94) * mm, "end": v(233.26, 139.73) * mm});
            skLineSegment(sketch, "E1423", {"start": v(233.26, 139.73) * mm, "end": v(227.52, 138.72) * mm});
            skLineSegment(sketch, "E1424", {"start": v(227.52, 138.72) * mm, "end": v(226.24, 135.97) * mm});
            skLineSegment(sketch, "E1425", {"start": v(226.24, 135.97) * mm, "end": v(224.31, 130.69) * mm});
            skLineSegment(sketch, "E1426", {"start": v(224.31, 130.69) * mm, "end": v(223.05, 126.06) * mm});
            skLineSegment(sketch, "E1427", {"start": v(223.05, 126.06) * mm, "end": v(222.32, 122.15) * mm});
            skLineSegment(sketch, "E1428", {"start": v(222.32, 122.15) * mm, "end": v(222.01, 119.02) * mm});
            skLineSegment(sketch, "E1429", {"start": v(222.01, 119.02) * mm, "end": v(221.98, 116.69) * mm});
            skLineSegment(sketch, "E1430", {"start": v(221.98, 116.69) * mm, "end": v(222.08, 115.19) * mm});
            skLineSegment(sketch, "E1431", {"start": v(222.08, 115.19) * mm, "end": v(222.18, 114.52) * mm});
            skLineSegment(sketch, "E1432", {"start": v(222.18, 114.52) * mm, "end": v(222.97, 111.23) * mm});
            skLineSegment(sketch, "E1433", {"start": v(222.97, 111.23) * mm, "end": v(223.16, 108.12) * mm});
            skLineSegment(sketch, "E1434", {"start": v(223.16, 108.12) * mm, "end": v(222.72, 105.8) * mm});
            skLineSegment(sketch, "E1435", {"start": v(222.72, 105.8) * mm, "end": v(221.79, 104.32) * mm});
            skLineSegment(sketch, "E1436", {"start": v(221.79, 104.32) * mm, "end": v(220.5, 103.77) * mm});
            skLineSegment(sketch, "E1437", {"start": v(220.5, 103.77) * mm, "end": v(219.07, 103.44) * mm});
            skLineSegment(sketch, "E1438", {"start": v(219.07, 103.44) * mm, "end": v(210.51, 100.66) * mm});
            skLineSegment(sketch, "E1439", {"start": v(210.51, 100.66) * mm, "end": v(209.16, 100.09) * mm});
            skLineSegment(sketch, "E1440", {"start": v(209.16, 100.09) * mm, "end": v(207.8, 99.78) * mm});
            skLineSegment(sketch, "E1441", {"start": v(207.8, 99.78) * mm, "end": v(206.17, 100.41) * mm});
            skLineSegment(sketch, "E1442", {"start": v(206.17, 100.41) * mm, "end": v(204.45, 102.04) * mm});
            skLineSegment(sketch, "E1443", {"start": v(204.45, 102.04) * mm, "end": v(202.77, 104.67) * mm});
            skLineSegment(sketch, "E1444", {"start": v(202.77, 104.67) * mm, "end": v(201.48, 107.8) * mm});
            skLineSegment(sketch, "E1445", {"start": v(201.48, 107.8) * mm, "end": v(201.17, 108.4) * mm});
            skLineSegment(sketch, "E1446", {"start": v(201.17, 108.4) * mm, "end": v(200.37, 109.67) * mm});
            skLineSegment(sketch, "E1447", {"start": v(200.37, 109.67) * mm, "end": v(198.97, 111.53) * mm});
            skLineSegment(sketch, "E1448", {"start": v(198.97, 111.53) * mm, "end": v(196.88, 113.88) * mm});
            skLineSegment(sketch, "E1449", {"start": v(196.88, 113.88) * mm, "end": v(194, 116.62) * mm});
            skLineSegment(sketch, "E1450", {"start": v(194, 116.62) * mm, "end": v(190.25, 119.62) * mm});
            skLineSegment(sketch, "E1451", {"start": v(190.25, 119.62) * mm, "end": v(185.59, 122.76) * mm});
            skLineSegment(sketch, "E1452", {"start": v(185.59, 122.76) * mm, "end": v(182.94, 124.24) * mm});
            skLineSegment(sketch, "E1453", {"start": v(182.94, 124.24) * mm, "end": v(177.7, 121.68) * mm});
            skLineSegment(sketch, "E1454", {"start": v(177.7, 121.68) * mm, "end": v(172.86, 118.42) * mm});
            skLineSegment(sketch, "E1455", {"start": v(172.86, 118.42) * mm, "end": v(172.82, 115.39) * mm});
            skLineSegment(sketch, "E1456", {"start": v(172.82, 115.39) * mm, "end": v(173.2, 109.78) * mm});
            skLineSegment(sketch, "E1457", {"start": v(173.2, 109.78) * mm, "end": v(173.93, 105.03) * mm});
            skLineSegment(sketch, "E1458", {"start": v(173.93, 105.03) * mm, "end": v(174.86, 101.17) * mm});
            skLineSegment(sketch, "E1459", {"start": v(174.86, 101.17) * mm, "end": v(175.85, 98.18) * mm});
            skLineSegment(sketch, "E1460", {"start": v(175.85, 98.18) * mm, "end": v(176.76, 96.04) * mm});
            skLineSegment(sketch, "E1461", {"start": v(176.76, 96.04) * mm, "end": v(177.46, 94.7) * mm});
            skLineSegment(sketch, "E1462", {"start": v(177.46, 94.7) * mm, "end": v(177.83, 94.14) * mm});
            skLineSegment(sketch, "E1463", {"start": v(177.83, 94.14) * mm, "end": v(179.89, 91.46) * mm});
            skLineSegment(sketch, "E1464", {"start": v(179.89, 91.46) * mm, "end": v(181.33, 88.7) * mm});
            skLineSegment(sketch, "E1465", {"start": v(181.33, 88.7) * mm, "end": v(181.88, 86.39) * mm});
            skLineSegment(sketch, "E1466", {"start": v(181.88, 86.39) * mm, "end": v(181.62, 84.66) * mm});
            skLineSegment(sketch, "E1467", {"start": v(181.62, 84.66) * mm, "end": v(180.66, 83.64) * mm});
            skLineSegment(sketch, "E1468", {"start": v(180.66, 83.64) * mm, "end": v(179.5, 82.75) * mm});
            skLineSegment(sketch, "E1469", {"start": v(179.5, 82.75) * mm, "end": v(172.8, 76.73) * mm});
            skLineSegment(sketch, "E1470", {"start": v(172.8, 76.73) * mm, "end": v(171.8, 75.66) * mm});
            skLineSegment(sketch, "E1471", {"start": v(171.8, 75.66) * mm, "end": v(170.68, 74.82) * mm});
            skLineSegment(sketch, "E1472", {"start": v(170.68, 74.82) * mm, "end": v(168.94, 74.74) * mm});
            skLineSegment(sketch, "E1473", {"start": v(168.94, 74.74) * mm, "end": v(166.7, 75.52) * mm});
            skLineSegment(sketch, "E1474", {"start": v(166.7, 75.52) * mm, "end": v(164.1, 77.25) * mm});
            skLineSegment(sketch, "E1475", {"start": v(164.1, 77.25) * mm, "end": v(161.65, 79.57) * mm});
            skLineSegment(sketch, "E1476", {"start": v(161.65, 79.57) * mm, "end": v(161.12, 80) * mm});
            skLineSegment(sketch, "E1477", {"start": v(161.12, 80) * mm, "end": v(159.88, 80.84) * mm});
            skLineSegment(sketch, "E1478", {"start": v(159.88, 80.84) * mm, "end": v(157.84, 81.97) * mm});
            skLineSegment(sketch, "E1479", {"start": v(157.84, 81.97) * mm, "end": v(154.97, 83.27) * mm});
            skLineSegment(sketch, "E1480", {"start": v(154.97, 83.27) * mm, "end": v(151.23, 84.6) * mm});
            skLineSegment(sketch, "E1481", {"start": v(151.23, 84.6) * mm, "end": v(146.58, 85.81) * mm});
            skLineSegment(sketch, "E1482", {"start": v(146.58, 85.81) * mm, "end": v(141.05, 86.78) * mm});
            skLineSegment(sketch, "E1483", {"start": v(141.05, 86.78) * mm, "end": v(138.03, 87.05) * mm});
            skLineSegment(sketch, "E1484", {"start": v(138.03, 87.05) * mm, "end": v(134.28, 82.59) * mm});
            skLineSegment(sketch, "E1485", {"start": v(134.28, 82.59) * mm, "end": v(131.19, 77.64) * mm});
            skLineSegment(sketch, "E1486", {"start": v(131.19, 77.64) * mm, "end": v(132.38, 74.85) * mm});
            skLineSegment(sketch, "E1487", {"start": v(132.38, 74.85) * mm, "end": v(135.01, 69.88) * mm});
            skLineSegment(sketch, "E1488", {"start": v(135.01, 69.88) * mm, "end": v(137.6, 65.85) * mm});
            skLineSegment(sketch, "E1489", {"start": v(137.6, 65.85) * mm, "end": v(140.03, 62.7) * mm});
            skLineSegment(sketch, "E1490", {"start": v(140.03, 62.7) * mm, "end": v(142.15, 60.36) * mm});
            skLineSegment(sketch, "E1491", {"start": v(142.15, 60.36) * mm, "end": v(143.85, 58.78) * mm});
            skLineSegment(sketch, "E1492", {"start": v(143.85, 58.78) * mm, "end": v(145.04, 57.85) * mm});
            skLineSegment(sketch, "E1493", {"start": v(145.04, 57.85) * mm, "end": v(145.6, 57.48) * mm});
            skLineSegment(sketch, "E1494", {"start": v(145.6, 57.48) * mm, "end": v(148.57, 55.87) * mm});
            skLineSegment(sketch, "E1495", {"start": v(148.57, 55.87) * mm, "end": v(151.01, 53.93) * mm});
            skLineSegment(sketch, "E1496", {"start": v(151.01, 53.93) * mm, "end": v(152.45, 52.04) * mm});
            skLineSegment(sketch, "E1497", {"start": v(152.45, 52.04) * mm, "end": v(152.92, 50.36) * mm});
            skLineSegment(sketch, "E1498", {"start": v(152.92, 50.36) * mm, "end": v(152.46, 49.04) * mm});
            skLineSegment(sketch, "E1499", {"start": v(152.46, 49.04) * mm, "end": v(151.75, 47.75) * mm});
            skLineSegment(sketch, "E1500", {"start": v(151.75, 47.75) * mm, "end": v(148.1, 39.53) * mm});
            skLineSegment(sketch, "E1501", {"start": v(148.1, 39.53) * mm, "end": v(147.61, 38.15) * mm});
            skLineSegment(sketch, "E1502", {"start": v(147.61, 38.15) * mm, "end": v(146.93, 36.92) * mm});
            skLineSegment(sketch, "E1503", {"start": v(146.93, 36.92) * mm, "end": v(145.37, 36.14) * mm});
            skLineSegment(sketch, "E1504", {"start": v(145.37, 36.14) * mm, "end": v(143, 35.95) * mm});
            skLineSegment(sketch, "E1505", {"start": v(143, 35.95) * mm, "end": v(139.93, 36.47) * mm});
            skLineSegment(sketch, "E1506", {"start": v(139.93, 36.47) * mm, "end": v(136.75, 37.6) * mm});
            skLineSegment(sketch, "E1507", {"start": v(136.75, 37.6) * mm, "end": v(136.1, 37.77) * mm});
            skLineSegment(sketch, "E1508", {"start": v(136.1, 37.77) * mm, "end": v(134.61, 38.03) * mm});
            skLineSegment(sketch, "E1509", {"start": v(134.61, 38.03) * mm, "end": v(132.3, 38.23) * mm});
            skLineSegment(sketch, "E1510", {"start": v(132.3, 38.23) * mm, "end": v(129.14, 38.25) * mm});
            skLineSegment(sketch, "E1511", {"start": v(129.14, 38.25) * mm, "end": v(125.18, 37.94) * mm});
            skLineSegment(sketch, "E1512", {"start": v(125.18, 37.94) * mm, "end": v(120.44, 37.17) * mm});
            skLineSegment(sketch, "E1513", {"start": v(120.44, 37.17) * mm, "end": v(115, 35.8) * mm});
            skLineSegment(sketch, "E1514", {"start": v(115, 35.8) * mm, "end": v(112.12, 34.82) * mm});
            skCircle(sketch, "E1515", {"center": v(-123.97, 0) * mm, "radius": 5.77 * mm, "construction": true});
            skCircle(sketch, "E1516", {"center": v(248.44, 0) * mm, "radius": 5.77 * mm});
            skCircle(sketch, "E1517", {"center": v(-123.97, 0) * mm, "radius": 11 * mm});
            skLineSegment(sketch, "E1518.0.0", {"start": v(249.94, 2) * mm, "end": v(246.94, 2) * mm});
            skArc(sketch, "E1518.0.1", {"start": v(246.94, 2) * mm, "mid": v(248.44, -2.5) * mm, "end": v(249.94, 2) * mm});
            skSolve(sketch);
        }
        {
            var Q0;
            Q0=makeQuery(id+"F0.imprint","IMPRINT",FACE,{"disambiguationData":[TD([[makeQuery(id+"F0.imprint","IMPRINT",EDGE,{"derivedFrom":sQuery(id+"F0.wireOp",EDGE,"E1050")}),1.0]])]});
            var Q1;
            Q1=makeQuery(id+"F0.imprint","IMPRINT",FACE,{"disambiguationData":[TD([[makeQuery(id+"F0.imprint","IMPRINT",EDGE,{"derivedFrom":sQuery(id+"F0.wireOp",EDGE,"E1518.0.0")}),1.0]])]});
            var Q2;
            Q2=makeQuery(id+"F0.imprint","IMPRINT",FACE,{"disambiguationData":[TD([[makeQuery(id+"F0.imprint","IMPRINT",EDGE,{"derivedFrom":sQuery(id+"F0.wireOp",EDGE,"E1516")}),1.0]])]});
            extrude(context, id + "F1", {"entities" : qUnion([Q0, Q1, Q2]), "depth" : 4 * mm, "offsetDistance" : 25 * mm});
        }
        {
            var Q0;
            Q0=makeQuery(id+"F0.imprint","IMPRINT",FACE,{"disambiguationData":[TD([[makeQuery(id+"F0.imprint","IMPRINT",EDGE,{"derivedFrom":sQuery(id+"F0.wireOp",EDGE,"E0")}),1.0]])]});
            extrude(context, id + "F2", {"entities" : qUnion([Q0]), "depth" : 4 * mm, "offsetDistance" : 25 * mm});
        }
    });
